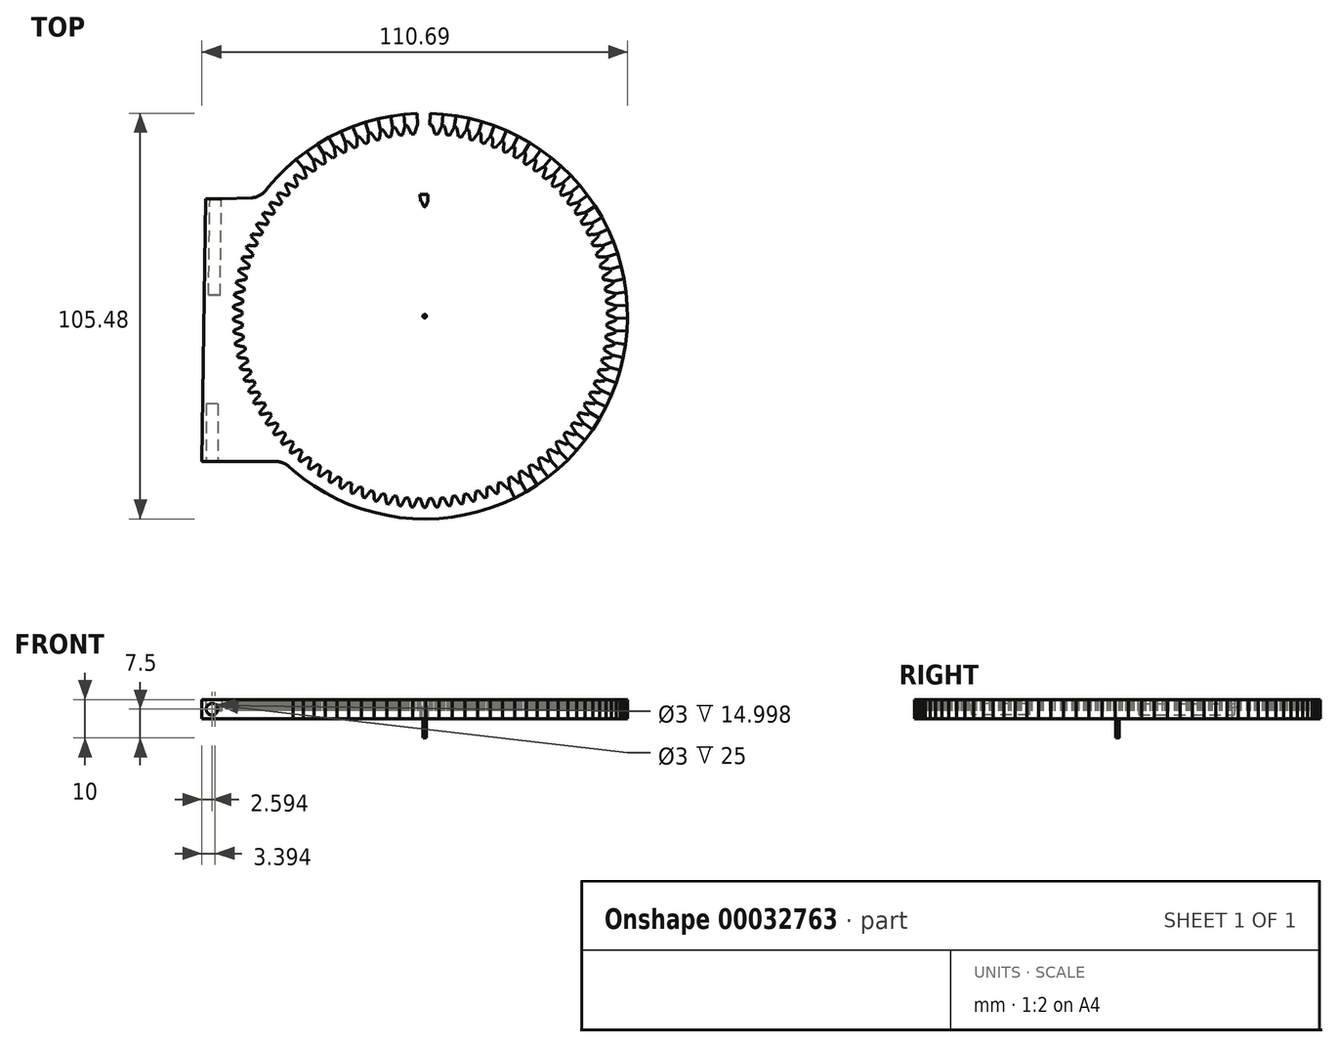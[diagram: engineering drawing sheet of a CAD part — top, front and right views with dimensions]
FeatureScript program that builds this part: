
annotation { "Feature Type Name" : "Feature", "Feature Type Description" : "" }
export const myFeature = defineFeature(function(context is Context, id is Id, definition is map)
    precondition{}
    {
        {
            var Q0;
            Q0=qCreatedBy(makeId("Top.planeOp"),FACE);
            var sketch = newSketch(context, id + "F0", { "sketchPlane" : qUnion([Q0])});
            skCircle(sketch, "E0", {"center": v(0, 0) * mm, "radius": 52.75 * mm});
            skLineSegment(sketch, "E1", {"start": v(1.31, 49.73) * mm, "end": v(1.3, 49.69) * mm});
            skLineSegment(sketch, "E2", {"start": v(1.3, 49.69) * mm, "end": v(1.27, 49.64) * mm});
            skLineSegment(sketch, "E3", {"start": v(1.27, 49.64) * mm, "end": v(1.25, 49.6) * mm});
            skLineSegment(sketch, "E4", {"start": v(1.25, 49.6) * mm, "end": v(1.23, 49.55) * mm});
            skLineSegment(sketch, "E5", {"start": v(1.23, 49.55) * mm, "end": v(1.21, 49.51) * mm});
            skLineSegment(sketch, "E6", {"start": v(1.21, 49.51) * mm, "end": v(1.2, 49.47) * mm});
            skLineSegment(sketch, "E7", {"start": v(1.2, 49.47) * mm, "end": v(1.17, 49.42) * mm});
            skLineSegment(sketch, "E8", {"start": v(1.17, 49.42) * mm, "end": v(1.15, 49.38) * mm});
            skLineSegment(sketch, "E9", {"start": v(1.15, 49.38) * mm, "end": v(1.13, 49.33) * mm});
            skLineSegment(sketch, "E10", {"start": v(1.13, 49.33) * mm, "end": v(1.11, 49.29) * mm});
            skLineSegment(sketch, "E11", {"start": v(1.11, 49.29) * mm, "end": v(1.1, 49.24) * mm});
            skLineSegment(sketch, "E12", {"start": v(1.1, 49.24) * mm, "end": v(1.07, 49.2) * mm});
            skLineSegment(sketch, "E13", {"start": v(1.07, 49.2) * mm, "end": v(1.05, 49.15) * mm});
            skLineSegment(sketch, "E14", {"start": v(1.05, 49.15) * mm, "end": v(1.03, 49.1) * mm});
            skLineSegment(sketch, "E15", {"start": v(1.03, 49.1) * mm, "end": v(1.02, 49.06) * mm});
            skLineSegment(sketch, "E16", {"start": v(1.02, 49.06) * mm, "end": v(1, 49.02) * mm});
            skLineSegment(sketch, "E17", {"start": v(1, 49.02) * mm, "end": v(0.98, 48.98) * mm});
            skLineSegment(sketch, "E18", {"start": v(0.98, 48.98) * mm, "end": v(0.96, 48.93) * mm});
            skLineSegment(sketch, "E19", {"start": v(0.96, 48.93) * mm, "end": v(0.94, 48.89) * mm});
            skLineSegment(sketch, "E20", {"start": v(0.94, 48.89) * mm, "end": v(0.92, 48.84) * mm});
            skLineSegment(sketch, "E21", {"start": v(0.92, 48.84) * mm, "end": v(0.9, 48.8) * mm});
            skLineSegment(sketch, "E22", {"start": v(0.9, 48.8) * mm, "end": v(0.89, 48.75) * mm});
            skLineSegment(sketch, "E23", {"start": v(0.89, 48.75) * mm, "end": v(0.87, 48.7) * mm});
            skLineSegment(sketch, "E24", {"start": v(0.87, 48.7) * mm, "end": v(0.85, 48.66) * mm});
            skLineSegment(sketch, "E25", {"start": v(0.85, 48.66) * mm, "end": v(0.83, 48.62) * mm});
            skLineSegment(sketch, "E26", {"start": v(0.83, 48.62) * mm, "end": v(0.82, 48.57) * mm});
            skLineSegment(sketch, "E27", {"start": v(0.82, 48.57) * mm, "end": v(0.8, 48.53) * mm});
            skLineSegment(sketch, "E28", {"start": v(0.8, 48.53) * mm, "end": v(0.78, 48.48) * mm});
            skLineSegment(sketch, "E29", {"start": v(0.78, 48.48) * mm, "end": v(0.76, 48.44) * mm});
            skLineSegment(sketch, "E30", {"start": v(0.76, 48.44) * mm, "end": v(0.75, 48.4) * mm});
            skLineSegment(sketch, "E31", {"start": v(0.75, 48.4) * mm, "end": v(0.73, 48.35) * mm});
            skLineSegment(sketch, "E32", {"start": v(0.73, 48.35) * mm, "end": v(0.71, 48.3) * mm});
            skLineSegment(sketch, "E33", {"start": v(0.71, 48.3) * mm, "end": v(0.7, 48.26) * mm});
            skLineSegment(sketch, "E34", {"start": v(0.7, 48.26) * mm, "end": v(0.68, 48.22) * mm});
            skLineSegment(sketch, "E35", {"start": v(0.68, 48.22) * mm, "end": v(0.67, 48.17) * mm});
            skLineSegment(sketch, "E36", {"start": v(0.67, 48.17) * mm, "end": v(0.65, 48.13) * mm});
            skLineSegment(sketch, "E37", {"start": v(0.65, 48.13) * mm, "end": v(0.63, 48.08) * mm});
            skLineSegment(sketch, "E38", {"start": v(0.63, 48.08) * mm, "end": v(0.62, 48.04) * mm});
            skLineSegment(sketch, "E39", {"start": v(0.62, 48.04) * mm, "end": v(0.6, 48) * mm});
            skLineSegment(sketch, "E40", {"start": v(0.6, 48) * mm, "end": v(0.58, 47.95) * mm});
            skLineSegment(sketch, "E41", {"start": v(0.58, 47.95) * mm, "end": v(0.57, 47.9) * mm});
            skLineSegment(sketch, "E42", {"start": v(0.57, 47.9) * mm, "end": v(0.55, 47.86) * mm});
            skLineSegment(sketch, "E43", {"start": v(0.55, 47.86) * mm, "end": v(0.53, 47.81) * mm});
            skLineSegment(sketch, "E44", {"start": v(0.53, 47.81) * mm, "end": v(0.52, 47.77) * mm});
            skLineSegment(sketch, "E45", {"start": v(0.52, 47.77) * mm, "end": v(0.5, 47.72) * mm});
            skLineSegment(sketch, "E46", {"start": v(0.5, 47.72) * mm, "end": v(0.49, 47.68) * mm});
            skLineSegment(sketch, "E47", {"start": v(0.49, 47.68) * mm, "end": v(0.47, 47.63) * mm});
            skLineSegment(sketch, "E48", {"start": v(0.47, 47.63) * mm, "end": v(0.45, 47.59) * mm});
            skLineSegment(sketch, "E49", {"start": v(0.45, 47.59) * mm, "end": v(0.44, 47.54) * mm});
            skLineSegment(sketch, "E50", {"start": v(0.44, 47.54) * mm, "end": v(0, 47.5) * mm});
            skLineSegment(sketch, "E51", {"start": v(0, 47.5) * mm, "end": v(-0.44, 47.54) * mm});
            skLineSegment(sketch, "E52", {"start": v(-0.44, 47.54) * mm, "end": v(-0.45, 47.59) * mm});
            skLineSegment(sketch, "E53", {"start": v(-0.45, 47.59) * mm, "end": v(-0.47, 47.63) * mm});
            skLineSegment(sketch, "E54", {"start": v(-0.47, 47.63) * mm, "end": v(-0.49, 47.68) * mm});
            skLineSegment(sketch, "E55", {"start": v(-0.49, 47.68) * mm, "end": v(-0.5, 47.72) * mm});
            skLineSegment(sketch, "E56", {"start": v(-0.5, 47.72) * mm, "end": v(-0.52, 47.77) * mm});
            skLineSegment(sketch, "E57", {"start": v(-0.52, 47.77) * mm, "end": v(-0.53, 47.81) * mm});
            skLineSegment(sketch, "E58", {"start": v(-0.53, 47.81) * mm, "end": v(-0.55, 47.86) * mm});
            skLineSegment(sketch, "E59", {"start": v(-0.55, 47.86) * mm, "end": v(-0.57, 47.9) * mm});
            skLineSegment(sketch, "E60", {"start": v(-0.57, 47.9) * mm, "end": v(-0.58, 47.95) * mm});
            skLineSegment(sketch, "E61", {"start": v(-0.58, 47.95) * mm, "end": v(-0.6, 48) * mm});
            skLineSegment(sketch, "E62", {"start": v(-0.6, 48) * mm, "end": v(-0.62, 48.04) * mm});
            skLineSegment(sketch, "E63", {"start": v(-0.62, 48.04) * mm, "end": v(-0.63, 48.08) * mm});
            skLineSegment(sketch, "E64", {"start": v(-0.63, 48.08) * mm, "end": v(-0.65, 48.13) * mm});
            skLineSegment(sketch, "E65", {"start": v(-0.65, 48.13) * mm, "end": v(-0.67, 48.17) * mm});
            skLineSegment(sketch, "E66", {"start": v(-0.67, 48.17) * mm, "end": v(-0.68, 48.22) * mm});
            skLineSegment(sketch, "E67", {"start": v(-0.68, 48.22) * mm, "end": v(-0.7, 48.26) * mm});
            skLineSegment(sketch, "E68", {"start": v(-0.7, 48.26) * mm, "end": v(-0.71, 48.3) * mm});
            skLineSegment(sketch, "E69", {"start": v(-0.71, 48.3) * mm, "end": v(-0.73, 48.35) * mm});
            skLineSegment(sketch, "E70", {"start": v(-0.73, 48.35) * mm, "end": v(-0.75, 48.4) * mm});
            skLineSegment(sketch, "E71", {"start": v(-0.75, 48.4) * mm, "end": v(-0.76, 48.44) * mm});
            skLineSegment(sketch, "E72", {"start": v(-0.76, 48.44) * mm, "end": v(-0.78, 48.48) * mm});
            skLineSegment(sketch, "E73", {"start": v(-0.78, 48.48) * mm, "end": v(-0.8, 48.53) * mm});
            skLineSegment(sketch, "E74", {"start": v(-0.8, 48.53) * mm, "end": v(-0.82, 48.57) * mm});
            skLineSegment(sketch, "E75", {"start": v(-0.82, 48.57) * mm, "end": v(-0.83, 48.62) * mm});
            skLineSegment(sketch, "E76", {"start": v(-0.83, 48.62) * mm, "end": v(-0.85, 48.66) * mm});
            skLineSegment(sketch, "E77", {"start": v(-0.85, 48.66) * mm, "end": v(-0.87, 48.7) * mm});
            skLineSegment(sketch, "E78", {"start": v(-0.87, 48.7) * mm, "end": v(-0.89, 48.75) * mm});
            skLineSegment(sketch, "E79", {"start": v(-0.89, 48.75) * mm, "end": v(-0.9, 48.8) * mm});
            skLineSegment(sketch, "E80", {"start": v(-0.9, 48.8) * mm, "end": v(-0.92, 48.84) * mm});
            skLineSegment(sketch, "E81", {"start": v(-0.92, 48.84) * mm, "end": v(-0.94, 48.89) * mm});
            skLineSegment(sketch, "E82", {"start": v(-0.94, 48.89) * mm, "end": v(-0.96, 48.93) * mm});
            skLineSegment(sketch, "E83", {"start": v(-0.96, 48.93) * mm, "end": v(-0.98, 48.98) * mm});
            skLineSegment(sketch, "E84", {"start": v(-0.98, 48.98) * mm, "end": v(-1, 49.02) * mm});
            skLineSegment(sketch, "E85", {"start": v(-1, 49.02) * mm, "end": v(-1.02, 49.06) * mm});
            skLineSegment(sketch, "E86", {"start": v(-1.02, 49.06) * mm, "end": v(-1.03, 49.1) * mm});
            skLineSegment(sketch, "E87", {"start": v(-1.03, 49.1) * mm, "end": v(-1.05, 49.15) * mm});
            skLineSegment(sketch, "E88", {"start": v(-1.05, 49.15) * mm, "end": v(-1.07, 49.2) * mm});
            skLineSegment(sketch, "E89", {"start": v(-1.07, 49.2) * mm, "end": v(-1.1, 49.24) * mm});
            skLineSegment(sketch, "E90", {"start": v(-1.1, 49.24) * mm, "end": v(-1.11, 49.29) * mm});
            skLineSegment(sketch, "E91", {"start": v(-1.11, 49.29) * mm, "end": v(-1.13, 49.33) * mm});
            skLineSegment(sketch, "E92", {"start": v(-1.13, 49.33) * mm, "end": v(-1.15, 49.38) * mm});
            skLineSegment(sketch, "E93", {"start": v(-1.15, 49.38) * mm, "end": v(-1.17, 49.42) * mm});
            skLineSegment(sketch, "E94", {"start": v(-1.17, 49.42) * mm, "end": v(-1.2, 49.47) * mm});
            skLineSegment(sketch, "E95", {"start": v(-1.2, 49.47) * mm, "end": v(-1.21, 49.51) * mm});
            skLineSegment(sketch, "E96", {"start": v(-1.21, 49.51) * mm, "end": v(-1.23, 49.55) * mm});
            skLineSegment(sketch, "E97", {"start": v(-1.23, 49.55) * mm, "end": v(-1.25, 49.6) * mm});
            skLineSegment(sketch, "E98", {"start": v(-1.25, 49.6) * mm, "end": v(-1.27, 49.64) * mm});
            skLineSegment(sketch, "E99", {"start": v(-1.27, 49.64) * mm, "end": v(-1.3, 49.69) * mm});
            skLineSegment(sketch, "E100", {"start": v(-1.3, 49.69) * mm, "end": v(-1.31, 49.73) * mm});
            skLineSegment(sketch, "E101", {"start": v(-1.31, 49.73) * mm, "end": v(-1.9, 49.71) * mm});
            skLineSegment(sketch, "E102", {"start": v(0, 0) * mm, "end": v(-2.02, 52.71) * mm});
            skLineSegment(sketch, "E103", {"start": v(0, 0) * mm, "end": v(1.4, 52.73) * mm});
            skLineSegment(sketch, "E104", {"start": v(-2.02, 52.71) * mm, "end": v(1.4, 52.73) * mm});
            skCircle(sketch, "E105", {"center": v(0, 0) * mm, "radius": 0.44 * mm});
            skSolve(sketch);
        }
        {
            var Q0;
            {var subQ3=sQuery(id+"F0.wireOp",EDGE,"E1");Q0=makeQuery(id+"F0.imprint","IMPRINT",FACE,{"disambiguationData":[TD([[makeQuery(id+"F0.imprint","IMPRINT",EDGE,{"derivedFrom":subQ3}),-1.0]])]});}
            var Q1;
            {var subQ1=sQuery(id+"F0.wireOp",EDGE,"E103");var subQ3=sQuery(id+"F0.wireOp",EDGE,"E102");var subQ5=makeQuery(id+"F0.imprint","INTERSECT",VERTEX,{"derivedFrom":[subQ3,subQ1]});Q1=makeQuery(id+"F0.imprint","IMPRINT",FACE,{"disambiguationData":[TD([[makeQuery(id+"F0.imprint","IMPRINT",EDGE,{"disambiguationData":[TD([[subQ5,-1.0]])],"derivedFrom":subQ3}),1.0]])]});}
            var Q2;
            {var subQ0=sQuery(id+"F0.wireOp",EDGE,"E103");var subQ3=sQuery(id+"F0.wireOp",EDGE,"E102");var subQ4=makeQuery(id+"F0.imprint","INTERSECT",VERTEX,{"derivedFrom":[subQ3,subQ0]});Q2=makeQuery(id+"F0.imprint","IMPRINT",FACE,{"disambiguationData":[TD([[makeQuery(id+"F0.imprint","IMPRINT",EDGE,{"disambiguationData":[TD([[subQ4,-1.0]])],"derivedFrom":subQ3}),-1.0]])]});}
            extrude(context, id + "F1", {"entities" : qUnion([Q0, Q1, Q2]), "depth" : 5 * mm});
        }
        {
            var Q0;
            Q0=makeQuery(id+"F1.opExtrude","SWEPT_BODY",BODY,{"disambiguationData":[OSD([sQuery(id+"F0.wireOp",EDGE,"E1"),sQuery(id+"F0.wireOp",EDGE,"E2"),sQuery(id+"F0.wireOp",EDGE,"E3"),sQuery(id+"F0.wireOp",EDGE,"E4"),sQuery(id+"F0.wireOp",EDGE,"E5"),sQuery(id+"F0.wireOp",EDGE,"E6"),sQuery(id+"F0.wireOp",EDGE,"E7"),sQuery(id+"F0.wireOp",EDGE,"E8"),sQuery(id+"F0.wireOp",EDGE,"E9"),sQuery(id+"F0.wireOp",EDGE,"E10"),sQuery(id+"F0.wireOp",EDGE,"E11"),sQuery(id+"F0.wireOp",EDGE,"E12"),sQuery(id+"F0.wireOp",EDGE,"E13"),sQuery(id+"F0.wireOp",EDGE,"E14"),sQuery(id+"F0.wireOp",EDGE,"E15"),sQuery(id+"F0.wireOp",EDGE,"E16"),sQuery(id+"F0.wireOp",EDGE,"E17"),sQuery(id+"F0.wireOp",EDGE,"E18"),sQuery(id+"F0.wireOp",EDGE,"E19"),sQuery(id+"F0.wireOp",EDGE,"E20"),sQuery(id+"F0.wireOp",EDGE,"E21"),sQuery(id+"F0.wireOp",EDGE,"E22"),sQuery(id+"F0.wireOp",EDGE,"E23"),sQuery(id+"F0.wireOp",EDGE,"E24"),sQuery(id+"F0.wireOp",EDGE,"E25"),sQuery(id+"F0.wireOp",EDGE,"E26"),sQuery(id+"F0.wireOp",EDGE,"E27"),sQuery(id+"F0.wireOp",EDGE,"E28"),sQuery(id+"F0.wireOp",EDGE,"E29"),sQuery(id+"F0.wireOp",EDGE,"E30"),sQuery(id+"F0.wireOp",EDGE,"E31"),sQuery(id+"F0.wireOp",EDGE,"E32"),sQuery(id+"F0.wireOp",EDGE,"E33"),sQuery(id+"F0.wireOp",EDGE,"E34"),sQuery(id+"F0.wireOp",EDGE,"E35"),sQuery(id+"F0.wireOp",EDGE,"E36"),sQuery(id+"F0.wireOp",EDGE,"E37"),sQuery(id+"F0.wireOp",EDGE,"E38"),sQuery(id+"F0.wireOp",EDGE,"E39"),sQuery(id+"F0.wireOp",EDGE,"E40"),sQuery(id+"F0.wireOp",EDGE,"E41"),sQuery(id+"F0.wireOp",EDGE,"E42"),sQuery(id+"F0.wireOp",EDGE,"E43"),sQuery(id+"F0.wireOp",EDGE,"E44"),sQuery(id+"F0.wireOp",EDGE,"E45"),sQuery(id+"F0.wireOp",EDGE,"E46"),sQuery(id+"F0.wireOp",EDGE,"E47"),sQuery(id+"F0.wireOp",EDGE,"E48"),sQuery(id+"F0.wireOp",EDGE,"E49"),sQuery(id+"F0.wireOp",EDGE,"E50"),sQuery(id+"F0.wireOp",EDGE,"E51"),sQuery(id+"F0.wireOp",EDGE,"E52"),sQuery(id+"F0.wireOp",EDGE,"E53"),sQuery(id+"F0.wireOp",EDGE,"E54"),sQuery(id+"F0.wireOp",EDGE,"E55"),sQuery(id+"F0.wireOp",EDGE,"E56"),sQuery(id+"F0.wireOp",EDGE,"E57"),sQuery(id+"F0.wireOp",EDGE,"E58"),sQuery(id+"F0.wireOp",EDGE,"E59"),sQuery(id+"F0.wireOp",EDGE,"E60"),sQuery(id+"F0.wireOp",EDGE,"E61"),sQuery(id+"F0.wireOp",EDGE,"E62"),sQuery(id+"F0.wireOp",EDGE,"E63"),sQuery(id+"F0.wireOp",EDGE,"E64"),sQuery(id+"F0.wireOp",EDGE,"E65"),sQuery(id+"F0.wireOp",EDGE,"E66"),sQuery(id+"F0.wireOp",EDGE,"E67"),sQuery(id+"F0.wireOp",EDGE,"E68"),sQuery(id+"F0.wireOp",EDGE,"E69"),sQuery(id+"F0.wireOp",EDGE,"E70"),sQuery(id+"F0.wireOp",EDGE,"E71"),sQuery(id+"F0.wireOp",EDGE,"E72"),sQuery(id+"F0.wireOp",EDGE,"E73"),sQuery(id+"F0.wireOp",EDGE,"E74"),sQuery(id+"F0.wireOp",EDGE,"E75"),sQuery(id+"F0.wireOp",EDGE,"E76"),sQuery(id+"F0.wireOp",EDGE,"E77"),sQuery(id+"F0.wireOp",EDGE,"E78"),sQuery(id+"F0.wireOp",EDGE,"E79"),sQuery(id+"F0.wireOp",EDGE,"E80"),sQuery(id+"F0.wireOp",EDGE,"E81"),sQuery(id+"F0.wireOp",EDGE,"E82"),sQuery(id+"F0.wireOp",EDGE,"E83"),sQuery(id+"F0.wireOp",EDGE,"E84"),sQuery(id+"F0.wireOp",EDGE,"E85"),sQuery(id+"F0.wireOp",EDGE,"E86"),sQuery(id+"F0.wireOp",EDGE,"E87"),sQuery(id+"F0.wireOp",EDGE,"E88"),sQuery(id+"F0.wireOp",EDGE,"E89"),sQuery(id+"F0.wireOp",EDGE,"E90"),sQuery(id+"F0.wireOp",EDGE,"E91"),sQuery(id+"F0.wireOp",EDGE,"E92"),sQuery(id+"F0.wireOp",EDGE,"E93"),sQuery(id+"F0.wireOp",EDGE,"E94"),sQuery(id+"F0.wireOp",EDGE,"E95"),sQuery(id+"F0.wireOp",EDGE,"E96"),sQuery(id+"F0.wireOp",EDGE,"E97"),sQuery(id+"F0.wireOp",EDGE,"E98"),sQuery(id+"F0.wireOp",EDGE,"E99"),sQuery(id+"F0.wireOp",EDGE,"E100"),sQuery(id+"F0.wireOp",EDGE,"E101"),sQuery(id+"F0.wireOp",EDGE,"E102"),sQuery(id+"F0.wireOp",EDGE,"E103"),sQuery(id+"F0.wireOp",EDGE,"E104")])]});
            var Q1;
            Q1=makeQuery(id+"F1.opExtrude","CAP_EDGE",EDGE,{"disambiguationData":[OSD([sQuery(id+"F0.wireOp",EDGE,"E105")])],"isStart":false});
            circularPattern(context, id + "F2", {"entities" : qUnion([Q0]), "axis" : qUnion([Q1]), "angle" : 3.7 * degree, "instanceCount" : round(97)});
        }
        {
            var Q0;
            Q0=makeQuery(id+"F1.opExtrude","SWEPT_BODY",BODY,{"disambiguationData":[OSD([sQuery(id+"F0.wireOp",EDGE,"E105")])]});
            var Q1;
            Q1=makeQuery(id+"F2.opPattern","COPY",BODY,{"derivedFrom":makeQuery(id+"F1.opExtrude","SWEPT_BODY",BODY,{"disambiguationData":[OSD([sQuery(id+"F0.wireOp",EDGE,"E1"),sQuery(id+"F0.wireOp",EDGE,"E2"),sQuery(id+"F0.wireOp",EDGE,"E3"),sQuery(id+"F0.wireOp",EDGE,"E4"),sQuery(id+"F0.wireOp",EDGE,"E5"),sQuery(id+"F0.wireOp",EDGE,"E6"),sQuery(id+"F0.wireOp",EDGE,"E7"),sQuery(id+"F0.wireOp",EDGE,"E8"),sQuery(id+"F0.wireOp",EDGE,"E9"),sQuery(id+"F0.wireOp",EDGE,"E10"),sQuery(id+"F0.wireOp",EDGE,"E11"),sQuery(id+"F0.wireOp",EDGE,"E12"),sQuery(id+"F0.wireOp",EDGE,"E13"),sQuery(id+"F0.wireOp",EDGE,"E14"),sQuery(id+"F0.wireOp",EDGE,"E15"),sQuery(id+"F0.wireOp",EDGE,"E16"),sQuery(id+"F0.wireOp",EDGE,"E17"),sQuery(id+"F0.wireOp",EDGE,"E18"),sQuery(id+"F0.wireOp",EDGE,"E19"),sQuery(id+"F0.wireOp",EDGE,"E20"),sQuery(id+"F0.wireOp",EDGE,"E21"),sQuery(id+"F0.wireOp",EDGE,"E22"),sQuery(id+"F0.wireOp",EDGE,"E23"),sQuery(id+"F0.wireOp",EDGE,"E24"),sQuery(id+"F0.wireOp",EDGE,"E25"),sQuery(id+"F0.wireOp",EDGE,"E26"),sQuery(id+"F0.wireOp",EDGE,"E27"),sQuery(id+"F0.wireOp",EDGE,"E28"),sQuery(id+"F0.wireOp",EDGE,"E29"),sQuery(id+"F0.wireOp",EDGE,"E30"),sQuery(id+"F0.wireOp",EDGE,"E31"),sQuery(id+"F0.wireOp",EDGE,"E32"),sQuery(id+"F0.wireOp",EDGE,"E33"),sQuery(id+"F0.wireOp",EDGE,"E34"),sQuery(id+"F0.wireOp",EDGE,"E35"),sQuery(id+"F0.wireOp",EDGE,"E36"),sQuery(id+"F0.wireOp",EDGE,"E37"),sQuery(id+"F0.wireOp",EDGE,"E38"),sQuery(id+"F0.wireOp",EDGE,"E39"),sQuery(id+"F0.wireOp",EDGE,"E40"),sQuery(id+"F0.wireOp",EDGE,"E41"),sQuery(id+"F0.wireOp",EDGE,"E42"),sQuery(id+"F0.wireOp",EDGE,"E43"),sQuery(id+"F0.wireOp",EDGE,"E44"),sQuery(id+"F0.wireOp",EDGE,"E45"),sQuery(id+"F0.wireOp",EDGE,"E46"),sQuery(id+"F0.wireOp",EDGE,"E47"),sQuery(id+"F0.wireOp",EDGE,"E48"),sQuery(id+"F0.wireOp",EDGE,"E49"),sQuery(id+"F0.wireOp",EDGE,"E50"),sQuery(id+"F0.wireOp",EDGE,"E51"),sQuery(id+"F0.wireOp",EDGE,"E52"),sQuery(id+"F0.wireOp",EDGE,"E53"),sQuery(id+"F0.wireOp",EDGE,"E54"),sQuery(id+"F0.wireOp",EDGE,"E55"),sQuery(id+"F0.wireOp",EDGE,"E56"),sQuery(id+"F0.wireOp",EDGE,"E57"),sQuery(id+"F0.wireOp",EDGE,"E58"),sQuery(id+"F0.wireOp",EDGE,"E59"),sQuery(id+"F0.wireOp",EDGE,"E60"),sQuery(id+"F0.wireOp",EDGE,"E61"),sQuery(id+"F0.wireOp",EDGE,"E62"),sQuery(id+"F0.wireOp",EDGE,"E63"),sQuery(id+"F0.wireOp",EDGE,"E64"),sQuery(id+"F0.wireOp",EDGE,"E65"),sQuery(id+"F0.wireOp",EDGE,"E66"),sQuery(id+"F0.wireOp",EDGE,"E67"),sQuery(id+"F0.wireOp",EDGE,"E68"),sQuery(id+"F0.wireOp",EDGE,"E69"),sQuery(id+"F0.wireOp",EDGE,"E70"),sQuery(id+"F0.wireOp",EDGE,"E71"),sQuery(id+"F0.wireOp",EDGE,"E72"),sQuery(id+"F0.wireOp",EDGE,"E73"),sQuery(id+"F0.wireOp",EDGE,"E74"),sQuery(id+"F0.wireOp",EDGE,"E75"),sQuery(id+"F0.wireOp",EDGE,"E76"),sQuery(id+"F0.wireOp",EDGE,"E77"),sQuery(id+"F0.wireOp",EDGE,"E78"),sQuery(id+"F0.wireOp",EDGE,"E79"),sQuery(id+"F0.wireOp",EDGE,"E80"),sQuery(id+"F0.wireOp",EDGE,"E81"),sQuery(id+"F0.wireOp",EDGE,"E82"),sQuery(id+"F0.wireOp",EDGE,"E83"),sQuery(id+"F0.wireOp",EDGE,"E84"),sQuery(id+"F0.wireOp",EDGE,"E85"),sQuery(id+"F0.wireOp",EDGE,"E86"),sQuery(id+"F0.wireOp",EDGE,"E87"),sQuery(id+"F0.wireOp",EDGE,"E88"),sQuery(id+"F0.wireOp",EDGE,"E89"),sQuery(id+"F0.wireOp",EDGE,"E90"),sQuery(id+"F0.wireOp",EDGE,"E91"),sQuery(id+"F0.wireOp",EDGE,"E92"),sQuery(id+"F0.wireOp",EDGE,"E93"),sQuery(id+"F0.wireOp",EDGE,"E94"),sQuery(id+"F0.wireOp",EDGE,"E95"),sQuery(id+"F0.wireOp",EDGE,"E96"),sQuery(id+"F0.wireOp",EDGE,"E97"),sQuery(id+"F0.wireOp",EDGE,"E98"),sQuery(id+"F0.wireOp",EDGE,"E99"),sQuery(id+"F0.wireOp",EDGE,"E100"),sQuery(id+"F0.wireOp",EDGE,"E101"),sQuery(id+"F0.wireOp",EDGE,"E102"),sQuery(id+"F0.wireOp",EDGE,"E103"),sQuery(id+"F0.wireOp",EDGE,"E104")])]}),"instanceName":"1"});
            var Q2;
            Q2=makeQuery(id+"F2.opPattern","COPY",BODY,{"derivedFrom":makeQuery(id+"F1.opExtrude","SWEPT_BODY",BODY,{"disambiguationData":[OSD([sQuery(id+"F0.wireOp",EDGE,"E1"),sQuery(id+"F0.wireOp",EDGE,"E2"),sQuery(id+"F0.wireOp",EDGE,"E3"),sQuery(id+"F0.wireOp",EDGE,"E4"),sQuery(id+"F0.wireOp",EDGE,"E5"),sQuery(id+"F0.wireOp",EDGE,"E6"),sQuery(id+"F0.wireOp",EDGE,"E7"),sQuery(id+"F0.wireOp",EDGE,"E8"),sQuery(id+"F0.wireOp",EDGE,"E9"),sQuery(id+"F0.wireOp",EDGE,"E10"),sQuery(id+"F0.wireOp",EDGE,"E11"),sQuery(id+"F0.wireOp",EDGE,"E12"),sQuery(id+"F0.wireOp",EDGE,"E13"),sQuery(id+"F0.wireOp",EDGE,"E14"),sQuery(id+"F0.wireOp",EDGE,"E15"),sQuery(id+"F0.wireOp",EDGE,"E16"),sQuery(id+"F0.wireOp",EDGE,"E17"),sQuery(id+"F0.wireOp",EDGE,"E18"),sQuery(id+"F0.wireOp",EDGE,"E19"),sQuery(id+"F0.wireOp",EDGE,"E20"),sQuery(id+"F0.wireOp",EDGE,"E21"),sQuery(id+"F0.wireOp",EDGE,"E22"),sQuery(id+"F0.wireOp",EDGE,"E23"),sQuery(id+"F0.wireOp",EDGE,"E24"),sQuery(id+"F0.wireOp",EDGE,"E25"),sQuery(id+"F0.wireOp",EDGE,"E26"),sQuery(id+"F0.wireOp",EDGE,"E27"),sQuery(id+"F0.wireOp",EDGE,"E28"),sQuery(id+"F0.wireOp",EDGE,"E29"),sQuery(id+"F0.wireOp",EDGE,"E30"),sQuery(id+"F0.wireOp",EDGE,"E31"),sQuery(id+"F0.wireOp",EDGE,"E32"),sQuery(id+"F0.wireOp",EDGE,"E33"),sQuery(id+"F0.wireOp",EDGE,"E34"),sQuery(id+"F0.wireOp",EDGE,"E35"),sQuery(id+"F0.wireOp",EDGE,"E36"),sQuery(id+"F0.wireOp",EDGE,"E37"),sQuery(id+"F0.wireOp",EDGE,"E38"),sQuery(id+"F0.wireOp",EDGE,"E39"),sQuery(id+"F0.wireOp",EDGE,"E40"),sQuery(id+"F0.wireOp",EDGE,"E41"),sQuery(id+"F0.wireOp",EDGE,"E42"),sQuery(id+"F0.wireOp",EDGE,"E43"),sQuery(id+"F0.wireOp",EDGE,"E44"),sQuery(id+"F0.wireOp",EDGE,"E45"),sQuery(id+"F0.wireOp",EDGE,"E46"),sQuery(id+"F0.wireOp",EDGE,"E47"),sQuery(id+"F0.wireOp",EDGE,"E48"),sQuery(id+"F0.wireOp",EDGE,"E49"),sQuery(id+"F0.wireOp",EDGE,"E50"),sQuery(id+"F0.wireOp",EDGE,"E51"),sQuery(id+"F0.wireOp",EDGE,"E52"),sQuery(id+"F0.wireOp",EDGE,"E53"),sQuery(id+"F0.wireOp",EDGE,"E54"),sQuery(id+"F0.wireOp",EDGE,"E55"),sQuery(id+"F0.wireOp",EDGE,"E56"),sQuery(id+"F0.wireOp",EDGE,"E57"),sQuery(id+"F0.wireOp",EDGE,"E58"),sQuery(id+"F0.wireOp",EDGE,"E59"),sQuery(id+"F0.wireOp",EDGE,"E60"),sQuery(id+"F0.wireOp",EDGE,"E61"),sQuery(id+"F0.wireOp",EDGE,"E62"),sQuery(id+"F0.wireOp",EDGE,"E63"),sQuery(id+"F0.wireOp",EDGE,"E64"),sQuery(id+"F0.wireOp",EDGE,"E65"),sQuery(id+"F0.wireOp",EDGE,"E66"),sQuery(id+"F0.wireOp",EDGE,"E67"),sQuery(id+"F0.wireOp",EDGE,"E68"),sQuery(id+"F0.wireOp",EDGE,"E69"),sQuery(id+"F0.wireOp",EDGE,"E70"),sQuery(id+"F0.wireOp",EDGE,"E71"),sQuery(id+"F0.wireOp",EDGE,"E72"),sQuery(id+"F0.wireOp",EDGE,"E73"),sQuery(id+"F0.wireOp",EDGE,"E74"),sQuery(id+"F0.wireOp",EDGE,"E75"),sQuery(id+"F0.wireOp",EDGE,"E76"),sQuery(id+"F0.wireOp",EDGE,"E77"),sQuery(id+"F0.wireOp",EDGE,"E78"),sQuery(id+"F0.wireOp",EDGE,"E79"),sQuery(id+"F0.wireOp",EDGE,"E80"),sQuery(id+"F0.wireOp",EDGE,"E81"),sQuery(id+"F0.wireOp",EDGE,"E82"),sQuery(id+"F0.wireOp",EDGE,"E83"),sQuery(id+"F0.wireOp",EDGE,"E84"),sQuery(id+"F0.wireOp",EDGE,"E85"),sQuery(id+"F0.wireOp",EDGE,"E86"),sQuery(id+"F0.wireOp",EDGE,"E87"),sQuery(id+"F0.wireOp",EDGE,"E88"),sQuery(id+"F0.wireOp",EDGE,"E89"),sQuery(id+"F0.wireOp",EDGE,"E90"),sQuery(id+"F0.wireOp",EDGE,"E91"),sQuery(id+"F0.wireOp",EDGE,"E92"),sQuery(id+"F0.wireOp",EDGE,"E93"),sQuery(id+"F0.wireOp",EDGE,"E94"),sQuery(id+"F0.wireOp",EDGE,"E95"),sQuery(id+"F0.wireOp",EDGE,"E96"),sQuery(id+"F0.wireOp",EDGE,"E97"),sQuery(id+"F0.wireOp",EDGE,"E98"),sQuery(id+"F0.wireOp",EDGE,"E99"),sQuery(id+"F0.wireOp",EDGE,"E100"),sQuery(id+"F0.wireOp",EDGE,"E101"),sQuery(id+"F0.wireOp",EDGE,"E102"),sQuery(id+"F0.wireOp",EDGE,"E103"),sQuery(id+"F0.wireOp",EDGE,"E104")])]}),"instanceName":"11"});
            var Q3;
            Q3=makeQuery(id+"F2.opPattern","COPY",BODY,{"derivedFrom":makeQuery(id+"F1.opExtrude","SWEPT_BODY",BODY,{"disambiguationData":[OSD([sQuery(id+"F0.wireOp",EDGE,"E1"),sQuery(id+"F0.wireOp",EDGE,"E2"),sQuery(id+"F0.wireOp",EDGE,"E3"),sQuery(id+"F0.wireOp",EDGE,"E4"),sQuery(id+"F0.wireOp",EDGE,"E5"),sQuery(id+"F0.wireOp",EDGE,"E6"),sQuery(id+"F0.wireOp",EDGE,"E7"),sQuery(id+"F0.wireOp",EDGE,"E8"),sQuery(id+"F0.wireOp",EDGE,"E9"),sQuery(id+"F0.wireOp",EDGE,"E10"),sQuery(id+"F0.wireOp",EDGE,"E11"),sQuery(id+"F0.wireOp",EDGE,"E12"),sQuery(id+"F0.wireOp",EDGE,"E13"),sQuery(id+"F0.wireOp",EDGE,"E14"),sQuery(id+"F0.wireOp",EDGE,"E15"),sQuery(id+"F0.wireOp",EDGE,"E16"),sQuery(id+"F0.wireOp",EDGE,"E17"),sQuery(id+"F0.wireOp",EDGE,"E18"),sQuery(id+"F0.wireOp",EDGE,"E19"),sQuery(id+"F0.wireOp",EDGE,"E20"),sQuery(id+"F0.wireOp",EDGE,"E21"),sQuery(id+"F0.wireOp",EDGE,"E22"),sQuery(id+"F0.wireOp",EDGE,"E23"),sQuery(id+"F0.wireOp",EDGE,"E24"),sQuery(id+"F0.wireOp",EDGE,"E25"),sQuery(id+"F0.wireOp",EDGE,"E26"),sQuery(id+"F0.wireOp",EDGE,"E27"),sQuery(id+"F0.wireOp",EDGE,"E28"),sQuery(id+"F0.wireOp",EDGE,"E29"),sQuery(id+"F0.wireOp",EDGE,"E30"),sQuery(id+"F0.wireOp",EDGE,"E31"),sQuery(id+"F0.wireOp",EDGE,"E32"),sQuery(id+"F0.wireOp",EDGE,"E33"),sQuery(id+"F0.wireOp",EDGE,"E34"),sQuery(id+"F0.wireOp",EDGE,"E35"),sQuery(id+"F0.wireOp",EDGE,"E36"),sQuery(id+"F0.wireOp",EDGE,"E37"),sQuery(id+"F0.wireOp",EDGE,"E38"),sQuery(id+"F0.wireOp",EDGE,"E39"),sQuery(id+"F0.wireOp",EDGE,"E40"),sQuery(id+"F0.wireOp",EDGE,"E41"),sQuery(id+"F0.wireOp",EDGE,"E42"),sQuery(id+"F0.wireOp",EDGE,"E43"),sQuery(id+"F0.wireOp",EDGE,"E44"),sQuery(id+"F0.wireOp",EDGE,"E45"),sQuery(id+"F0.wireOp",EDGE,"E46"),sQuery(id+"F0.wireOp",EDGE,"E47"),sQuery(id+"F0.wireOp",EDGE,"E48"),sQuery(id+"F0.wireOp",EDGE,"E49"),sQuery(id+"F0.wireOp",EDGE,"E50"),sQuery(id+"F0.wireOp",EDGE,"E51"),sQuery(id+"F0.wireOp",EDGE,"E52"),sQuery(id+"F0.wireOp",EDGE,"E53"),sQuery(id+"F0.wireOp",EDGE,"E54"),sQuery(id+"F0.wireOp",EDGE,"E55"),sQuery(id+"F0.wireOp",EDGE,"E56"),sQuery(id+"F0.wireOp",EDGE,"E57"),sQuery(id+"F0.wireOp",EDGE,"E58"),sQuery(id+"F0.wireOp",EDGE,"E59"),sQuery(id+"F0.wireOp",EDGE,"E60"),sQuery(id+"F0.wireOp",EDGE,"E61"),sQuery(id+"F0.wireOp",EDGE,"E62"),sQuery(id+"F0.wireOp",EDGE,"E63"),sQuery(id+"F0.wireOp",EDGE,"E64"),sQuery(id+"F0.wireOp",EDGE,"E65"),sQuery(id+"F0.wireOp",EDGE,"E66"),sQuery(id+"F0.wireOp",EDGE,"E67"),sQuery(id+"F0.wireOp",EDGE,"E68"),sQuery(id+"F0.wireOp",EDGE,"E69"),sQuery(id+"F0.wireOp",EDGE,"E70"),sQuery(id+"F0.wireOp",EDGE,"E71"),sQuery(id+"F0.wireOp",EDGE,"E72"),sQuery(id+"F0.wireOp",EDGE,"E73"),sQuery(id+"F0.wireOp",EDGE,"E74"),sQuery(id+"F0.wireOp",EDGE,"E75"),sQuery(id+"F0.wireOp",EDGE,"E76"),sQuery(id+"F0.wireOp",EDGE,"E77"),sQuery(id+"F0.wireOp",EDGE,"E78"),sQuery(id+"F0.wireOp",EDGE,"E79"),sQuery(id+"F0.wireOp",EDGE,"E80"),sQuery(id+"F0.wireOp",EDGE,"E81"),sQuery(id+"F0.wireOp",EDGE,"E82"),sQuery(id+"F0.wireOp",EDGE,"E83"),sQuery(id+"F0.wireOp",EDGE,"E84"),sQuery(id+"F0.wireOp",EDGE,"E85"),sQuery(id+"F0.wireOp",EDGE,"E86"),sQuery(id+"F0.wireOp",EDGE,"E87"),sQuery(id+"F0.wireOp",EDGE,"E88"),sQuery(id+"F0.wireOp",EDGE,"E89"),sQuery(id+"F0.wireOp",EDGE,"E90"),sQuery(id+"F0.wireOp",EDGE,"E91"),sQuery(id+"F0.wireOp",EDGE,"E92"),sQuery(id+"F0.wireOp",EDGE,"E93"),sQuery(id+"F0.wireOp",EDGE,"E94"),sQuery(id+"F0.wireOp",EDGE,"E95"),sQuery(id+"F0.wireOp",EDGE,"E96"),sQuery(id+"F0.wireOp",EDGE,"E97"),sQuery(id+"F0.wireOp",EDGE,"E98"),sQuery(id+"F0.wireOp",EDGE,"E99"),sQuery(id+"F0.wireOp",EDGE,"E100"),sQuery(id+"F0.wireOp",EDGE,"E101"),sQuery(id+"F0.wireOp",EDGE,"E102"),sQuery(id+"F0.wireOp",EDGE,"E103"),sQuery(id+"F0.wireOp",EDGE,"E104")])]}),"instanceName":"12"});
            var Q4;
            Q4=makeQuery(id+"F2.opPattern","COPY",BODY,{"derivedFrom":makeQuery(id+"F1.opExtrude","SWEPT_BODY",BODY,{"disambiguationData":[OSD([sQuery(id+"F0.wireOp",EDGE,"E1"),sQuery(id+"F0.wireOp",EDGE,"E2"),sQuery(id+"F0.wireOp",EDGE,"E3"),sQuery(id+"F0.wireOp",EDGE,"E4"),sQuery(id+"F0.wireOp",EDGE,"E5"),sQuery(id+"F0.wireOp",EDGE,"E6"),sQuery(id+"F0.wireOp",EDGE,"E7"),sQuery(id+"F0.wireOp",EDGE,"E8"),sQuery(id+"F0.wireOp",EDGE,"E9"),sQuery(id+"F0.wireOp",EDGE,"E10"),sQuery(id+"F0.wireOp",EDGE,"E11"),sQuery(id+"F0.wireOp",EDGE,"E12"),sQuery(id+"F0.wireOp",EDGE,"E13"),sQuery(id+"F0.wireOp",EDGE,"E14"),sQuery(id+"F0.wireOp",EDGE,"E15"),sQuery(id+"F0.wireOp",EDGE,"E16"),sQuery(id+"F0.wireOp",EDGE,"E17"),sQuery(id+"F0.wireOp",EDGE,"E18"),sQuery(id+"F0.wireOp",EDGE,"E19"),sQuery(id+"F0.wireOp",EDGE,"E20"),sQuery(id+"F0.wireOp",EDGE,"E21"),sQuery(id+"F0.wireOp",EDGE,"E22"),sQuery(id+"F0.wireOp",EDGE,"E23"),sQuery(id+"F0.wireOp",EDGE,"E24"),sQuery(id+"F0.wireOp",EDGE,"E25"),sQuery(id+"F0.wireOp",EDGE,"E26"),sQuery(id+"F0.wireOp",EDGE,"E27"),sQuery(id+"F0.wireOp",EDGE,"E28"),sQuery(id+"F0.wireOp",EDGE,"E29"),sQuery(id+"F0.wireOp",EDGE,"E30"),sQuery(id+"F0.wireOp",EDGE,"E31"),sQuery(id+"F0.wireOp",EDGE,"E32"),sQuery(id+"F0.wireOp",EDGE,"E33"),sQuery(id+"F0.wireOp",EDGE,"E34"),sQuery(id+"F0.wireOp",EDGE,"E35"),sQuery(id+"F0.wireOp",EDGE,"E36"),sQuery(id+"F0.wireOp",EDGE,"E37"),sQuery(id+"F0.wireOp",EDGE,"E38"),sQuery(id+"F0.wireOp",EDGE,"E39"),sQuery(id+"F0.wireOp",EDGE,"E40"),sQuery(id+"F0.wireOp",EDGE,"E41"),sQuery(id+"F0.wireOp",EDGE,"E42"),sQuery(id+"F0.wireOp",EDGE,"E43"),sQuery(id+"F0.wireOp",EDGE,"E44"),sQuery(id+"F0.wireOp",EDGE,"E45"),sQuery(id+"F0.wireOp",EDGE,"E46"),sQuery(id+"F0.wireOp",EDGE,"E47"),sQuery(id+"F0.wireOp",EDGE,"E48"),sQuery(id+"F0.wireOp",EDGE,"E49"),sQuery(id+"F0.wireOp",EDGE,"E50"),sQuery(id+"F0.wireOp",EDGE,"E51"),sQuery(id+"F0.wireOp",EDGE,"E52"),sQuery(id+"F0.wireOp",EDGE,"E53"),sQuery(id+"F0.wireOp",EDGE,"E54"),sQuery(id+"F0.wireOp",EDGE,"E55"),sQuery(id+"F0.wireOp",EDGE,"E56"),sQuery(id+"F0.wireOp",EDGE,"E57"),sQuery(id+"F0.wireOp",EDGE,"E58"),sQuery(id+"F0.wireOp",EDGE,"E59"),sQuery(id+"F0.wireOp",EDGE,"E60"),sQuery(id+"F0.wireOp",EDGE,"E61"),sQuery(id+"F0.wireOp",EDGE,"E62"),sQuery(id+"F0.wireOp",EDGE,"E63"),sQuery(id+"F0.wireOp",EDGE,"E64"),sQuery(id+"F0.wireOp",EDGE,"E65"),sQuery(id+"F0.wireOp",EDGE,"E66"),sQuery(id+"F0.wireOp",EDGE,"E67"),sQuery(id+"F0.wireOp",EDGE,"E68"),sQuery(id+"F0.wireOp",EDGE,"E69"),sQuery(id+"F0.wireOp",EDGE,"E70"),sQuery(id+"F0.wireOp",EDGE,"E71"),sQuery(id+"F0.wireOp",EDGE,"E72"),sQuery(id+"F0.wireOp",EDGE,"E73"),sQuery(id+"F0.wireOp",EDGE,"E74"),sQuery(id+"F0.wireOp",EDGE,"E75"),sQuery(id+"F0.wireOp",EDGE,"E76"),sQuery(id+"F0.wireOp",EDGE,"E77"),sQuery(id+"F0.wireOp",EDGE,"E78"),sQuery(id+"F0.wireOp",EDGE,"E79"),sQuery(id+"F0.wireOp",EDGE,"E80"),sQuery(id+"F0.wireOp",EDGE,"E81"),sQuery(id+"F0.wireOp",EDGE,"E82"),sQuery(id+"F0.wireOp",EDGE,"E83"),sQuery(id+"F0.wireOp",EDGE,"E84"),sQuery(id+"F0.wireOp",EDGE,"E85"),sQuery(id+"F0.wireOp",EDGE,"E86"),sQuery(id+"F0.wireOp",EDGE,"E87"),sQuery(id+"F0.wireOp",EDGE,"E88"),sQuery(id+"F0.wireOp",EDGE,"E89"),sQuery(id+"F0.wireOp",EDGE,"E90"),sQuery(id+"F0.wireOp",EDGE,"E91"),sQuery(id+"F0.wireOp",EDGE,"E92"),sQuery(id+"F0.wireOp",EDGE,"E93"),sQuery(id+"F0.wireOp",EDGE,"E94"),sQuery(id+"F0.wireOp",EDGE,"E95"),sQuery(id+"F0.wireOp",EDGE,"E96"),sQuery(id+"F0.wireOp",EDGE,"E97"),sQuery(id+"F0.wireOp",EDGE,"E98"),sQuery(id+"F0.wireOp",EDGE,"E99"),sQuery(id+"F0.wireOp",EDGE,"E100"),sQuery(id+"F0.wireOp",EDGE,"E101"),sQuery(id+"F0.wireOp",EDGE,"E102"),sQuery(id+"F0.wireOp",EDGE,"E103"),sQuery(id+"F0.wireOp",EDGE,"E104")])]}),"instanceName":"13"});
            var Q5;
            Q5=makeQuery(id+"F2.opPattern","COPY",BODY,{"derivedFrom":makeQuery(id+"F1.opExtrude","SWEPT_BODY",BODY,{"disambiguationData":[OSD([sQuery(id+"F0.wireOp",EDGE,"E1"),sQuery(id+"F0.wireOp",EDGE,"E2"),sQuery(id+"F0.wireOp",EDGE,"E3"),sQuery(id+"F0.wireOp",EDGE,"E4"),sQuery(id+"F0.wireOp",EDGE,"E5"),sQuery(id+"F0.wireOp",EDGE,"E6"),sQuery(id+"F0.wireOp",EDGE,"E7"),sQuery(id+"F0.wireOp",EDGE,"E8"),sQuery(id+"F0.wireOp",EDGE,"E9"),sQuery(id+"F0.wireOp",EDGE,"E10"),sQuery(id+"F0.wireOp",EDGE,"E11"),sQuery(id+"F0.wireOp",EDGE,"E12"),sQuery(id+"F0.wireOp",EDGE,"E13"),sQuery(id+"F0.wireOp",EDGE,"E14"),sQuery(id+"F0.wireOp",EDGE,"E15"),sQuery(id+"F0.wireOp",EDGE,"E16"),sQuery(id+"F0.wireOp",EDGE,"E17"),sQuery(id+"F0.wireOp",EDGE,"E18"),sQuery(id+"F0.wireOp",EDGE,"E19"),sQuery(id+"F0.wireOp",EDGE,"E20"),sQuery(id+"F0.wireOp",EDGE,"E21"),sQuery(id+"F0.wireOp",EDGE,"E22"),sQuery(id+"F0.wireOp",EDGE,"E23"),sQuery(id+"F0.wireOp",EDGE,"E24"),sQuery(id+"F0.wireOp",EDGE,"E25"),sQuery(id+"F0.wireOp",EDGE,"E26"),sQuery(id+"F0.wireOp",EDGE,"E27"),sQuery(id+"F0.wireOp",EDGE,"E28"),sQuery(id+"F0.wireOp",EDGE,"E29"),sQuery(id+"F0.wireOp",EDGE,"E30"),sQuery(id+"F0.wireOp",EDGE,"E31"),sQuery(id+"F0.wireOp",EDGE,"E32"),sQuery(id+"F0.wireOp",EDGE,"E33"),sQuery(id+"F0.wireOp",EDGE,"E34"),sQuery(id+"F0.wireOp",EDGE,"E35"),sQuery(id+"F0.wireOp",EDGE,"E36"),sQuery(id+"F0.wireOp",EDGE,"E37"),sQuery(id+"F0.wireOp",EDGE,"E38"),sQuery(id+"F0.wireOp",EDGE,"E39"),sQuery(id+"F0.wireOp",EDGE,"E40"),sQuery(id+"F0.wireOp",EDGE,"E41"),sQuery(id+"F0.wireOp",EDGE,"E42"),sQuery(id+"F0.wireOp",EDGE,"E43"),sQuery(id+"F0.wireOp",EDGE,"E44"),sQuery(id+"F0.wireOp",EDGE,"E45"),sQuery(id+"F0.wireOp",EDGE,"E46"),sQuery(id+"F0.wireOp",EDGE,"E47"),sQuery(id+"F0.wireOp",EDGE,"E48"),sQuery(id+"F0.wireOp",EDGE,"E49"),sQuery(id+"F0.wireOp",EDGE,"E50"),sQuery(id+"F0.wireOp",EDGE,"E51"),sQuery(id+"F0.wireOp",EDGE,"E52"),sQuery(id+"F0.wireOp",EDGE,"E53"),sQuery(id+"F0.wireOp",EDGE,"E54"),sQuery(id+"F0.wireOp",EDGE,"E55"),sQuery(id+"F0.wireOp",EDGE,"E56"),sQuery(id+"F0.wireOp",EDGE,"E57"),sQuery(id+"F0.wireOp",EDGE,"E58"),sQuery(id+"F0.wireOp",EDGE,"E59"),sQuery(id+"F0.wireOp",EDGE,"E60"),sQuery(id+"F0.wireOp",EDGE,"E61"),sQuery(id+"F0.wireOp",EDGE,"E62"),sQuery(id+"F0.wireOp",EDGE,"E63"),sQuery(id+"F0.wireOp",EDGE,"E64"),sQuery(id+"F0.wireOp",EDGE,"E65"),sQuery(id+"F0.wireOp",EDGE,"E66"),sQuery(id+"F0.wireOp",EDGE,"E67"),sQuery(id+"F0.wireOp",EDGE,"E68"),sQuery(id+"F0.wireOp",EDGE,"E69"),sQuery(id+"F0.wireOp",EDGE,"E70"),sQuery(id+"F0.wireOp",EDGE,"E71"),sQuery(id+"F0.wireOp",EDGE,"E72"),sQuery(id+"F0.wireOp",EDGE,"E73"),sQuery(id+"F0.wireOp",EDGE,"E74"),sQuery(id+"F0.wireOp",EDGE,"E75"),sQuery(id+"F0.wireOp",EDGE,"E76"),sQuery(id+"F0.wireOp",EDGE,"E77"),sQuery(id+"F0.wireOp",EDGE,"E78"),sQuery(id+"F0.wireOp",EDGE,"E79"),sQuery(id+"F0.wireOp",EDGE,"E80"),sQuery(id+"F0.wireOp",EDGE,"E81"),sQuery(id+"F0.wireOp",EDGE,"E82"),sQuery(id+"F0.wireOp",EDGE,"E83"),sQuery(id+"F0.wireOp",EDGE,"E84"),sQuery(id+"F0.wireOp",EDGE,"E85"),sQuery(id+"F0.wireOp",EDGE,"E86"),sQuery(id+"F0.wireOp",EDGE,"E87"),sQuery(id+"F0.wireOp",EDGE,"E88"),sQuery(id+"F0.wireOp",EDGE,"E89"),sQuery(id+"F0.wireOp",EDGE,"E90"),sQuery(id+"F0.wireOp",EDGE,"E91"),sQuery(id+"F0.wireOp",EDGE,"E92"),sQuery(id+"F0.wireOp",EDGE,"E93"),sQuery(id+"F0.wireOp",EDGE,"E94"),sQuery(id+"F0.wireOp",EDGE,"E95"),sQuery(id+"F0.wireOp",EDGE,"E96"),sQuery(id+"F0.wireOp",EDGE,"E97"),sQuery(id+"F0.wireOp",EDGE,"E98"),sQuery(id+"F0.wireOp",EDGE,"E99"),sQuery(id+"F0.wireOp",EDGE,"E100"),sQuery(id+"F0.wireOp",EDGE,"E101"),sQuery(id+"F0.wireOp",EDGE,"E102"),sQuery(id+"F0.wireOp",EDGE,"E103"),sQuery(id+"F0.wireOp",EDGE,"E104")])]}),"instanceName":"14"});
            var Q6;
            Q6=makeQuery(id+"F2.opPattern","COPY",BODY,{"derivedFrom":makeQuery(id+"F1.opExtrude","SWEPT_BODY",BODY,{"disambiguationData":[OSD([sQuery(id+"F0.wireOp",EDGE,"E1"),sQuery(id+"F0.wireOp",EDGE,"E2"),sQuery(id+"F0.wireOp",EDGE,"E3"),sQuery(id+"F0.wireOp",EDGE,"E4"),sQuery(id+"F0.wireOp",EDGE,"E5"),sQuery(id+"F0.wireOp",EDGE,"E6"),sQuery(id+"F0.wireOp",EDGE,"E7"),sQuery(id+"F0.wireOp",EDGE,"E8"),sQuery(id+"F0.wireOp",EDGE,"E9"),sQuery(id+"F0.wireOp",EDGE,"E10"),sQuery(id+"F0.wireOp",EDGE,"E11"),sQuery(id+"F0.wireOp",EDGE,"E12"),sQuery(id+"F0.wireOp",EDGE,"E13"),sQuery(id+"F0.wireOp",EDGE,"E14"),sQuery(id+"F0.wireOp",EDGE,"E15"),sQuery(id+"F0.wireOp",EDGE,"E16"),sQuery(id+"F0.wireOp",EDGE,"E17"),sQuery(id+"F0.wireOp",EDGE,"E18"),sQuery(id+"F0.wireOp",EDGE,"E19"),sQuery(id+"F0.wireOp",EDGE,"E20"),sQuery(id+"F0.wireOp",EDGE,"E21"),sQuery(id+"F0.wireOp",EDGE,"E22"),sQuery(id+"F0.wireOp",EDGE,"E23"),sQuery(id+"F0.wireOp",EDGE,"E24"),sQuery(id+"F0.wireOp",EDGE,"E25"),sQuery(id+"F0.wireOp",EDGE,"E26"),sQuery(id+"F0.wireOp",EDGE,"E27"),sQuery(id+"F0.wireOp",EDGE,"E28"),sQuery(id+"F0.wireOp",EDGE,"E29"),sQuery(id+"F0.wireOp",EDGE,"E30"),sQuery(id+"F0.wireOp",EDGE,"E31"),sQuery(id+"F0.wireOp",EDGE,"E32"),sQuery(id+"F0.wireOp",EDGE,"E33"),sQuery(id+"F0.wireOp",EDGE,"E34"),sQuery(id+"F0.wireOp",EDGE,"E35"),sQuery(id+"F0.wireOp",EDGE,"E36"),sQuery(id+"F0.wireOp",EDGE,"E37"),sQuery(id+"F0.wireOp",EDGE,"E38"),sQuery(id+"F0.wireOp",EDGE,"E39"),sQuery(id+"F0.wireOp",EDGE,"E40"),sQuery(id+"F0.wireOp",EDGE,"E41"),sQuery(id+"F0.wireOp",EDGE,"E42"),sQuery(id+"F0.wireOp",EDGE,"E43"),sQuery(id+"F0.wireOp",EDGE,"E44"),sQuery(id+"F0.wireOp",EDGE,"E45"),sQuery(id+"F0.wireOp",EDGE,"E46"),sQuery(id+"F0.wireOp",EDGE,"E47"),sQuery(id+"F0.wireOp",EDGE,"E48"),sQuery(id+"F0.wireOp",EDGE,"E49"),sQuery(id+"F0.wireOp",EDGE,"E50"),sQuery(id+"F0.wireOp",EDGE,"E51"),sQuery(id+"F0.wireOp",EDGE,"E52"),sQuery(id+"F0.wireOp",EDGE,"E53"),sQuery(id+"F0.wireOp",EDGE,"E54"),sQuery(id+"F0.wireOp",EDGE,"E55"),sQuery(id+"F0.wireOp",EDGE,"E56"),sQuery(id+"F0.wireOp",EDGE,"E57"),sQuery(id+"F0.wireOp",EDGE,"E58"),sQuery(id+"F0.wireOp",EDGE,"E59"),sQuery(id+"F0.wireOp",EDGE,"E60"),sQuery(id+"F0.wireOp",EDGE,"E61"),sQuery(id+"F0.wireOp",EDGE,"E62"),sQuery(id+"F0.wireOp",EDGE,"E63"),sQuery(id+"F0.wireOp",EDGE,"E64"),sQuery(id+"F0.wireOp",EDGE,"E65"),sQuery(id+"F0.wireOp",EDGE,"E66"),sQuery(id+"F0.wireOp",EDGE,"E67"),sQuery(id+"F0.wireOp",EDGE,"E68"),sQuery(id+"F0.wireOp",EDGE,"E69"),sQuery(id+"F0.wireOp",EDGE,"E70"),sQuery(id+"F0.wireOp",EDGE,"E71"),sQuery(id+"F0.wireOp",EDGE,"E72"),sQuery(id+"F0.wireOp",EDGE,"E73"),sQuery(id+"F0.wireOp",EDGE,"E74"),sQuery(id+"F0.wireOp",EDGE,"E75"),sQuery(id+"F0.wireOp",EDGE,"E76"),sQuery(id+"F0.wireOp",EDGE,"E77"),sQuery(id+"F0.wireOp",EDGE,"E78"),sQuery(id+"F0.wireOp",EDGE,"E79"),sQuery(id+"F0.wireOp",EDGE,"E80"),sQuery(id+"F0.wireOp",EDGE,"E81"),sQuery(id+"F0.wireOp",EDGE,"E82"),sQuery(id+"F0.wireOp",EDGE,"E83"),sQuery(id+"F0.wireOp",EDGE,"E84"),sQuery(id+"F0.wireOp",EDGE,"E85"),sQuery(id+"F0.wireOp",EDGE,"E86"),sQuery(id+"F0.wireOp",EDGE,"E87"),sQuery(id+"F0.wireOp",EDGE,"E88"),sQuery(id+"F0.wireOp",EDGE,"E89"),sQuery(id+"F0.wireOp",EDGE,"E90"),sQuery(id+"F0.wireOp",EDGE,"E91"),sQuery(id+"F0.wireOp",EDGE,"E92"),sQuery(id+"F0.wireOp",EDGE,"E93"),sQuery(id+"F0.wireOp",EDGE,"E94"),sQuery(id+"F0.wireOp",EDGE,"E95"),sQuery(id+"F0.wireOp",EDGE,"E96"),sQuery(id+"F0.wireOp",EDGE,"E97"),sQuery(id+"F0.wireOp",EDGE,"E98"),sQuery(id+"F0.wireOp",EDGE,"E99"),sQuery(id+"F0.wireOp",EDGE,"E100"),sQuery(id+"F0.wireOp",EDGE,"E101"),sQuery(id+"F0.wireOp",EDGE,"E102"),sQuery(id+"F0.wireOp",EDGE,"E103"),sQuery(id+"F0.wireOp",EDGE,"E104")])]}),"instanceName":"15"});
            var Q7;
            Q7=makeQuery(id+"F2.opPattern","COPY",BODY,{"derivedFrom":makeQuery(id+"F1.opExtrude","SWEPT_BODY",BODY,{"disambiguationData":[OSD([sQuery(id+"F0.wireOp",EDGE,"E1"),sQuery(id+"F0.wireOp",EDGE,"E2"),sQuery(id+"F0.wireOp",EDGE,"E3"),sQuery(id+"F0.wireOp",EDGE,"E4"),sQuery(id+"F0.wireOp",EDGE,"E5"),sQuery(id+"F0.wireOp",EDGE,"E6"),sQuery(id+"F0.wireOp",EDGE,"E7"),sQuery(id+"F0.wireOp",EDGE,"E8"),sQuery(id+"F0.wireOp",EDGE,"E9"),sQuery(id+"F0.wireOp",EDGE,"E10"),sQuery(id+"F0.wireOp",EDGE,"E11"),sQuery(id+"F0.wireOp",EDGE,"E12"),sQuery(id+"F0.wireOp",EDGE,"E13"),sQuery(id+"F0.wireOp",EDGE,"E14"),sQuery(id+"F0.wireOp",EDGE,"E15"),sQuery(id+"F0.wireOp",EDGE,"E16"),sQuery(id+"F0.wireOp",EDGE,"E17"),sQuery(id+"F0.wireOp",EDGE,"E18"),sQuery(id+"F0.wireOp",EDGE,"E19"),sQuery(id+"F0.wireOp",EDGE,"E20"),sQuery(id+"F0.wireOp",EDGE,"E21"),sQuery(id+"F0.wireOp",EDGE,"E22"),sQuery(id+"F0.wireOp",EDGE,"E23"),sQuery(id+"F0.wireOp",EDGE,"E24"),sQuery(id+"F0.wireOp",EDGE,"E25"),sQuery(id+"F0.wireOp",EDGE,"E26"),sQuery(id+"F0.wireOp",EDGE,"E27"),sQuery(id+"F0.wireOp",EDGE,"E28"),sQuery(id+"F0.wireOp",EDGE,"E29"),sQuery(id+"F0.wireOp",EDGE,"E30"),sQuery(id+"F0.wireOp",EDGE,"E31"),sQuery(id+"F0.wireOp",EDGE,"E32"),sQuery(id+"F0.wireOp",EDGE,"E33"),sQuery(id+"F0.wireOp",EDGE,"E34"),sQuery(id+"F0.wireOp",EDGE,"E35"),sQuery(id+"F0.wireOp",EDGE,"E36"),sQuery(id+"F0.wireOp",EDGE,"E37"),sQuery(id+"F0.wireOp",EDGE,"E38"),sQuery(id+"F0.wireOp",EDGE,"E39"),sQuery(id+"F0.wireOp",EDGE,"E40"),sQuery(id+"F0.wireOp",EDGE,"E41"),sQuery(id+"F0.wireOp",EDGE,"E42"),sQuery(id+"F0.wireOp",EDGE,"E43"),sQuery(id+"F0.wireOp",EDGE,"E44"),sQuery(id+"F0.wireOp",EDGE,"E45"),sQuery(id+"F0.wireOp",EDGE,"E46"),sQuery(id+"F0.wireOp",EDGE,"E47"),sQuery(id+"F0.wireOp",EDGE,"E48"),sQuery(id+"F0.wireOp",EDGE,"E49"),sQuery(id+"F0.wireOp",EDGE,"E50"),sQuery(id+"F0.wireOp",EDGE,"E51"),sQuery(id+"F0.wireOp",EDGE,"E52"),sQuery(id+"F0.wireOp",EDGE,"E53"),sQuery(id+"F0.wireOp",EDGE,"E54"),sQuery(id+"F0.wireOp",EDGE,"E55"),sQuery(id+"F0.wireOp",EDGE,"E56"),sQuery(id+"F0.wireOp",EDGE,"E57"),sQuery(id+"F0.wireOp",EDGE,"E58"),sQuery(id+"F0.wireOp",EDGE,"E59"),sQuery(id+"F0.wireOp",EDGE,"E60"),sQuery(id+"F0.wireOp",EDGE,"E61"),sQuery(id+"F0.wireOp",EDGE,"E62"),sQuery(id+"F0.wireOp",EDGE,"E63"),sQuery(id+"F0.wireOp",EDGE,"E64"),sQuery(id+"F0.wireOp",EDGE,"E65"),sQuery(id+"F0.wireOp",EDGE,"E66"),sQuery(id+"F0.wireOp",EDGE,"E67"),sQuery(id+"F0.wireOp",EDGE,"E68"),sQuery(id+"F0.wireOp",EDGE,"E69"),sQuery(id+"F0.wireOp",EDGE,"E70"),sQuery(id+"F0.wireOp",EDGE,"E71"),sQuery(id+"F0.wireOp",EDGE,"E72"),sQuery(id+"F0.wireOp",EDGE,"E73"),sQuery(id+"F0.wireOp",EDGE,"E74"),sQuery(id+"F0.wireOp",EDGE,"E75"),sQuery(id+"F0.wireOp",EDGE,"E76"),sQuery(id+"F0.wireOp",EDGE,"E77"),sQuery(id+"F0.wireOp",EDGE,"E78"),sQuery(id+"F0.wireOp",EDGE,"E79"),sQuery(id+"F0.wireOp",EDGE,"E80"),sQuery(id+"F0.wireOp",EDGE,"E81"),sQuery(id+"F0.wireOp",EDGE,"E82"),sQuery(id+"F0.wireOp",EDGE,"E83"),sQuery(id+"F0.wireOp",EDGE,"E84"),sQuery(id+"F0.wireOp",EDGE,"E85"),sQuery(id+"F0.wireOp",EDGE,"E86"),sQuery(id+"F0.wireOp",EDGE,"E87"),sQuery(id+"F0.wireOp",EDGE,"E88"),sQuery(id+"F0.wireOp",EDGE,"E89"),sQuery(id+"F0.wireOp",EDGE,"E90"),sQuery(id+"F0.wireOp",EDGE,"E91"),sQuery(id+"F0.wireOp",EDGE,"E92"),sQuery(id+"F0.wireOp",EDGE,"E93"),sQuery(id+"F0.wireOp",EDGE,"E94"),sQuery(id+"F0.wireOp",EDGE,"E95"),sQuery(id+"F0.wireOp",EDGE,"E96"),sQuery(id+"F0.wireOp",EDGE,"E97"),sQuery(id+"F0.wireOp",EDGE,"E98"),sQuery(id+"F0.wireOp",EDGE,"E99"),sQuery(id+"F0.wireOp",EDGE,"E100"),sQuery(id+"F0.wireOp",EDGE,"E101"),sQuery(id+"F0.wireOp",EDGE,"E102"),sQuery(id+"F0.wireOp",EDGE,"E103"),sQuery(id+"F0.wireOp",EDGE,"E104")])]}),"instanceName":"16"});
            var Q8;
            Q8=makeQuery(id+"F2.opPattern","COPY",BODY,{"derivedFrom":makeQuery(id+"F1.opExtrude","SWEPT_BODY",BODY,{"disambiguationData":[OSD([sQuery(id+"F0.wireOp",EDGE,"E1"),sQuery(id+"F0.wireOp",EDGE,"E2"),sQuery(id+"F0.wireOp",EDGE,"E3"),sQuery(id+"F0.wireOp",EDGE,"E4"),sQuery(id+"F0.wireOp",EDGE,"E5"),sQuery(id+"F0.wireOp",EDGE,"E6"),sQuery(id+"F0.wireOp",EDGE,"E7"),sQuery(id+"F0.wireOp",EDGE,"E8"),sQuery(id+"F0.wireOp",EDGE,"E9"),sQuery(id+"F0.wireOp",EDGE,"E10"),sQuery(id+"F0.wireOp",EDGE,"E11"),sQuery(id+"F0.wireOp",EDGE,"E12"),sQuery(id+"F0.wireOp",EDGE,"E13"),sQuery(id+"F0.wireOp",EDGE,"E14"),sQuery(id+"F0.wireOp",EDGE,"E15"),sQuery(id+"F0.wireOp",EDGE,"E16"),sQuery(id+"F0.wireOp",EDGE,"E17"),sQuery(id+"F0.wireOp",EDGE,"E18"),sQuery(id+"F0.wireOp",EDGE,"E19"),sQuery(id+"F0.wireOp",EDGE,"E20"),sQuery(id+"F0.wireOp",EDGE,"E21"),sQuery(id+"F0.wireOp",EDGE,"E22"),sQuery(id+"F0.wireOp",EDGE,"E23"),sQuery(id+"F0.wireOp",EDGE,"E24"),sQuery(id+"F0.wireOp",EDGE,"E25"),sQuery(id+"F0.wireOp",EDGE,"E26"),sQuery(id+"F0.wireOp",EDGE,"E27"),sQuery(id+"F0.wireOp",EDGE,"E28"),sQuery(id+"F0.wireOp",EDGE,"E29"),sQuery(id+"F0.wireOp",EDGE,"E30"),sQuery(id+"F0.wireOp",EDGE,"E31"),sQuery(id+"F0.wireOp",EDGE,"E32"),sQuery(id+"F0.wireOp",EDGE,"E33"),sQuery(id+"F0.wireOp",EDGE,"E34"),sQuery(id+"F0.wireOp",EDGE,"E35"),sQuery(id+"F0.wireOp",EDGE,"E36"),sQuery(id+"F0.wireOp",EDGE,"E37"),sQuery(id+"F0.wireOp",EDGE,"E38"),sQuery(id+"F0.wireOp",EDGE,"E39"),sQuery(id+"F0.wireOp",EDGE,"E40"),sQuery(id+"F0.wireOp",EDGE,"E41"),sQuery(id+"F0.wireOp",EDGE,"E42"),sQuery(id+"F0.wireOp",EDGE,"E43"),sQuery(id+"F0.wireOp",EDGE,"E44"),sQuery(id+"F0.wireOp",EDGE,"E45"),sQuery(id+"F0.wireOp",EDGE,"E46"),sQuery(id+"F0.wireOp",EDGE,"E47"),sQuery(id+"F0.wireOp",EDGE,"E48"),sQuery(id+"F0.wireOp",EDGE,"E49"),sQuery(id+"F0.wireOp",EDGE,"E50"),sQuery(id+"F0.wireOp",EDGE,"E51"),sQuery(id+"F0.wireOp",EDGE,"E52"),sQuery(id+"F0.wireOp",EDGE,"E53"),sQuery(id+"F0.wireOp",EDGE,"E54"),sQuery(id+"F0.wireOp",EDGE,"E55"),sQuery(id+"F0.wireOp",EDGE,"E56"),sQuery(id+"F0.wireOp",EDGE,"E57"),sQuery(id+"F0.wireOp",EDGE,"E58"),sQuery(id+"F0.wireOp",EDGE,"E59"),sQuery(id+"F0.wireOp",EDGE,"E60"),sQuery(id+"F0.wireOp",EDGE,"E61"),sQuery(id+"F0.wireOp",EDGE,"E62"),sQuery(id+"F0.wireOp",EDGE,"E63"),sQuery(id+"F0.wireOp",EDGE,"E64"),sQuery(id+"F0.wireOp",EDGE,"E65"),sQuery(id+"F0.wireOp",EDGE,"E66"),sQuery(id+"F0.wireOp",EDGE,"E67"),sQuery(id+"F0.wireOp",EDGE,"E68"),sQuery(id+"F0.wireOp",EDGE,"E69"),sQuery(id+"F0.wireOp",EDGE,"E70"),sQuery(id+"F0.wireOp",EDGE,"E71"),sQuery(id+"F0.wireOp",EDGE,"E72"),sQuery(id+"F0.wireOp",EDGE,"E73"),sQuery(id+"F0.wireOp",EDGE,"E74"),sQuery(id+"F0.wireOp",EDGE,"E75"),sQuery(id+"F0.wireOp",EDGE,"E76"),sQuery(id+"F0.wireOp",EDGE,"E77"),sQuery(id+"F0.wireOp",EDGE,"E78"),sQuery(id+"F0.wireOp",EDGE,"E79"),sQuery(id+"F0.wireOp",EDGE,"E80"),sQuery(id+"F0.wireOp",EDGE,"E81"),sQuery(id+"F0.wireOp",EDGE,"E82"),sQuery(id+"F0.wireOp",EDGE,"E83"),sQuery(id+"F0.wireOp",EDGE,"E84"),sQuery(id+"F0.wireOp",EDGE,"E85"),sQuery(id+"F0.wireOp",EDGE,"E86"),sQuery(id+"F0.wireOp",EDGE,"E87"),sQuery(id+"F0.wireOp",EDGE,"E88"),sQuery(id+"F0.wireOp",EDGE,"E89"),sQuery(id+"F0.wireOp",EDGE,"E90"),sQuery(id+"F0.wireOp",EDGE,"E91"),sQuery(id+"F0.wireOp",EDGE,"E92"),sQuery(id+"F0.wireOp",EDGE,"E93"),sQuery(id+"F0.wireOp",EDGE,"E94"),sQuery(id+"F0.wireOp",EDGE,"E95"),sQuery(id+"F0.wireOp",EDGE,"E96"),sQuery(id+"F0.wireOp",EDGE,"E97"),sQuery(id+"F0.wireOp",EDGE,"E98"),sQuery(id+"F0.wireOp",EDGE,"E99"),sQuery(id+"F0.wireOp",EDGE,"E100"),sQuery(id+"F0.wireOp",EDGE,"E101"),sQuery(id+"F0.wireOp",EDGE,"E102"),sQuery(id+"F0.wireOp",EDGE,"E103"),sQuery(id+"F0.wireOp",EDGE,"E104")])]}),"instanceName":"17"});
            var Q9;
            Q9=makeQuery(id+"F2.opPattern","COPY",BODY,{"derivedFrom":makeQuery(id+"F1.opExtrude","SWEPT_BODY",BODY,{"disambiguationData":[OSD([sQuery(id+"F0.wireOp",EDGE,"E1"),sQuery(id+"F0.wireOp",EDGE,"E2"),sQuery(id+"F0.wireOp",EDGE,"E3"),sQuery(id+"F0.wireOp",EDGE,"E4"),sQuery(id+"F0.wireOp",EDGE,"E5"),sQuery(id+"F0.wireOp",EDGE,"E6"),sQuery(id+"F0.wireOp",EDGE,"E7"),sQuery(id+"F0.wireOp",EDGE,"E8"),sQuery(id+"F0.wireOp",EDGE,"E9"),sQuery(id+"F0.wireOp",EDGE,"E10"),sQuery(id+"F0.wireOp",EDGE,"E11"),sQuery(id+"F0.wireOp",EDGE,"E12"),sQuery(id+"F0.wireOp",EDGE,"E13"),sQuery(id+"F0.wireOp",EDGE,"E14"),sQuery(id+"F0.wireOp",EDGE,"E15"),sQuery(id+"F0.wireOp",EDGE,"E16"),sQuery(id+"F0.wireOp",EDGE,"E17"),sQuery(id+"F0.wireOp",EDGE,"E18"),sQuery(id+"F0.wireOp",EDGE,"E19"),sQuery(id+"F0.wireOp",EDGE,"E20"),sQuery(id+"F0.wireOp",EDGE,"E21"),sQuery(id+"F0.wireOp",EDGE,"E22"),sQuery(id+"F0.wireOp",EDGE,"E23"),sQuery(id+"F0.wireOp",EDGE,"E24"),sQuery(id+"F0.wireOp",EDGE,"E25"),sQuery(id+"F0.wireOp",EDGE,"E26"),sQuery(id+"F0.wireOp",EDGE,"E27"),sQuery(id+"F0.wireOp",EDGE,"E28"),sQuery(id+"F0.wireOp",EDGE,"E29"),sQuery(id+"F0.wireOp",EDGE,"E30"),sQuery(id+"F0.wireOp",EDGE,"E31"),sQuery(id+"F0.wireOp",EDGE,"E32"),sQuery(id+"F0.wireOp",EDGE,"E33"),sQuery(id+"F0.wireOp",EDGE,"E34"),sQuery(id+"F0.wireOp",EDGE,"E35"),sQuery(id+"F0.wireOp",EDGE,"E36"),sQuery(id+"F0.wireOp",EDGE,"E37"),sQuery(id+"F0.wireOp",EDGE,"E38"),sQuery(id+"F0.wireOp",EDGE,"E39"),sQuery(id+"F0.wireOp",EDGE,"E40"),sQuery(id+"F0.wireOp",EDGE,"E41"),sQuery(id+"F0.wireOp",EDGE,"E42"),sQuery(id+"F0.wireOp",EDGE,"E43"),sQuery(id+"F0.wireOp",EDGE,"E44"),sQuery(id+"F0.wireOp",EDGE,"E45"),sQuery(id+"F0.wireOp",EDGE,"E46"),sQuery(id+"F0.wireOp",EDGE,"E47"),sQuery(id+"F0.wireOp",EDGE,"E48"),sQuery(id+"F0.wireOp",EDGE,"E49"),sQuery(id+"F0.wireOp",EDGE,"E50"),sQuery(id+"F0.wireOp",EDGE,"E51"),sQuery(id+"F0.wireOp",EDGE,"E52"),sQuery(id+"F0.wireOp",EDGE,"E53"),sQuery(id+"F0.wireOp",EDGE,"E54"),sQuery(id+"F0.wireOp",EDGE,"E55"),sQuery(id+"F0.wireOp",EDGE,"E56"),sQuery(id+"F0.wireOp",EDGE,"E57"),sQuery(id+"F0.wireOp",EDGE,"E58"),sQuery(id+"F0.wireOp",EDGE,"E59"),sQuery(id+"F0.wireOp",EDGE,"E60"),sQuery(id+"F0.wireOp",EDGE,"E61"),sQuery(id+"F0.wireOp",EDGE,"E62"),sQuery(id+"F0.wireOp",EDGE,"E63"),sQuery(id+"F0.wireOp",EDGE,"E64"),sQuery(id+"F0.wireOp",EDGE,"E65"),sQuery(id+"F0.wireOp",EDGE,"E66"),sQuery(id+"F0.wireOp",EDGE,"E67"),sQuery(id+"F0.wireOp",EDGE,"E68"),sQuery(id+"F0.wireOp",EDGE,"E69"),sQuery(id+"F0.wireOp",EDGE,"E70"),sQuery(id+"F0.wireOp",EDGE,"E71"),sQuery(id+"F0.wireOp",EDGE,"E72"),sQuery(id+"F0.wireOp",EDGE,"E73"),sQuery(id+"F0.wireOp",EDGE,"E74"),sQuery(id+"F0.wireOp",EDGE,"E75"),sQuery(id+"F0.wireOp",EDGE,"E76"),sQuery(id+"F0.wireOp",EDGE,"E77"),sQuery(id+"F0.wireOp",EDGE,"E78"),sQuery(id+"F0.wireOp",EDGE,"E79"),sQuery(id+"F0.wireOp",EDGE,"E80"),sQuery(id+"F0.wireOp",EDGE,"E81"),sQuery(id+"F0.wireOp",EDGE,"E82"),sQuery(id+"F0.wireOp",EDGE,"E83"),sQuery(id+"F0.wireOp",EDGE,"E84"),sQuery(id+"F0.wireOp",EDGE,"E85"),sQuery(id+"F0.wireOp",EDGE,"E86"),sQuery(id+"F0.wireOp",EDGE,"E87"),sQuery(id+"F0.wireOp",EDGE,"E88"),sQuery(id+"F0.wireOp",EDGE,"E89"),sQuery(id+"F0.wireOp",EDGE,"E90"),sQuery(id+"F0.wireOp",EDGE,"E91"),sQuery(id+"F0.wireOp",EDGE,"E92"),sQuery(id+"F0.wireOp",EDGE,"E93"),sQuery(id+"F0.wireOp",EDGE,"E94"),sQuery(id+"F0.wireOp",EDGE,"E95"),sQuery(id+"F0.wireOp",EDGE,"E96"),sQuery(id+"F0.wireOp",EDGE,"E97"),sQuery(id+"F0.wireOp",EDGE,"E98"),sQuery(id+"F0.wireOp",EDGE,"E99"),sQuery(id+"F0.wireOp",EDGE,"E100"),sQuery(id+"F0.wireOp",EDGE,"E101"),sQuery(id+"F0.wireOp",EDGE,"E102"),sQuery(id+"F0.wireOp",EDGE,"E103"),sQuery(id+"F0.wireOp",EDGE,"E104")])]}),"instanceName":"18"});
            var Q10;
            Q10=makeQuery(id+"F2.opPattern","COPY",BODY,{"derivedFrom":makeQuery(id+"F1.opExtrude","SWEPT_BODY",BODY,{"disambiguationData":[OSD([sQuery(id+"F0.wireOp",EDGE,"E1"),sQuery(id+"F0.wireOp",EDGE,"E2"),sQuery(id+"F0.wireOp",EDGE,"E3"),sQuery(id+"F0.wireOp",EDGE,"E4"),sQuery(id+"F0.wireOp",EDGE,"E5"),sQuery(id+"F0.wireOp",EDGE,"E6"),sQuery(id+"F0.wireOp",EDGE,"E7"),sQuery(id+"F0.wireOp",EDGE,"E8"),sQuery(id+"F0.wireOp",EDGE,"E9"),sQuery(id+"F0.wireOp",EDGE,"E10"),sQuery(id+"F0.wireOp",EDGE,"E11"),sQuery(id+"F0.wireOp",EDGE,"E12"),sQuery(id+"F0.wireOp",EDGE,"E13"),sQuery(id+"F0.wireOp",EDGE,"E14"),sQuery(id+"F0.wireOp",EDGE,"E15"),sQuery(id+"F0.wireOp",EDGE,"E16"),sQuery(id+"F0.wireOp",EDGE,"E17"),sQuery(id+"F0.wireOp",EDGE,"E18"),sQuery(id+"F0.wireOp",EDGE,"E19"),sQuery(id+"F0.wireOp",EDGE,"E20"),sQuery(id+"F0.wireOp",EDGE,"E21"),sQuery(id+"F0.wireOp",EDGE,"E22"),sQuery(id+"F0.wireOp",EDGE,"E23"),sQuery(id+"F0.wireOp",EDGE,"E24"),sQuery(id+"F0.wireOp",EDGE,"E25"),sQuery(id+"F0.wireOp",EDGE,"E26"),sQuery(id+"F0.wireOp",EDGE,"E27"),sQuery(id+"F0.wireOp",EDGE,"E28"),sQuery(id+"F0.wireOp",EDGE,"E29"),sQuery(id+"F0.wireOp",EDGE,"E30"),sQuery(id+"F0.wireOp",EDGE,"E31"),sQuery(id+"F0.wireOp",EDGE,"E32"),sQuery(id+"F0.wireOp",EDGE,"E33"),sQuery(id+"F0.wireOp",EDGE,"E34"),sQuery(id+"F0.wireOp",EDGE,"E35"),sQuery(id+"F0.wireOp",EDGE,"E36"),sQuery(id+"F0.wireOp",EDGE,"E37"),sQuery(id+"F0.wireOp",EDGE,"E38"),sQuery(id+"F0.wireOp",EDGE,"E39"),sQuery(id+"F0.wireOp",EDGE,"E40"),sQuery(id+"F0.wireOp",EDGE,"E41"),sQuery(id+"F0.wireOp",EDGE,"E42"),sQuery(id+"F0.wireOp",EDGE,"E43"),sQuery(id+"F0.wireOp",EDGE,"E44"),sQuery(id+"F0.wireOp",EDGE,"E45"),sQuery(id+"F0.wireOp",EDGE,"E46"),sQuery(id+"F0.wireOp",EDGE,"E47"),sQuery(id+"F0.wireOp",EDGE,"E48"),sQuery(id+"F0.wireOp",EDGE,"E49"),sQuery(id+"F0.wireOp",EDGE,"E50"),sQuery(id+"F0.wireOp",EDGE,"E51"),sQuery(id+"F0.wireOp",EDGE,"E52"),sQuery(id+"F0.wireOp",EDGE,"E53"),sQuery(id+"F0.wireOp",EDGE,"E54"),sQuery(id+"F0.wireOp",EDGE,"E55"),sQuery(id+"F0.wireOp",EDGE,"E56"),sQuery(id+"F0.wireOp",EDGE,"E57"),sQuery(id+"F0.wireOp",EDGE,"E58"),sQuery(id+"F0.wireOp",EDGE,"E59"),sQuery(id+"F0.wireOp",EDGE,"E60"),sQuery(id+"F0.wireOp",EDGE,"E61"),sQuery(id+"F0.wireOp",EDGE,"E62"),sQuery(id+"F0.wireOp",EDGE,"E63"),sQuery(id+"F0.wireOp",EDGE,"E64"),sQuery(id+"F0.wireOp",EDGE,"E65"),sQuery(id+"F0.wireOp",EDGE,"E66"),sQuery(id+"F0.wireOp",EDGE,"E67"),sQuery(id+"F0.wireOp",EDGE,"E68"),sQuery(id+"F0.wireOp",EDGE,"E69"),sQuery(id+"F0.wireOp",EDGE,"E70"),sQuery(id+"F0.wireOp",EDGE,"E71"),sQuery(id+"F0.wireOp",EDGE,"E72"),sQuery(id+"F0.wireOp",EDGE,"E73"),sQuery(id+"F0.wireOp",EDGE,"E74"),sQuery(id+"F0.wireOp",EDGE,"E75"),sQuery(id+"F0.wireOp",EDGE,"E76"),sQuery(id+"F0.wireOp",EDGE,"E77"),sQuery(id+"F0.wireOp",EDGE,"E78"),sQuery(id+"F0.wireOp",EDGE,"E79"),sQuery(id+"F0.wireOp",EDGE,"E80"),sQuery(id+"F0.wireOp",EDGE,"E81"),sQuery(id+"F0.wireOp",EDGE,"E82"),sQuery(id+"F0.wireOp",EDGE,"E83"),sQuery(id+"F0.wireOp",EDGE,"E84"),sQuery(id+"F0.wireOp",EDGE,"E85"),sQuery(id+"F0.wireOp",EDGE,"E86"),sQuery(id+"F0.wireOp",EDGE,"E87"),sQuery(id+"F0.wireOp",EDGE,"E88"),sQuery(id+"F0.wireOp",EDGE,"E89"),sQuery(id+"F0.wireOp",EDGE,"E90"),sQuery(id+"F0.wireOp",EDGE,"E91"),sQuery(id+"F0.wireOp",EDGE,"E92"),sQuery(id+"F0.wireOp",EDGE,"E93"),sQuery(id+"F0.wireOp",EDGE,"E94"),sQuery(id+"F0.wireOp",EDGE,"E95"),sQuery(id+"F0.wireOp",EDGE,"E96"),sQuery(id+"F0.wireOp",EDGE,"E97"),sQuery(id+"F0.wireOp",EDGE,"E98"),sQuery(id+"F0.wireOp",EDGE,"E99"),sQuery(id+"F0.wireOp",EDGE,"E100"),sQuery(id+"F0.wireOp",EDGE,"E101"),sQuery(id+"F0.wireOp",EDGE,"E102"),sQuery(id+"F0.wireOp",EDGE,"E103"),sQuery(id+"F0.wireOp",EDGE,"E104")])]}),"instanceName":"19"});
            var Q11;
            Q11=makeQuery(id+"F2.opPattern","COPY",BODY,{"derivedFrom":makeQuery(id+"F1.opExtrude","SWEPT_BODY",BODY,{"disambiguationData":[OSD([sQuery(id+"F0.wireOp",EDGE,"E1"),sQuery(id+"F0.wireOp",EDGE,"E2"),sQuery(id+"F0.wireOp",EDGE,"E3"),sQuery(id+"F0.wireOp",EDGE,"E4"),sQuery(id+"F0.wireOp",EDGE,"E5"),sQuery(id+"F0.wireOp",EDGE,"E6"),sQuery(id+"F0.wireOp",EDGE,"E7"),sQuery(id+"F0.wireOp",EDGE,"E8"),sQuery(id+"F0.wireOp",EDGE,"E9"),sQuery(id+"F0.wireOp",EDGE,"E10"),sQuery(id+"F0.wireOp",EDGE,"E11"),sQuery(id+"F0.wireOp",EDGE,"E12"),sQuery(id+"F0.wireOp",EDGE,"E13"),sQuery(id+"F0.wireOp",EDGE,"E14"),sQuery(id+"F0.wireOp",EDGE,"E15"),sQuery(id+"F0.wireOp",EDGE,"E16"),sQuery(id+"F0.wireOp",EDGE,"E17"),sQuery(id+"F0.wireOp",EDGE,"E18"),sQuery(id+"F0.wireOp",EDGE,"E19"),sQuery(id+"F0.wireOp",EDGE,"E20"),sQuery(id+"F0.wireOp",EDGE,"E21"),sQuery(id+"F0.wireOp",EDGE,"E22"),sQuery(id+"F0.wireOp",EDGE,"E23"),sQuery(id+"F0.wireOp",EDGE,"E24"),sQuery(id+"F0.wireOp",EDGE,"E25"),sQuery(id+"F0.wireOp",EDGE,"E26"),sQuery(id+"F0.wireOp",EDGE,"E27"),sQuery(id+"F0.wireOp",EDGE,"E28"),sQuery(id+"F0.wireOp",EDGE,"E29"),sQuery(id+"F0.wireOp",EDGE,"E30"),sQuery(id+"F0.wireOp",EDGE,"E31"),sQuery(id+"F0.wireOp",EDGE,"E32"),sQuery(id+"F0.wireOp",EDGE,"E33"),sQuery(id+"F0.wireOp",EDGE,"E34"),sQuery(id+"F0.wireOp",EDGE,"E35"),sQuery(id+"F0.wireOp",EDGE,"E36"),sQuery(id+"F0.wireOp",EDGE,"E37"),sQuery(id+"F0.wireOp",EDGE,"E38"),sQuery(id+"F0.wireOp",EDGE,"E39"),sQuery(id+"F0.wireOp",EDGE,"E40"),sQuery(id+"F0.wireOp",EDGE,"E41"),sQuery(id+"F0.wireOp",EDGE,"E42"),sQuery(id+"F0.wireOp",EDGE,"E43"),sQuery(id+"F0.wireOp",EDGE,"E44"),sQuery(id+"F0.wireOp",EDGE,"E45"),sQuery(id+"F0.wireOp",EDGE,"E46"),sQuery(id+"F0.wireOp",EDGE,"E47"),sQuery(id+"F0.wireOp",EDGE,"E48"),sQuery(id+"F0.wireOp",EDGE,"E49"),sQuery(id+"F0.wireOp",EDGE,"E50"),sQuery(id+"F0.wireOp",EDGE,"E51"),sQuery(id+"F0.wireOp",EDGE,"E52"),sQuery(id+"F0.wireOp",EDGE,"E53"),sQuery(id+"F0.wireOp",EDGE,"E54"),sQuery(id+"F0.wireOp",EDGE,"E55"),sQuery(id+"F0.wireOp",EDGE,"E56"),sQuery(id+"F0.wireOp",EDGE,"E57"),sQuery(id+"F0.wireOp",EDGE,"E58"),sQuery(id+"F0.wireOp",EDGE,"E59"),sQuery(id+"F0.wireOp",EDGE,"E60"),sQuery(id+"F0.wireOp",EDGE,"E61"),sQuery(id+"F0.wireOp",EDGE,"E62"),sQuery(id+"F0.wireOp",EDGE,"E63"),sQuery(id+"F0.wireOp",EDGE,"E64"),sQuery(id+"F0.wireOp",EDGE,"E65"),sQuery(id+"F0.wireOp",EDGE,"E66"),sQuery(id+"F0.wireOp",EDGE,"E67"),sQuery(id+"F0.wireOp",EDGE,"E68"),sQuery(id+"F0.wireOp",EDGE,"E69"),sQuery(id+"F0.wireOp",EDGE,"E70"),sQuery(id+"F0.wireOp",EDGE,"E71"),sQuery(id+"F0.wireOp",EDGE,"E72"),sQuery(id+"F0.wireOp",EDGE,"E73"),sQuery(id+"F0.wireOp",EDGE,"E74"),sQuery(id+"F0.wireOp",EDGE,"E75"),sQuery(id+"F0.wireOp",EDGE,"E76"),sQuery(id+"F0.wireOp",EDGE,"E77"),sQuery(id+"F0.wireOp",EDGE,"E78"),sQuery(id+"F0.wireOp",EDGE,"E79"),sQuery(id+"F0.wireOp",EDGE,"E80"),sQuery(id+"F0.wireOp",EDGE,"E81"),sQuery(id+"F0.wireOp",EDGE,"E82"),sQuery(id+"F0.wireOp",EDGE,"E83"),sQuery(id+"F0.wireOp",EDGE,"E84"),sQuery(id+"F0.wireOp",EDGE,"E85"),sQuery(id+"F0.wireOp",EDGE,"E86"),sQuery(id+"F0.wireOp",EDGE,"E87"),sQuery(id+"F0.wireOp",EDGE,"E88"),sQuery(id+"F0.wireOp",EDGE,"E89"),sQuery(id+"F0.wireOp",EDGE,"E90"),sQuery(id+"F0.wireOp",EDGE,"E91"),sQuery(id+"F0.wireOp",EDGE,"E92"),sQuery(id+"F0.wireOp",EDGE,"E93"),sQuery(id+"F0.wireOp",EDGE,"E94"),sQuery(id+"F0.wireOp",EDGE,"E95"),sQuery(id+"F0.wireOp",EDGE,"E96"),sQuery(id+"F0.wireOp",EDGE,"E97"),sQuery(id+"F0.wireOp",EDGE,"E98"),sQuery(id+"F0.wireOp",EDGE,"E99"),sQuery(id+"F0.wireOp",EDGE,"E100"),sQuery(id+"F0.wireOp",EDGE,"E101"),sQuery(id+"F0.wireOp",EDGE,"E102"),sQuery(id+"F0.wireOp",EDGE,"E103"),sQuery(id+"F0.wireOp",EDGE,"E104")])]}),"instanceName":"20"});
            var Q12;
            Q12=makeQuery(id+"F2.opPattern","COPY",BODY,{"derivedFrom":makeQuery(id+"F1.opExtrude","SWEPT_BODY",BODY,{"disambiguationData":[OSD([sQuery(id+"F0.wireOp",EDGE,"E1"),sQuery(id+"F0.wireOp",EDGE,"E2"),sQuery(id+"F0.wireOp",EDGE,"E3"),sQuery(id+"F0.wireOp",EDGE,"E4"),sQuery(id+"F0.wireOp",EDGE,"E5"),sQuery(id+"F0.wireOp",EDGE,"E6"),sQuery(id+"F0.wireOp",EDGE,"E7"),sQuery(id+"F0.wireOp",EDGE,"E8"),sQuery(id+"F0.wireOp",EDGE,"E9"),sQuery(id+"F0.wireOp",EDGE,"E10"),sQuery(id+"F0.wireOp",EDGE,"E11"),sQuery(id+"F0.wireOp",EDGE,"E12"),sQuery(id+"F0.wireOp",EDGE,"E13"),sQuery(id+"F0.wireOp",EDGE,"E14"),sQuery(id+"F0.wireOp",EDGE,"E15"),sQuery(id+"F0.wireOp",EDGE,"E16"),sQuery(id+"F0.wireOp",EDGE,"E17"),sQuery(id+"F0.wireOp",EDGE,"E18"),sQuery(id+"F0.wireOp",EDGE,"E19"),sQuery(id+"F0.wireOp",EDGE,"E20"),sQuery(id+"F0.wireOp",EDGE,"E21"),sQuery(id+"F0.wireOp",EDGE,"E22"),sQuery(id+"F0.wireOp",EDGE,"E23"),sQuery(id+"F0.wireOp",EDGE,"E24"),sQuery(id+"F0.wireOp",EDGE,"E25"),sQuery(id+"F0.wireOp",EDGE,"E26"),sQuery(id+"F0.wireOp",EDGE,"E27"),sQuery(id+"F0.wireOp",EDGE,"E28"),sQuery(id+"F0.wireOp",EDGE,"E29"),sQuery(id+"F0.wireOp",EDGE,"E30"),sQuery(id+"F0.wireOp",EDGE,"E31"),sQuery(id+"F0.wireOp",EDGE,"E32"),sQuery(id+"F0.wireOp",EDGE,"E33"),sQuery(id+"F0.wireOp",EDGE,"E34"),sQuery(id+"F0.wireOp",EDGE,"E35"),sQuery(id+"F0.wireOp",EDGE,"E36"),sQuery(id+"F0.wireOp",EDGE,"E37"),sQuery(id+"F0.wireOp",EDGE,"E38"),sQuery(id+"F0.wireOp",EDGE,"E39"),sQuery(id+"F0.wireOp",EDGE,"E40"),sQuery(id+"F0.wireOp",EDGE,"E41"),sQuery(id+"F0.wireOp",EDGE,"E42"),sQuery(id+"F0.wireOp",EDGE,"E43"),sQuery(id+"F0.wireOp",EDGE,"E44"),sQuery(id+"F0.wireOp",EDGE,"E45"),sQuery(id+"F0.wireOp",EDGE,"E46"),sQuery(id+"F0.wireOp",EDGE,"E47"),sQuery(id+"F0.wireOp",EDGE,"E48"),sQuery(id+"F0.wireOp",EDGE,"E49"),sQuery(id+"F0.wireOp",EDGE,"E50"),sQuery(id+"F0.wireOp",EDGE,"E51"),sQuery(id+"F0.wireOp",EDGE,"E52"),sQuery(id+"F0.wireOp",EDGE,"E53"),sQuery(id+"F0.wireOp",EDGE,"E54"),sQuery(id+"F0.wireOp",EDGE,"E55"),sQuery(id+"F0.wireOp",EDGE,"E56"),sQuery(id+"F0.wireOp",EDGE,"E57"),sQuery(id+"F0.wireOp",EDGE,"E58"),sQuery(id+"F0.wireOp",EDGE,"E59"),sQuery(id+"F0.wireOp",EDGE,"E60"),sQuery(id+"F0.wireOp",EDGE,"E61"),sQuery(id+"F0.wireOp",EDGE,"E62"),sQuery(id+"F0.wireOp",EDGE,"E63"),sQuery(id+"F0.wireOp",EDGE,"E64"),sQuery(id+"F0.wireOp",EDGE,"E65"),sQuery(id+"F0.wireOp",EDGE,"E66"),sQuery(id+"F0.wireOp",EDGE,"E67"),sQuery(id+"F0.wireOp",EDGE,"E68"),sQuery(id+"F0.wireOp",EDGE,"E69"),sQuery(id+"F0.wireOp",EDGE,"E70"),sQuery(id+"F0.wireOp",EDGE,"E71"),sQuery(id+"F0.wireOp",EDGE,"E72"),sQuery(id+"F0.wireOp",EDGE,"E73"),sQuery(id+"F0.wireOp",EDGE,"E74"),sQuery(id+"F0.wireOp",EDGE,"E75"),sQuery(id+"F0.wireOp",EDGE,"E76"),sQuery(id+"F0.wireOp",EDGE,"E77"),sQuery(id+"F0.wireOp",EDGE,"E78"),sQuery(id+"F0.wireOp",EDGE,"E79"),sQuery(id+"F0.wireOp",EDGE,"E80"),sQuery(id+"F0.wireOp",EDGE,"E81"),sQuery(id+"F0.wireOp",EDGE,"E82"),sQuery(id+"F0.wireOp",EDGE,"E83"),sQuery(id+"F0.wireOp",EDGE,"E84"),sQuery(id+"F0.wireOp",EDGE,"E85"),sQuery(id+"F0.wireOp",EDGE,"E86"),sQuery(id+"F0.wireOp",EDGE,"E87"),sQuery(id+"F0.wireOp",EDGE,"E88"),sQuery(id+"F0.wireOp",EDGE,"E89"),sQuery(id+"F0.wireOp",EDGE,"E90"),sQuery(id+"F0.wireOp",EDGE,"E91"),sQuery(id+"F0.wireOp",EDGE,"E92"),sQuery(id+"F0.wireOp",EDGE,"E93"),sQuery(id+"F0.wireOp",EDGE,"E94"),sQuery(id+"F0.wireOp",EDGE,"E95"),sQuery(id+"F0.wireOp",EDGE,"E96"),sQuery(id+"F0.wireOp",EDGE,"E97"),sQuery(id+"F0.wireOp",EDGE,"E98"),sQuery(id+"F0.wireOp",EDGE,"E99"),sQuery(id+"F0.wireOp",EDGE,"E100"),sQuery(id+"F0.wireOp",EDGE,"E101"),sQuery(id+"F0.wireOp",EDGE,"E102"),sQuery(id+"F0.wireOp",EDGE,"E103"),sQuery(id+"F0.wireOp",EDGE,"E104")])]}),"instanceName":"21"});
            var Q13;
            Q13=makeQuery(id+"F2.opPattern","COPY",BODY,{"derivedFrom":makeQuery(id+"F1.opExtrude","SWEPT_BODY",BODY,{"disambiguationData":[OSD([sQuery(id+"F0.wireOp",EDGE,"E1"),sQuery(id+"F0.wireOp",EDGE,"E2"),sQuery(id+"F0.wireOp",EDGE,"E3"),sQuery(id+"F0.wireOp",EDGE,"E4"),sQuery(id+"F0.wireOp",EDGE,"E5"),sQuery(id+"F0.wireOp",EDGE,"E6"),sQuery(id+"F0.wireOp",EDGE,"E7"),sQuery(id+"F0.wireOp",EDGE,"E8"),sQuery(id+"F0.wireOp",EDGE,"E9"),sQuery(id+"F0.wireOp",EDGE,"E10"),sQuery(id+"F0.wireOp",EDGE,"E11"),sQuery(id+"F0.wireOp",EDGE,"E12"),sQuery(id+"F0.wireOp",EDGE,"E13"),sQuery(id+"F0.wireOp",EDGE,"E14"),sQuery(id+"F0.wireOp",EDGE,"E15"),sQuery(id+"F0.wireOp",EDGE,"E16"),sQuery(id+"F0.wireOp",EDGE,"E17"),sQuery(id+"F0.wireOp",EDGE,"E18"),sQuery(id+"F0.wireOp",EDGE,"E19"),sQuery(id+"F0.wireOp",EDGE,"E20"),sQuery(id+"F0.wireOp",EDGE,"E21"),sQuery(id+"F0.wireOp",EDGE,"E22"),sQuery(id+"F0.wireOp",EDGE,"E23"),sQuery(id+"F0.wireOp",EDGE,"E24"),sQuery(id+"F0.wireOp",EDGE,"E25"),sQuery(id+"F0.wireOp",EDGE,"E26"),sQuery(id+"F0.wireOp",EDGE,"E27"),sQuery(id+"F0.wireOp",EDGE,"E28"),sQuery(id+"F0.wireOp",EDGE,"E29"),sQuery(id+"F0.wireOp",EDGE,"E30"),sQuery(id+"F0.wireOp",EDGE,"E31"),sQuery(id+"F0.wireOp",EDGE,"E32"),sQuery(id+"F0.wireOp",EDGE,"E33"),sQuery(id+"F0.wireOp",EDGE,"E34"),sQuery(id+"F0.wireOp",EDGE,"E35"),sQuery(id+"F0.wireOp",EDGE,"E36"),sQuery(id+"F0.wireOp",EDGE,"E37"),sQuery(id+"F0.wireOp",EDGE,"E38"),sQuery(id+"F0.wireOp",EDGE,"E39"),sQuery(id+"F0.wireOp",EDGE,"E40"),sQuery(id+"F0.wireOp",EDGE,"E41"),sQuery(id+"F0.wireOp",EDGE,"E42"),sQuery(id+"F0.wireOp",EDGE,"E43"),sQuery(id+"F0.wireOp",EDGE,"E44"),sQuery(id+"F0.wireOp",EDGE,"E45"),sQuery(id+"F0.wireOp",EDGE,"E46"),sQuery(id+"F0.wireOp",EDGE,"E47"),sQuery(id+"F0.wireOp",EDGE,"E48"),sQuery(id+"F0.wireOp",EDGE,"E49"),sQuery(id+"F0.wireOp",EDGE,"E50"),sQuery(id+"F0.wireOp",EDGE,"E51"),sQuery(id+"F0.wireOp",EDGE,"E52"),sQuery(id+"F0.wireOp",EDGE,"E53"),sQuery(id+"F0.wireOp",EDGE,"E54"),sQuery(id+"F0.wireOp",EDGE,"E55"),sQuery(id+"F0.wireOp",EDGE,"E56"),sQuery(id+"F0.wireOp",EDGE,"E57"),sQuery(id+"F0.wireOp",EDGE,"E58"),sQuery(id+"F0.wireOp",EDGE,"E59"),sQuery(id+"F0.wireOp",EDGE,"E60"),sQuery(id+"F0.wireOp",EDGE,"E61"),sQuery(id+"F0.wireOp",EDGE,"E62"),sQuery(id+"F0.wireOp",EDGE,"E63"),sQuery(id+"F0.wireOp",EDGE,"E64"),sQuery(id+"F0.wireOp",EDGE,"E65"),sQuery(id+"F0.wireOp",EDGE,"E66"),sQuery(id+"F0.wireOp",EDGE,"E67"),sQuery(id+"F0.wireOp",EDGE,"E68"),sQuery(id+"F0.wireOp",EDGE,"E69"),sQuery(id+"F0.wireOp",EDGE,"E70"),sQuery(id+"F0.wireOp",EDGE,"E71"),sQuery(id+"F0.wireOp",EDGE,"E72"),sQuery(id+"F0.wireOp",EDGE,"E73"),sQuery(id+"F0.wireOp",EDGE,"E74"),sQuery(id+"F0.wireOp",EDGE,"E75"),sQuery(id+"F0.wireOp",EDGE,"E76"),sQuery(id+"F0.wireOp",EDGE,"E77"),sQuery(id+"F0.wireOp",EDGE,"E78"),sQuery(id+"F0.wireOp",EDGE,"E79"),sQuery(id+"F0.wireOp",EDGE,"E80"),sQuery(id+"F0.wireOp",EDGE,"E81"),sQuery(id+"F0.wireOp",EDGE,"E82"),sQuery(id+"F0.wireOp",EDGE,"E83"),sQuery(id+"F0.wireOp",EDGE,"E84"),sQuery(id+"F0.wireOp",EDGE,"E85"),sQuery(id+"F0.wireOp",EDGE,"E86"),sQuery(id+"F0.wireOp",EDGE,"E87"),sQuery(id+"F0.wireOp",EDGE,"E88"),sQuery(id+"F0.wireOp",EDGE,"E89"),sQuery(id+"F0.wireOp",EDGE,"E90"),sQuery(id+"F0.wireOp",EDGE,"E91"),sQuery(id+"F0.wireOp",EDGE,"E92"),sQuery(id+"F0.wireOp",EDGE,"E93"),sQuery(id+"F0.wireOp",EDGE,"E94"),sQuery(id+"F0.wireOp",EDGE,"E95"),sQuery(id+"F0.wireOp",EDGE,"E96"),sQuery(id+"F0.wireOp",EDGE,"E97"),sQuery(id+"F0.wireOp",EDGE,"E98"),sQuery(id+"F0.wireOp",EDGE,"E99"),sQuery(id+"F0.wireOp",EDGE,"E100"),sQuery(id+"F0.wireOp",EDGE,"E101"),sQuery(id+"F0.wireOp",EDGE,"E102"),sQuery(id+"F0.wireOp",EDGE,"E103"),sQuery(id+"F0.wireOp",EDGE,"E104")])]}),"instanceName":"22"});
            booleanBodies(context, id + "F3", {"operationType" : BooleanOperationType.UNION, "tools" : qUnion([Q0, Q1, Q2, Q3, Q4, Q5, Q6, Q7, Q8, Q9, Q10, Q11, Q12, Q13])});
        }
        {
            var Q0;
            Q0=makeQuery(id+"F1.opExtrude","SWEPT_BODY",BODY,{"disambiguationData":[OSD([sQuery(id+"F0.wireOp",EDGE,"E105")])]});
            var Q1;
            Q1=makeQuery(id+"F2.opPattern","COPY",BODY,{"derivedFrom":makeQuery(id+"F1.opExtrude","SWEPT_BODY",BODY,{"disambiguationData":[OSD([sQuery(id+"F0.wireOp",EDGE,"E1"),sQuery(id+"F0.wireOp",EDGE,"E2"),sQuery(id+"F0.wireOp",EDGE,"E3"),sQuery(id+"F0.wireOp",EDGE,"E4"),sQuery(id+"F0.wireOp",EDGE,"E5"),sQuery(id+"F0.wireOp",EDGE,"E6"),sQuery(id+"F0.wireOp",EDGE,"E7"),sQuery(id+"F0.wireOp",EDGE,"E8"),sQuery(id+"F0.wireOp",EDGE,"E9"),sQuery(id+"F0.wireOp",EDGE,"E10"),sQuery(id+"F0.wireOp",EDGE,"E11"),sQuery(id+"F0.wireOp",EDGE,"E12"),sQuery(id+"F0.wireOp",EDGE,"E13"),sQuery(id+"F0.wireOp",EDGE,"E14"),sQuery(id+"F0.wireOp",EDGE,"E15"),sQuery(id+"F0.wireOp",EDGE,"E16"),sQuery(id+"F0.wireOp",EDGE,"E17"),sQuery(id+"F0.wireOp",EDGE,"E18"),sQuery(id+"F0.wireOp",EDGE,"E19"),sQuery(id+"F0.wireOp",EDGE,"E20"),sQuery(id+"F0.wireOp",EDGE,"E21"),sQuery(id+"F0.wireOp",EDGE,"E22"),sQuery(id+"F0.wireOp",EDGE,"E23"),sQuery(id+"F0.wireOp",EDGE,"E24"),sQuery(id+"F0.wireOp",EDGE,"E25"),sQuery(id+"F0.wireOp",EDGE,"E26"),sQuery(id+"F0.wireOp",EDGE,"E27"),sQuery(id+"F0.wireOp",EDGE,"E28"),sQuery(id+"F0.wireOp",EDGE,"E29"),sQuery(id+"F0.wireOp",EDGE,"E30"),sQuery(id+"F0.wireOp",EDGE,"E31"),sQuery(id+"F0.wireOp",EDGE,"E32"),sQuery(id+"F0.wireOp",EDGE,"E33"),sQuery(id+"F0.wireOp",EDGE,"E34"),sQuery(id+"F0.wireOp",EDGE,"E35"),sQuery(id+"F0.wireOp",EDGE,"E36"),sQuery(id+"F0.wireOp",EDGE,"E37"),sQuery(id+"F0.wireOp",EDGE,"E38"),sQuery(id+"F0.wireOp",EDGE,"E39"),sQuery(id+"F0.wireOp",EDGE,"E40"),sQuery(id+"F0.wireOp",EDGE,"E41"),sQuery(id+"F0.wireOp",EDGE,"E42"),sQuery(id+"F0.wireOp",EDGE,"E43"),sQuery(id+"F0.wireOp",EDGE,"E44"),sQuery(id+"F0.wireOp",EDGE,"E45"),sQuery(id+"F0.wireOp",EDGE,"E46"),sQuery(id+"F0.wireOp",EDGE,"E47"),sQuery(id+"F0.wireOp",EDGE,"E48"),sQuery(id+"F0.wireOp",EDGE,"E49"),sQuery(id+"F0.wireOp",EDGE,"E50"),sQuery(id+"F0.wireOp",EDGE,"E51"),sQuery(id+"F0.wireOp",EDGE,"E52"),sQuery(id+"F0.wireOp",EDGE,"E53"),sQuery(id+"F0.wireOp",EDGE,"E54"),sQuery(id+"F0.wireOp",EDGE,"E55"),sQuery(id+"F0.wireOp",EDGE,"E56"),sQuery(id+"F0.wireOp",EDGE,"E57"),sQuery(id+"F0.wireOp",EDGE,"E58"),sQuery(id+"F0.wireOp",EDGE,"E59"),sQuery(id+"F0.wireOp",EDGE,"E60"),sQuery(id+"F0.wireOp",EDGE,"E61"),sQuery(id+"F0.wireOp",EDGE,"E62"),sQuery(id+"F0.wireOp",EDGE,"E63"),sQuery(id+"F0.wireOp",EDGE,"E64"),sQuery(id+"F0.wireOp",EDGE,"E65"),sQuery(id+"F0.wireOp",EDGE,"E66"),sQuery(id+"F0.wireOp",EDGE,"E67"),sQuery(id+"F0.wireOp",EDGE,"E68"),sQuery(id+"F0.wireOp",EDGE,"E69"),sQuery(id+"F0.wireOp",EDGE,"E70"),sQuery(id+"F0.wireOp",EDGE,"E71"),sQuery(id+"F0.wireOp",EDGE,"E72"),sQuery(id+"F0.wireOp",EDGE,"E73"),sQuery(id+"F0.wireOp",EDGE,"E74"),sQuery(id+"F0.wireOp",EDGE,"E75"),sQuery(id+"F0.wireOp",EDGE,"E76"),sQuery(id+"F0.wireOp",EDGE,"E77"),sQuery(id+"F0.wireOp",EDGE,"E78"),sQuery(id+"F0.wireOp",EDGE,"E79"),sQuery(id+"F0.wireOp",EDGE,"E80"),sQuery(id+"F0.wireOp",EDGE,"E81"),sQuery(id+"F0.wireOp",EDGE,"E82"),sQuery(id+"F0.wireOp",EDGE,"E83"),sQuery(id+"F0.wireOp",EDGE,"E84"),sQuery(id+"F0.wireOp",EDGE,"E85"),sQuery(id+"F0.wireOp",EDGE,"E86"),sQuery(id+"F0.wireOp",EDGE,"E87"),sQuery(id+"F0.wireOp",EDGE,"E88"),sQuery(id+"F0.wireOp",EDGE,"E89"),sQuery(id+"F0.wireOp",EDGE,"E90"),sQuery(id+"F0.wireOp",EDGE,"E91"),sQuery(id+"F0.wireOp",EDGE,"E92"),sQuery(id+"F0.wireOp",EDGE,"E93"),sQuery(id+"F0.wireOp",EDGE,"E94"),sQuery(id+"F0.wireOp",EDGE,"E95"),sQuery(id+"F0.wireOp",EDGE,"E96"),sQuery(id+"F0.wireOp",EDGE,"E97"),sQuery(id+"F0.wireOp",EDGE,"E98"),sQuery(id+"F0.wireOp",EDGE,"E99"),sQuery(id+"F0.wireOp",EDGE,"E100"),sQuery(id+"F0.wireOp",EDGE,"E101"),sQuery(id+"F0.wireOp",EDGE,"E102"),sQuery(id+"F0.wireOp",EDGE,"E103"),sQuery(id+"F0.wireOp",EDGE,"E104")])]}),"instanceName":"1"});
            var Q2;
            Q2=makeQuery(id+"F2.opPattern","COPY",BODY,{"derivedFrom":makeQuery(id+"F1.opExtrude","SWEPT_BODY",BODY,{"disambiguationData":[OSD([sQuery(id+"F0.wireOp",EDGE,"E1"),sQuery(id+"F0.wireOp",EDGE,"E2"),sQuery(id+"F0.wireOp",EDGE,"E3"),sQuery(id+"F0.wireOp",EDGE,"E4"),sQuery(id+"F0.wireOp",EDGE,"E5"),sQuery(id+"F0.wireOp",EDGE,"E6"),sQuery(id+"F0.wireOp",EDGE,"E7"),sQuery(id+"F0.wireOp",EDGE,"E8"),sQuery(id+"F0.wireOp",EDGE,"E9"),sQuery(id+"F0.wireOp",EDGE,"E10"),sQuery(id+"F0.wireOp",EDGE,"E11"),sQuery(id+"F0.wireOp",EDGE,"E12"),sQuery(id+"F0.wireOp",EDGE,"E13"),sQuery(id+"F0.wireOp",EDGE,"E14"),sQuery(id+"F0.wireOp",EDGE,"E15"),sQuery(id+"F0.wireOp",EDGE,"E16"),sQuery(id+"F0.wireOp",EDGE,"E17"),sQuery(id+"F0.wireOp",EDGE,"E18"),sQuery(id+"F0.wireOp",EDGE,"E19"),sQuery(id+"F0.wireOp",EDGE,"E20"),sQuery(id+"F0.wireOp",EDGE,"E21"),sQuery(id+"F0.wireOp",EDGE,"E22"),sQuery(id+"F0.wireOp",EDGE,"E23"),sQuery(id+"F0.wireOp",EDGE,"E24"),sQuery(id+"F0.wireOp",EDGE,"E25"),sQuery(id+"F0.wireOp",EDGE,"E26"),sQuery(id+"F0.wireOp",EDGE,"E27"),sQuery(id+"F0.wireOp",EDGE,"E28"),sQuery(id+"F0.wireOp",EDGE,"E29"),sQuery(id+"F0.wireOp",EDGE,"E30"),sQuery(id+"F0.wireOp",EDGE,"E31"),sQuery(id+"F0.wireOp",EDGE,"E32"),sQuery(id+"F0.wireOp",EDGE,"E33"),sQuery(id+"F0.wireOp",EDGE,"E34"),sQuery(id+"F0.wireOp",EDGE,"E35"),sQuery(id+"F0.wireOp",EDGE,"E36"),sQuery(id+"F0.wireOp",EDGE,"E37"),sQuery(id+"F0.wireOp",EDGE,"E38"),sQuery(id+"F0.wireOp",EDGE,"E39"),sQuery(id+"F0.wireOp",EDGE,"E40"),sQuery(id+"F0.wireOp",EDGE,"E41"),sQuery(id+"F0.wireOp",EDGE,"E42"),sQuery(id+"F0.wireOp",EDGE,"E43"),sQuery(id+"F0.wireOp",EDGE,"E44"),sQuery(id+"F0.wireOp",EDGE,"E45"),sQuery(id+"F0.wireOp",EDGE,"E46"),sQuery(id+"F0.wireOp",EDGE,"E47"),sQuery(id+"F0.wireOp",EDGE,"E48"),sQuery(id+"F0.wireOp",EDGE,"E49"),sQuery(id+"F0.wireOp",EDGE,"E50"),sQuery(id+"F0.wireOp",EDGE,"E51"),sQuery(id+"F0.wireOp",EDGE,"E52"),sQuery(id+"F0.wireOp",EDGE,"E53"),sQuery(id+"F0.wireOp",EDGE,"E54"),sQuery(id+"F0.wireOp",EDGE,"E55"),sQuery(id+"F0.wireOp",EDGE,"E56"),sQuery(id+"F0.wireOp",EDGE,"E57"),sQuery(id+"F0.wireOp",EDGE,"E58"),sQuery(id+"F0.wireOp",EDGE,"E59"),sQuery(id+"F0.wireOp",EDGE,"E60"),sQuery(id+"F0.wireOp",EDGE,"E61"),sQuery(id+"F0.wireOp",EDGE,"E62"),sQuery(id+"F0.wireOp",EDGE,"E63"),sQuery(id+"F0.wireOp",EDGE,"E64"),sQuery(id+"F0.wireOp",EDGE,"E65"),sQuery(id+"F0.wireOp",EDGE,"E66"),sQuery(id+"F0.wireOp",EDGE,"E67"),sQuery(id+"F0.wireOp",EDGE,"E68"),sQuery(id+"F0.wireOp",EDGE,"E69"),sQuery(id+"F0.wireOp",EDGE,"E70"),sQuery(id+"F0.wireOp",EDGE,"E71"),sQuery(id+"F0.wireOp",EDGE,"E72"),sQuery(id+"F0.wireOp",EDGE,"E73"),sQuery(id+"F0.wireOp",EDGE,"E74"),sQuery(id+"F0.wireOp",EDGE,"E75"),sQuery(id+"F0.wireOp",EDGE,"E76"),sQuery(id+"F0.wireOp",EDGE,"E77"),sQuery(id+"F0.wireOp",EDGE,"E78"),sQuery(id+"F0.wireOp",EDGE,"E79"),sQuery(id+"F0.wireOp",EDGE,"E80"),sQuery(id+"F0.wireOp",EDGE,"E81"),sQuery(id+"F0.wireOp",EDGE,"E82"),sQuery(id+"F0.wireOp",EDGE,"E83"),sQuery(id+"F0.wireOp",EDGE,"E84"),sQuery(id+"F0.wireOp",EDGE,"E85"),sQuery(id+"F0.wireOp",EDGE,"E86"),sQuery(id+"F0.wireOp",EDGE,"E87"),sQuery(id+"F0.wireOp",EDGE,"E88"),sQuery(id+"F0.wireOp",EDGE,"E89"),sQuery(id+"F0.wireOp",EDGE,"E90"),sQuery(id+"F0.wireOp",EDGE,"E91"),sQuery(id+"F0.wireOp",EDGE,"E92"),sQuery(id+"F0.wireOp",EDGE,"E93"),sQuery(id+"F0.wireOp",EDGE,"E94"),sQuery(id+"F0.wireOp",EDGE,"E95"),sQuery(id+"F0.wireOp",EDGE,"E96"),sQuery(id+"F0.wireOp",EDGE,"E97"),sQuery(id+"F0.wireOp",EDGE,"E98"),sQuery(id+"F0.wireOp",EDGE,"E99"),sQuery(id+"F0.wireOp",EDGE,"E100"),sQuery(id+"F0.wireOp",EDGE,"E101"),sQuery(id+"F0.wireOp",EDGE,"E102"),sQuery(id+"F0.wireOp",EDGE,"E103"),sQuery(id+"F0.wireOp",EDGE,"E104")])]}),"instanceName":"23"});
            var Q3;
            Q3=makeQuery(id+"F2.opPattern","COPY",BODY,{"derivedFrom":makeQuery(id+"F1.opExtrude","SWEPT_BODY",BODY,{"disambiguationData":[OSD([sQuery(id+"F0.wireOp",EDGE,"E1"),sQuery(id+"F0.wireOp",EDGE,"E2"),sQuery(id+"F0.wireOp",EDGE,"E3"),sQuery(id+"F0.wireOp",EDGE,"E4"),sQuery(id+"F0.wireOp",EDGE,"E5"),sQuery(id+"F0.wireOp",EDGE,"E6"),sQuery(id+"F0.wireOp",EDGE,"E7"),sQuery(id+"F0.wireOp",EDGE,"E8"),sQuery(id+"F0.wireOp",EDGE,"E9"),sQuery(id+"F0.wireOp",EDGE,"E10"),sQuery(id+"F0.wireOp",EDGE,"E11"),sQuery(id+"F0.wireOp",EDGE,"E12"),sQuery(id+"F0.wireOp",EDGE,"E13"),sQuery(id+"F0.wireOp",EDGE,"E14"),sQuery(id+"F0.wireOp",EDGE,"E15"),sQuery(id+"F0.wireOp",EDGE,"E16"),sQuery(id+"F0.wireOp",EDGE,"E17"),sQuery(id+"F0.wireOp",EDGE,"E18"),sQuery(id+"F0.wireOp",EDGE,"E19"),sQuery(id+"F0.wireOp",EDGE,"E20"),sQuery(id+"F0.wireOp",EDGE,"E21"),sQuery(id+"F0.wireOp",EDGE,"E22"),sQuery(id+"F0.wireOp",EDGE,"E23"),sQuery(id+"F0.wireOp",EDGE,"E24"),sQuery(id+"F0.wireOp",EDGE,"E25"),sQuery(id+"F0.wireOp",EDGE,"E26"),sQuery(id+"F0.wireOp",EDGE,"E27"),sQuery(id+"F0.wireOp",EDGE,"E28"),sQuery(id+"F0.wireOp",EDGE,"E29"),sQuery(id+"F0.wireOp",EDGE,"E30"),sQuery(id+"F0.wireOp",EDGE,"E31"),sQuery(id+"F0.wireOp",EDGE,"E32"),sQuery(id+"F0.wireOp",EDGE,"E33"),sQuery(id+"F0.wireOp",EDGE,"E34"),sQuery(id+"F0.wireOp",EDGE,"E35"),sQuery(id+"F0.wireOp",EDGE,"E36"),sQuery(id+"F0.wireOp",EDGE,"E37"),sQuery(id+"F0.wireOp",EDGE,"E38"),sQuery(id+"F0.wireOp",EDGE,"E39"),sQuery(id+"F0.wireOp",EDGE,"E40"),sQuery(id+"F0.wireOp",EDGE,"E41"),sQuery(id+"F0.wireOp",EDGE,"E42"),sQuery(id+"F0.wireOp",EDGE,"E43"),sQuery(id+"F0.wireOp",EDGE,"E44"),sQuery(id+"F0.wireOp",EDGE,"E45"),sQuery(id+"F0.wireOp",EDGE,"E46"),sQuery(id+"F0.wireOp",EDGE,"E47"),sQuery(id+"F0.wireOp",EDGE,"E48"),sQuery(id+"F0.wireOp",EDGE,"E49"),sQuery(id+"F0.wireOp",EDGE,"E50"),sQuery(id+"F0.wireOp",EDGE,"E51"),sQuery(id+"F0.wireOp",EDGE,"E52"),sQuery(id+"F0.wireOp",EDGE,"E53"),sQuery(id+"F0.wireOp",EDGE,"E54"),sQuery(id+"F0.wireOp",EDGE,"E55"),sQuery(id+"F0.wireOp",EDGE,"E56"),sQuery(id+"F0.wireOp",EDGE,"E57"),sQuery(id+"F0.wireOp",EDGE,"E58"),sQuery(id+"F0.wireOp",EDGE,"E59"),sQuery(id+"F0.wireOp",EDGE,"E60"),sQuery(id+"F0.wireOp",EDGE,"E61"),sQuery(id+"F0.wireOp",EDGE,"E62"),sQuery(id+"F0.wireOp",EDGE,"E63"),sQuery(id+"F0.wireOp",EDGE,"E64"),sQuery(id+"F0.wireOp",EDGE,"E65"),sQuery(id+"F0.wireOp",EDGE,"E66"),sQuery(id+"F0.wireOp",EDGE,"E67"),sQuery(id+"F0.wireOp",EDGE,"E68"),sQuery(id+"F0.wireOp",EDGE,"E69"),sQuery(id+"F0.wireOp",EDGE,"E70"),sQuery(id+"F0.wireOp",EDGE,"E71"),sQuery(id+"F0.wireOp",EDGE,"E72"),sQuery(id+"F0.wireOp",EDGE,"E73"),sQuery(id+"F0.wireOp",EDGE,"E74"),sQuery(id+"F0.wireOp",EDGE,"E75"),sQuery(id+"F0.wireOp",EDGE,"E76"),sQuery(id+"F0.wireOp",EDGE,"E77"),sQuery(id+"F0.wireOp",EDGE,"E78"),sQuery(id+"F0.wireOp",EDGE,"E79"),sQuery(id+"F0.wireOp",EDGE,"E80"),sQuery(id+"F0.wireOp",EDGE,"E81"),sQuery(id+"F0.wireOp",EDGE,"E82"),sQuery(id+"F0.wireOp",EDGE,"E83"),sQuery(id+"F0.wireOp",EDGE,"E84"),sQuery(id+"F0.wireOp",EDGE,"E85"),sQuery(id+"F0.wireOp",EDGE,"E86"),sQuery(id+"F0.wireOp",EDGE,"E87"),sQuery(id+"F0.wireOp",EDGE,"E88"),sQuery(id+"F0.wireOp",EDGE,"E89"),sQuery(id+"F0.wireOp",EDGE,"E90"),sQuery(id+"F0.wireOp",EDGE,"E91"),sQuery(id+"F0.wireOp",EDGE,"E92"),sQuery(id+"F0.wireOp",EDGE,"E93"),sQuery(id+"F0.wireOp",EDGE,"E94"),sQuery(id+"F0.wireOp",EDGE,"E95"),sQuery(id+"F0.wireOp",EDGE,"E96"),sQuery(id+"F0.wireOp",EDGE,"E97"),sQuery(id+"F0.wireOp",EDGE,"E98"),sQuery(id+"F0.wireOp",EDGE,"E99"),sQuery(id+"F0.wireOp",EDGE,"E100"),sQuery(id+"F0.wireOp",EDGE,"E101"),sQuery(id+"F0.wireOp",EDGE,"E102"),sQuery(id+"F0.wireOp",EDGE,"E103"),sQuery(id+"F0.wireOp",EDGE,"E104")])]}),"instanceName":"24"});
            var Q4;
            Q4=makeQuery(id+"F2.opPattern","COPY",BODY,{"derivedFrom":makeQuery(id+"F1.opExtrude","SWEPT_BODY",BODY,{"disambiguationData":[OSD([sQuery(id+"F0.wireOp",EDGE,"E1"),sQuery(id+"F0.wireOp",EDGE,"E2"),sQuery(id+"F0.wireOp",EDGE,"E3"),sQuery(id+"F0.wireOp",EDGE,"E4"),sQuery(id+"F0.wireOp",EDGE,"E5"),sQuery(id+"F0.wireOp",EDGE,"E6"),sQuery(id+"F0.wireOp",EDGE,"E7"),sQuery(id+"F0.wireOp",EDGE,"E8"),sQuery(id+"F0.wireOp",EDGE,"E9"),sQuery(id+"F0.wireOp",EDGE,"E10"),sQuery(id+"F0.wireOp",EDGE,"E11"),sQuery(id+"F0.wireOp",EDGE,"E12"),sQuery(id+"F0.wireOp",EDGE,"E13"),sQuery(id+"F0.wireOp",EDGE,"E14"),sQuery(id+"F0.wireOp",EDGE,"E15"),sQuery(id+"F0.wireOp",EDGE,"E16"),sQuery(id+"F0.wireOp",EDGE,"E17"),sQuery(id+"F0.wireOp",EDGE,"E18"),sQuery(id+"F0.wireOp",EDGE,"E19"),sQuery(id+"F0.wireOp",EDGE,"E20"),sQuery(id+"F0.wireOp",EDGE,"E21"),sQuery(id+"F0.wireOp",EDGE,"E22"),sQuery(id+"F0.wireOp",EDGE,"E23"),sQuery(id+"F0.wireOp",EDGE,"E24"),sQuery(id+"F0.wireOp",EDGE,"E25"),sQuery(id+"F0.wireOp",EDGE,"E26"),sQuery(id+"F0.wireOp",EDGE,"E27"),sQuery(id+"F0.wireOp",EDGE,"E28"),sQuery(id+"F0.wireOp",EDGE,"E29"),sQuery(id+"F0.wireOp",EDGE,"E30"),sQuery(id+"F0.wireOp",EDGE,"E31"),sQuery(id+"F0.wireOp",EDGE,"E32"),sQuery(id+"F0.wireOp",EDGE,"E33"),sQuery(id+"F0.wireOp",EDGE,"E34"),sQuery(id+"F0.wireOp",EDGE,"E35"),sQuery(id+"F0.wireOp",EDGE,"E36"),sQuery(id+"F0.wireOp",EDGE,"E37"),sQuery(id+"F0.wireOp",EDGE,"E38"),sQuery(id+"F0.wireOp",EDGE,"E39"),sQuery(id+"F0.wireOp",EDGE,"E40"),sQuery(id+"F0.wireOp",EDGE,"E41"),sQuery(id+"F0.wireOp",EDGE,"E42"),sQuery(id+"F0.wireOp",EDGE,"E43"),sQuery(id+"F0.wireOp",EDGE,"E44"),sQuery(id+"F0.wireOp",EDGE,"E45"),sQuery(id+"F0.wireOp",EDGE,"E46"),sQuery(id+"F0.wireOp",EDGE,"E47"),sQuery(id+"F0.wireOp",EDGE,"E48"),sQuery(id+"F0.wireOp",EDGE,"E49"),sQuery(id+"F0.wireOp",EDGE,"E50"),sQuery(id+"F0.wireOp",EDGE,"E51"),sQuery(id+"F0.wireOp",EDGE,"E52"),sQuery(id+"F0.wireOp",EDGE,"E53"),sQuery(id+"F0.wireOp",EDGE,"E54"),sQuery(id+"F0.wireOp",EDGE,"E55"),sQuery(id+"F0.wireOp",EDGE,"E56"),sQuery(id+"F0.wireOp",EDGE,"E57"),sQuery(id+"F0.wireOp",EDGE,"E58"),sQuery(id+"F0.wireOp",EDGE,"E59"),sQuery(id+"F0.wireOp",EDGE,"E60"),sQuery(id+"F0.wireOp",EDGE,"E61"),sQuery(id+"F0.wireOp",EDGE,"E62"),sQuery(id+"F0.wireOp",EDGE,"E63"),sQuery(id+"F0.wireOp",EDGE,"E64"),sQuery(id+"F0.wireOp",EDGE,"E65"),sQuery(id+"F0.wireOp",EDGE,"E66"),sQuery(id+"F0.wireOp",EDGE,"E67"),sQuery(id+"F0.wireOp",EDGE,"E68"),sQuery(id+"F0.wireOp",EDGE,"E69"),sQuery(id+"F0.wireOp",EDGE,"E70"),sQuery(id+"F0.wireOp",EDGE,"E71"),sQuery(id+"F0.wireOp",EDGE,"E72"),sQuery(id+"F0.wireOp",EDGE,"E73"),sQuery(id+"F0.wireOp",EDGE,"E74"),sQuery(id+"F0.wireOp",EDGE,"E75"),sQuery(id+"F0.wireOp",EDGE,"E76"),sQuery(id+"F0.wireOp",EDGE,"E77"),sQuery(id+"F0.wireOp",EDGE,"E78"),sQuery(id+"F0.wireOp",EDGE,"E79"),sQuery(id+"F0.wireOp",EDGE,"E80"),sQuery(id+"F0.wireOp",EDGE,"E81"),sQuery(id+"F0.wireOp",EDGE,"E82"),sQuery(id+"F0.wireOp",EDGE,"E83"),sQuery(id+"F0.wireOp",EDGE,"E84"),sQuery(id+"F0.wireOp",EDGE,"E85"),sQuery(id+"F0.wireOp",EDGE,"E86"),sQuery(id+"F0.wireOp",EDGE,"E87"),sQuery(id+"F0.wireOp",EDGE,"E88"),sQuery(id+"F0.wireOp",EDGE,"E89"),sQuery(id+"F0.wireOp",EDGE,"E90"),sQuery(id+"F0.wireOp",EDGE,"E91"),sQuery(id+"F0.wireOp",EDGE,"E92"),sQuery(id+"F0.wireOp",EDGE,"E93"),sQuery(id+"F0.wireOp",EDGE,"E94"),sQuery(id+"F0.wireOp",EDGE,"E95"),sQuery(id+"F0.wireOp",EDGE,"E96"),sQuery(id+"F0.wireOp",EDGE,"E97"),sQuery(id+"F0.wireOp",EDGE,"E98"),sQuery(id+"F0.wireOp",EDGE,"E99"),sQuery(id+"F0.wireOp",EDGE,"E100"),sQuery(id+"F0.wireOp",EDGE,"E101"),sQuery(id+"F0.wireOp",EDGE,"E102"),sQuery(id+"F0.wireOp",EDGE,"E103"),sQuery(id+"F0.wireOp",EDGE,"E104")])]}),"instanceName":"25"});
            var Q5;
            Q5=makeQuery(id+"F2.opPattern","COPY",BODY,{"derivedFrom":makeQuery(id+"F1.opExtrude","SWEPT_BODY",BODY,{"disambiguationData":[OSD([sQuery(id+"F0.wireOp",EDGE,"E1"),sQuery(id+"F0.wireOp",EDGE,"E2"),sQuery(id+"F0.wireOp",EDGE,"E3"),sQuery(id+"F0.wireOp",EDGE,"E4"),sQuery(id+"F0.wireOp",EDGE,"E5"),sQuery(id+"F0.wireOp",EDGE,"E6"),sQuery(id+"F0.wireOp",EDGE,"E7"),sQuery(id+"F0.wireOp",EDGE,"E8"),sQuery(id+"F0.wireOp",EDGE,"E9"),sQuery(id+"F0.wireOp",EDGE,"E10"),sQuery(id+"F0.wireOp",EDGE,"E11"),sQuery(id+"F0.wireOp",EDGE,"E12"),sQuery(id+"F0.wireOp",EDGE,"E13"),sQuery(id+"F0.wireOp",EDGE,"E14"),sQuery(id+"F0.wireOp",EDGE,"E15"),sQuery(id+"F0.wireOp",EDGE,"E16"),sQuery(id+"F0.wireOp",EDGE,"E17"),sQuery(id+"F0.wireOp",EDGE,"E18"),sQuery(id+"F0.wireOp",EDGE,"E19"),sQuery(id+"F0.wireOp",EDGE,"E20"),sQuery(id+"F0.wireOp",EDGE,"E21"),sQuery(id+"F0.wireOp",EDGE,"E22"),sQuery(id+"F0.wireOp",EDGE,"E23"),sQuery(id+"F0.wireOp",EDGE,"E24"),sQuery(id+"F0.wireOp",EDGE,"E25"),sQuery(id+"F0.wireOp",EDGE,"E26"),sQuery(id+"F0.wireOp",EDGE,"E27"),sQuery(id+"F0.wireOp",EDGE,"E28"),sQuery(id+"F0.wireOp",EDGE,"E29"),sQuery(id+"F0.wireOp",EDGE,"E30"),sQuery(id+"F0.wireOp",EDGE,"E31"),sQuery(id+"F0.wireOp",EDGE,"E32"),sQuery(id+"F0.wireOp",EDGE,"E33"),sQuery(id+"F0.wireOp",EDGE,"E34"),sQuery(id+"F0.wireOp",EDGE,"E35"),sQuery(id+"F0.wireOp",EDGE,"E36"),sQuery(id+"F0.wireOp",EDGE,"E37"),sQuery(id+"F0.wireOp",EDGE,"E38"),sQuery(id+"F0.wireOp",EDGE,"E39"),sQuery(id+"F0.wireOp",EDGE,"E40"),sQuery(id+"F0.wireOp",EDGE,"E41"),sQuery(id+"F0.wireOp",EDGE,"E42"),sQuery(id+"F0.wireOp",EDGE,"E43"),sQuery(id+"F0.wireOp",EDGE,"E44"),sQuery(id+"F0.wireOp",EDGE,"E45"),sQuery(id+"F0.wireOp",EDGE,"E46"),sQuery(id+"F0.wireOp",EDGE,"E47"),sQuery(id+"F0.wireOp",EDGE,"E48"),sQuery(id+"F0.wireOp",EDGE,"E49"),sQuery(id+"F0.wireOp",EDGE,"E50"),sQuery(id+"F0.wireOp",EDGE,"E51"),sQuery(id+"F0.wireOp",EDGE,"E52"),sQuery(id+"F0.wireOp",EDGE,"E53"),sQuery(id+"F0.wireOp",EDGE,"E54"),sQuery(id+"F0.wireOp",EDGE,"E55"),sQuery(id+"F0.wireOp",EDGE,"E56"),sQuery(id+"F0.wireOp",EDGE,"E57"),sQuery(id+"F0.wireOp",EDGE,"E58"),sQuery(id+"F0.wireOp",EDGE,"E59"),sQuery(id+"F0.wireOp",EDGE,"E60"),sQuery(id+"F0.wireOp",EDGE,"E61"),sQuery(id+"F0.wireOp",EDGE,"E62"),sQuery(id+"F0.wireOp",EDGE,"E63"),sQuery(id+"F0.wireOp",EDGE,"E64"),sQuery(id+"F0.wireOp",EDGE,"E65"),sQuery(id+"F0.wireOp",EDGE,"E66"),sQuery(id+"F0.wireOp",EDGE,"E67"),sQuery(id+"F0.wireOp",EDGE,"E68"),sQuery(id+"F0.wireOp",EDGE,"E69"),sQuery(id+"F0.wireOp",EDGE,"E70"),sQuery(id+"F0.wireOp",EDGE,"E71"),sQuery(id+"F0.wireOp",EDGE,"E72"),sQuery(id+"F0.wireOp",EDGE,"E73"),sQuery(id+"F0.wireOp",EDGE,"E74"),sQuery(id+"F0.wireOp",EDGE,"E75"),sQuery(id+"F0.wireOp",EDGE,"E76"),sQuery(id+"F0.wireOp",EDGE,"E77"),sQuery(id+"F0.wireOp",EDGE,"E78"),sQuery(id+"F0.wireOp",EDGE,"E79"),sQuery(id+"F0.wireOp",EDGE,"E80"),sQuery(id+"F0.wireOp",EDGE,"E81"),sQuery(id+"F0.wireOp",EDGE,"E82"),sQuery(id+"F0.wireOp",EDGE,"E83"),sQuery(id+"F0.wireOp",EDGE,"E84"),sQuery(id+"F0.wireOp",EDGE,"E85"),sQuery(id+"F0.wireOp",EDGE,"E86"),sQuery(id+"F0.wireOp",EDGE,"E87"),sQuery(id+"F0.wireOp",EDGE,"E88"),sQuery(id+"F0.wireOp",EDGE,"E89"),sQuery(id+"F0.wireOp",EDGE,"E90"),sQuery(id+"F0.wireOp",EDGE,"E91"),sQuery(id+"F0.wireOp",EDGE,"E92"),sQuery(id+"F0.wireOp",EDGE,"E93"),sQuery(id+"F0.wireOp",EDGE,"E94"),sQuery(id+"F0.wireOp",EDGE,"E95"),sQuery(id+"F0.wireOp",EDGE,"E96"),sQuery(id+"F0.wireOp",EDGE,"E97"),sQuery(id+"F0.wireOp",EDGE,"E98"),sQuery(id+"F0.wireOp",EDGE,"E99"),sQuery(id+"F0.wireOp",EDGE,"E100"),sQuery(id+"F0.wireOp",EDGE,"E101"),sQuery(id+"F0.wireOp",EDGE,"E102"),sQuery(id+"F0.wireOp",EDGE,"E103"),sQuery(id+"F0.wireOp",EDGE,"E104")])]}),"instanceName":"26"});
            var Q6;
            Q6=makeQuery(id+"F2.opPattern","COPY",BODY,{"derivedFrom":makeQuery(id+"F1.opExtrude","SWEPT_BODY",BODY,{"disambiguationData":[OSD([sQuery(id+"F0.wireOp",EDGE,"E1"),sQuery(id+"F0.wireOp",EDGE,"E2"),sQuery(id+"F0.wireOp",EDGE,"E3"),sQuery(id+"F0.wireOp",EDGE,"E4"),sQuery(id+"F0.wireOp",EDGE,"E5"),sQuery(id+"F0.wireOp",EDGE,"E6"),sQuery(id+"F0.wireOp",EDGE,"E7"),sQuery(id+"F0.wireOp",EDGE,"E8"),sQuery(id+"F0.wireOp",EDGE,"E9"),sQuery(id+"F0.wireOp",EDGE,"E10"),sQuery(id+"F0.wireOp",EDGE,"E11"),sQuery(id+"F0.wireOp",EDGE,"E12"),sQuery(id+"F0.wireOp",EDGE,"E13"),sQuery(id+"F0.wireOp",EDGE,"E14"),sQuery(id+"F0.wireOp",EDGE,"E15"),sQuery(id+"F0.wireOp",EDGE,"E16"),sQuery(id+"F0.wireOp",EDGE,"E17"),sQuery(id+"F0.wireOp",EDGE,"E18"),sQuery(id+"F0.wireOp",EDGE,"E19"),sQuery(id+"F0.wireOp",EDGE,"E20"),sQuery(id+"F0.wireOp",EDGE,"E21"),sQuery(id+"F0.wireOp",EDGE,"E22"),sQuery(id+"F0.wireOp",EDGE,"E23"),sQuery(id+"F0.wireOp",EDGE,"E24"),sQuery(id+"F0.wireOp",EDGE,"E25"),sQuery(id+"F0.wireOp",EDGE,"E26"),sQuery(id+"F0.wireOp",EDGE,"E27"),sQuery(id+"F0.wireOp",EDGE,"E28"),sQuery(id+"F0.wireOp",EDGE,"E29"),sQuery(id+"F0.wireOp",EDGE,"E30"),sQuery(id+"F0.wireOp",EDGE,"E31"),sQuery(id+"F0.wireOp",EDGE,"E32"),sQuery(id+"F0.wireOp",EDGE,"E33"),sQuery(id+"F0.wireOp",EDGE,"E34"),sQuery(id+"F0.wireOp",EDGE,"E35"),sQuery(id+"F0.wireOp",EDGE,"E36"),sQuery(id+"F0.wireOp",EDGE,"E37"),sQuery(id+"F0.wireOp",EDGE,"E38"),sQuery(id+"F0.wireOp",EDGE,"E39"),sQuery(id+"F0.wireOp",EDGE,"E40"),sQuery(id+"F0.wireOp",EDGE,"E41"),sQuery(id+"F0.wireOp",EDGE,"E42"),sQuery(id+"F0.wireOp",EDGE,"E43"),sQuery(id+"F0.wireOp",EDGE,"E44"),sQuery(id+"F0.wireOp",EDGE,"E45"),sQuery(id+"F0.wireOp",EDGE,"E46"),sQuery(id+"F0.wireOp",EDGE,"E47"),sQuery(id+"F0.wireOp",EDGE,"E48"),sQuery(id+"F0.wireOp",EDGE,"E49"),sQuery(id+"F0.wireOp",EDGE,"E50"),sQuery(id+"F0.wireOp",EDGE,"E51"),sQuery(id+"F0.wireOp",EDGE,"E52"),sQuery(id+"F0.wireOp",EDGE,"E53"),sQuery(id+"F0.wireOp",EDGE,"E54"),sQuery(id+"F0.wireOp",EDGE,"E55"),sQuery(id+"F0.wireOp",EDGE,"E56"),sQuery(id+"F0.wireOp",EDGE,"E57"),sQuery(id+"F0.wireOp",EDGE,"E58"),sQuery(id+"F0.wireOp",EDGE,"E59"),sQuery(id+"F0.wireOp",EDGE,"E60"),sQuery(id+"F0.wireOp",EDGE,"E61"),sQuery(id+"F0.wireOp",EDGE,"E62"),sQuery(id+"F0.wireOp",EDGE,"E63"),sQuery(id+"F0.wireOp",EDGE,"E64"),sQuery(id+"F0.wireOp",EDGE,"E65"),sQuery(id+"F0.wireOp",EDGE,"E66"),sQuery(id+"F0.wireOp",EDGE,"E67"),sQuery(id+"F0.wireOp",EDGE,"E68"),sQuery(id+"F0.wireOp",EDGE,"E69"),sQuery(id+"F0.wireOp",EDGE,"E70"),sQuery(id+"F0.wireOp",EDGE,"E71"),sQuery(id+"F0.wireOp",EDGE,"E72"),sQuery(id+"F0.wireOp",EDGE,"E73"),sQuery(id+"F0.wireOp",EDGE,"E74"),sQuery(id+"F0.wireOp",EDGE,"E75"),sQuery(id+"F0.wireOp",EDGE,"E76"),sQuery(id+"F0.wireOp",EDGE,"E77"),sQuery(id+"F0.wireOp",EDGE,"E78"),sQuery(id+"F0.wireOp",EDGE,"E79"),sQuery(id+"F0.wireOp",EDGE,"E80"),sQuery(id+"F0.wireOp",EDGE,"E81"),sQuery(id+"F0.wireOp",EDGE,"E82"),sQuery(id+"F0.wireOp",EDGE,"E83"),sQuery(id+"F0.wireOp",EDGE,"E84"),sQuery(id+"F0.wireOp",EDGE,"E85"),sQuery(id+"F0.wireOp",EDGE,"E86"),sQuery(id+"F0.wireOp",EDGE,"E87"),sQuery(id+"F0.wireOp",EDGE,"E88"),sQuery(id+"F0.wireOp",EDGE,"E89"),sQuery(id+"F0.wireOp",EDGE,"E90"),sQuery(id+"F0.wireOp",EDGE,"E91"),sQuery(id+"F0.wireOp",EDGE,"E92"),sQuery(id+"F0.wireOp",EDGE,"E93"),sQuery(id+"F0.wireOp",EDGE,"E94"),sQuery(id+"F0.wireOp",EDGE,"E95"),sQuery(id+"F0.wireOp",EDGE,"E96"),sQuery(id+"F0.wireOp",EDGE,"E97"),sQuery(id+"F0.wireOp",EDGE,"E98"),sQuery(id+"F0.wireOp",EDGE,"E99"),sQuery(id+"F0.wireOp",EDGE,"E100"),sQuery(id+"F0.wireOp",EDGE,"E101"),sQuery(id+"F0.wireOp",EDGE,"E102"),sQuery(id+"F0.wireOp",EDGE,"E103"),sQuery(id+"F0.wireOp",EDGE,"E104")])]}),"instanceName":"27"});
            var Q7;
            Q7=makeQuery(id+"F2.opPattern","COPY",BODY,{"derivedFrom":makeQuery(id+"F1.opExtrude","SWEPT_BODY",BODY,{"disambiguationData":[OSD([sQuery(id+"F0.wireOp",EDGE,"E1"),sQuery(id+"F0.wireOp",EDGE,"E2"),sQuery(id+"F0.wireOp",EDGE,"E3"),sQuery(id+"F0.wireOp",EDGE,"E4"),sQuery(id+"F0.wireOp",EDGE,"E5"),sQuery(id+"F0.wireOp",EDGE,"E6"),sQuery(id+"F0.wireOp",EDGE,"E7"),sQuery(id+"F0.wireOp",EDGE,"E8"),sQuery(id+"F0.wireOp",EDGE,"E9"),sQuery(id+"F0.wireOp",EDGE,"E10"),sQuery(id+"F0.wireOp",EDGE,"E11"),sQuery(id+"F0.wireOp",EDGE,"E12"),sQuery(id+"F0.wireOp",EDGE,"E13"),sQuery(id+"F0.wireOp",EDGE,"E14"),sQuery(id+"F0.wireOp",EDGE,"E15"),sQuery(id+"F0.wireOp",EDGE,"E16"),sQuery(id+"F0.wireOp",EDGE,"E17"),sQuery(id+"F0.wireOp",EDGE,"E18"),sQuery(id+"F0.wireOp",EDGE,"E19"),sQuery(id+"F0.wireOp",EDGE,"E20"),sQuery(id+"F0.wireOp",EDGE,"E21"),sQuery(id+"F0.wireOp",EDGE,"E22"),sQuery(id+"F0.wireOp",EDGE,"E23"),sQuery(id+"F0.wireOp",EDGE,"E24"),sQuery(id+"F0.wireOp",EDGE,"E25"),sQuery(id+"F0.wireOp",EDGE,"E26"),sQuery(id+"F0.wireOp",EDGE,"E27"),sQuery(id+"F0.wireOp",EDGE,"E28"),sQuery(id+"F0.wireOp",EDGE,"E29"),sQuery(id+"F0.wireOp",EDGE,"E30"),sQuery(id+"F0.wireOp",EDGE,"E31"),sQuery(id+"F0.wireOp",EDGE,"E32"),sQuery(id+"F0.wireOp",EDGE,"E33"),sQuery(id+"F0.wireOp",EDGE,"E34"),sQuery(id+"F0.wireOp",EDGE,"E35"),sQuery(id+"F0.wireOp",EDGE,"E36"),sQuery(id+"F0.wireOp",EDGE,"E37"),sQuery(id+"F0.wireOp",EDGE,"E38"),sQuery(id+"F0.wireOp",EDGE,"E39"),sQuery(id+"F0.wireOp",EDGE,"E40"),sQuery(id+"F0.wireOp",EDGE,"E41"),sQuery(id+"F0.wireOp",EDGE,"E42"),sQuery(id+"F0.wireOp",EDGE,"E43"),sQuery(id+"F0.wireOp",EDGE,"E44"),sQuery(id+"F0.wireOp",EDGE,"E45"),sQuery(id+"F0.wireOp",EDGE,"E46"),sQuery(id+"F0.wireOp",EDGE,"E47"),sQuery(id+"F0.wireOp",EDGE,"E48"),sQuery(id+"F0.wireOp",EDGE,"E49"),sQuery(id+"F0.wireOp",EDGE,"E50"),sQuery(id+"F0.wireOp",EDGE,"E51"),sQuery(id+"F0.wireOp",EDGE,"E52"),sQuery(id+"F0.wireOp",EDGE,"E53"),sQuery(id+"F0.wireOp",EDGE,"E54"),sQuery(id+"F0.wireOp",EDGE,"E55"),sQuery(id+"F0.wireOp",EDGE,"E56"),sQuery(id+"F0.wireOp",EDGE,"E57"),sQuery(id+"F0.wireOp",EDGE,"E58"),sQuery(id+"F0.wireOp",EDGE,"E59"),sQuery(id+"F0.wireOp",EDGE,"E60"),sQuery(id+"F0.wireOp",EDGE,"E61"),sQuery(id+"F0.wireOp",EDGE,"E62"),sQuery(id+"F0.wireOp",EDGE,"E63"),sQuery(id+"F0.wireOp",EDGE,"E64"),sQuery(id+"F0.wireOp",EDGE,"E65"),sQuery(id+"F0.wireOp",EDGE,"E66"),sQuery(id+"F0.wireOp",EDGE,"E67"),sQuery(id+"F0.wireOp",EDGE,"E68"),sQuery(id+"F0.wireOp",EDGE,"E69"),sQuery(id+"F0.wireOp",EDGE,"E70"),sQuery(id+"F0.wireOp",EDGE,"E71"),sQuery(id+"F0.wireOp",EDGE,"E72"),sQuery(id+"F0.wireOp",EDGE,"E73"),sQuery(id+"F0.wireOp",EDGE,"E74"),sQuery(id+"F0.wireOp",EDGE,"E75"),sQuery(id+"F0.wireOp",EDGE,"E76"),sQuery(id+"F0.wireOp",EDGE,"E77"),sQuery(id+"F0.wireOp",EDGE,"E78"),sQuery(id+"F0.wireOp",EDGE,"E79"),sQuery(id+"F0.wireOp",EDGE,"E80"),sQuery(id+"F0.wireOp",EDGE,"E81"),sQuery(id+"F0.wireOp",EDGE,"E82"),sQuery(id+"F0.wireOp",EDGE,"E83"),sQuery(id+"F0.wireOp",EDGE,"E84"),sQuery(id+"F0.wireOp",EDGE,"E85"),sQuery(id+"F0.wireOp",EDGE,"E86"),sQuery(id+"F0.wireOp",EDGE,"E87"),sQuery(id+"F0.wireOp",EDGE,"E88"),sQuery(id+"F0.wireOp",EDGE,"E89"),sQuery(id+"F0.wireOp",EDGE,"E90"),sQuery(id+"F0.wireOp",EDGE,"E91"),sQuery(id+"F0.wireOp",EDGE,"E92"),sQuery(id+"F0.wireOp",EDGE,"E93"),sQuery(id+"F0.wireOp",EDGE,"E94"),sQuery(id+"F0.wireOp",EDGE,"E95"),sQuery(id+"F0.wireOp",EDGE,"E96"),sQuery(id+"F0.wireOp",EDGE,"E97"),sQuery(id+"F0.wireOp",EDGE,"E98"),sQuery(id+"F0.wireOp",EDGE,"E99"),sQuery(id+"F0.wireOp",EDGE,"E100"),sQuery(id+"F0.wireOp",EDGE,"E101"),sQuery(id+"F0.wireOp",EDGE,"E102"),sQuery(id+"F0.wireOp",EDGE,"E103"),sQuery(id+"F0.wireOp",EDGE,"E104")])]}),"instanceName":"28"});
            var Q8;
            Q8=makeQuery(id+"F2.opPattern","COPY",BODY,{"derivedFrom":makeQuery(id+"F1.opExtrude","SWEPT_BODY",BODY,{"disambiguationData":[OSD([sQuery(id+"F0.wireOp",EDGE,"E1"),sQuery(id+"F0.wireOp",EDGE,"E2"),sQuery(id+"F0.wireOp",EDGE,"E3"),sQuery(id+"F0.wireOp",EDGE,"E4"),sQuery(id+"F0.wireOp",EDGE,"E5"),sQuery(id+"F0.wireOp",EDGE,"E6"),sQuery(id+"F0.wireOp",EDGE,"E7"),sQuery(id+"F0.wireOp",EDGE,"E8"),sQuery(id+"F0.wireOp",EDGE,"E9"),sQuery(id+"F0.wireOp",EDGE,"E10"),sQuery(id+"F0.wireOp",EDGE,"E11"),sQuery(id+"F0.wireOp",EDGE,"E12"),sQuery(id+"F0.wireOp",EDGE,"E13"),sQuery(id+"F0.wireOp",EDGE,"E14"),sQuery(id+"F0.wireOp",EDGE,"E15"),sQuery(id+"F0.wireOp",EDGE,"E16"),sQuery(id+"F0.wireOp",EDGE,"E17"),sQuery(id+"F0.wireOp",EDGE,"E18"),sQuery(id+"F0.wireOp",EDGE,"E19"),sQuery(id+"F0.wireOp",EDGE,"E20"),sQuery(id+"F0.wireOp",EDGE,"E21"),sQuery(id+"F0.wireOp",EDGE,"E22"),sQuery(id+"F0.wireOp",EDGE,"E23"),sQuery(id+"F0.wireOp",EDGE,"E24"),sQuery(id+"F0.wireOp",EDGE,"E25"),sQuery(id+"F0.wireOp",EDGE,"E26"),sQuery(id+"F0.wireOp",EDGE,"E27"),sQuery(id+"F0.wireOp",EDGE,"E28"),sQuery(id+"F0.wireOp",EDGE,"E29"),sQuery(id+"F0.wireOp",EDGE,"E30"),sQuery(id+"F0.wireOp",EDGE,"E31"),sQuery(id+"F0.wireOp",EDGE,"E32"),sQuery(id+"F0.wireOp",EDGE,"E33"),sQuery(id+"F0.wireOp",EDGE,"E34"),sQuery(id+"F0.wireOp",EDGE,"E35"),sQuery(id+"F0.wireOp",EDGE,"E36"),sQuery(id+"F0.wireOp",EDGE,"E37"),sQuery(id+"F0.wireOp",EDGE,"E38"),sQuery(id+"F0.wireOp",EDGE,"E39"),sQuery(id+"F0.wireOp",EDGE,"E40"),sQuery(id+"F0.wireOp",EDGE,"E41"),sQuery(id+"F0.wireOp",EDGE,"E42"),sQuery(id+"F0.wireOp",EDGE,"E43"),sQuery(id+"F0.wireOp",EDGE,"E44"),sQuery(id+"F0.wireOp",EDGE,"E45"),sQuery(id+"F0.wireOp",EDGE,"E46"),sQuery(id+"F0.wireOp",EDGE,"E47"),sQuery(id+"F0.wireOp",EDGE,"E48"),sQuery(id+"F0.wireOp",EDGE,"E49"),sQuery(id+"F0.wireOp",EDGE,"E50"),sQuery(id+"F0.wireOp",EDGE,"E51"),sQuery(id+"F0.wireOp",EDGE,"E52"),sQuery(id+"F0.wireOp",EDGE,"E53"),sQuery(id+"F0.wireOp",EDGE,"E54"),sQuery(id+"F0.wireOp",EDGE,"E55"),sQuery(id+"F0.wireOp",EDGE,"E56"),sQuery(id+"F0.wireOp",EDGE,"E57"),sQuery(id+"F0.wireOp",EDGE,"E58"),sQuery(id+"F0.wireOp",EDGE,"E59"),sQuery(id+"F0.wireOp",EDGE,"E60"),sQuery(id+"F0.wireOp",EDGE,"E61"),sQuery(id+"F0.wireOp",EDGE,"E62"),sQuery(id+"F0.wireOp",EDGE,"E63"),sQuery(id+"F0.wireOp",EDGE,"E64"),sQuery(id+"F0.wireOp",EDGE,"E65"),sQuery(id+"F0.wireOp",EDGE,"E66"),sQuery(id+"F0.wireOp",EDGE,"E67"),sQuery(id+"F0.wireOp",EDGE,"E68"),sQuery(id+"F0.wireOp",EDGE,"E69"),sQuery(id+"F0.wireOp",EDGE,"E70"),sQuery(id+"F0.wireOp",EDGE,"E71"),sQuery(id+"F0.wireOp",EDGE,"E72"),sQuery(id+"F0.wireOp",EDGE,"E73"),sQuery(id+"F0.wireOp",EDGE,"E74"),sQuery(id+"F0.wireOp",EDGE,"E75"),sQuery(id+"F0.wireOp",EDGE,"E76"),sQuery(id+"F0.wireOp",EDGE,"E77"),sQuery(id+"F0.wireOp",EDGE,"E78"),sQuery(id+"F0.wireOp",EDGE,"E79"),sQuery(id+"F0.wireOp",EDGE,"E80"),sQuery(id+"F0.wireOp",EDGE,"E81"),sQuery(id+"F0.wireOp",EDGE,"E82"),sQuery(id+"F0.wireOp",EDGE,"E83"),sQuery(id+"F0.wireOp",EDGE,"E84"),sQuery(id+"F0.wireOp",EDGE,"E85"),sQuery(id+"F0.wireOp",EDGE,"E86"),sQuery(id+"F0.wireOp",EDGE,"E87"),sQuery(id+"F0.wireOp",EDGE,"E88"),sQuery(id+"F0.wireOp",EDGE,"E89"),sQuery(id+"F0.wireOp",EDGE,"E90"),sQuery(id+"F0.wireOp",EDGE,"E91"),sQuery(id+"F0.wireOp",EDGE,"E92"),sQuery(id+"F0.wireOp",EDGE,"E93"),sQuery(id+"F0.wireOp",EDGE,"E94"),sQuery(id+"F0.wireOp",EDGE,"E95"),sQuery(id+"F0.wireOp",EDGE,"E96"),sQuery(id+"F0.wireOp",EDGE,"E97"),sQuery(id+"F0.wireOp",EDGE,"E98"),sQuery(id+"F0.wireOp",EDGE,"E99"),sQuery(id+"F0.wireOp",EDGE,"E100"),sQuery(id+"F0.wireOp",EDGE,"E101"),sQuery(id+"F0.wireOp",EDGE,"E102"),sQuery(id+"F0.wireOp",EDGE,"E103"),sQuery(id+"F0.wireOp",EDGE,"E104")])]}),"instanceName":"29"});
            var Q9;
            Q9=makeQuery(id+"F2.opPattern","COPY",BODY,{"derivedFrom":makeQuery(id+"F1.opExtrude","SWEPT_BODY",BODY,{"disambiguationData":[OSD([sQuery(id+"F0.wireOp",EDGE,"E1"),sQuery(id+"F0.wireOp",EDGE,"E2"),sQuery(id+"F0.wireOp",EDGE,"E3"),sQuery(id+"F0.wireOp",EDGE,"E4"),sQuery(id+"F0.wireOp",EDGE,"E5"),sQuery(id+"F0.wireOp",EDGE,"E6"),sQuery(id+"F0.wireOp",EDGE,"E7"),sQuery(id+"F0.wireOp",EDGE,"E8"),sQuery(id+"F0.wireOp",EDGE,"E9"),sQuery(id+"F0.wireOp",EDGE,"E10"),sQuery(id+"F0.wireOp",EDGE,"E11"),sQuery(id+"F0.wireOp",EDGE,"E12"),sQuery(id+"F0.wireOp",EDGE,"E13"),sQuery(id+"F0.wireOp",EDGE,"E14"),sQuery(id+"F0.wireOp",EDGE,"E15"),sQuery(id+"F0.wireOp",EDGE,"E16"),sQuery(id+"F0.wireOp",EDGE,"E17"),sQuery(id+"F0.wireOp",EDGE,"E18"),sQuery(id+"F0.wireOp",EDGE,"E19"),sQuery(id+"F0.wireOp",EDGE,"E20"),sQuery(id+"F0.wireOp",EDGE,"E21"),sQuery(id+"F0.wireOp",EDGE,"E22"),sQuery(id+"F0.wireOp",EDGE,"E23"),sQuery(id+"F0.wireOp",EDGE,"E24"),sQuery(id+"F0.wireOp",EDGE,"E25"),sQuery(id+"F0.wireOp",EDGE,"E26"),sQuery(id+"F0.wireOp",EDGE,"E27"),sQuery(id+"F0.wireOp",EDGE,"E28"),sQuery(id+"F0.wireOp",EDGE,"E29"),sQuery(id+"F0.wireOp",EDGE,"E30"),sQuery(id+"F0.wireOp",EDGE,"E31"),sQuery(id+"F0.wireOp",EDGE,"E32"),sQuery(id+"F0.wireOp",EDGE,"E33"),sQuery(id+"F0.wireOp",EDGE,"E34"),sQuery(id+"F0.wireOp",EDGE,"E35"),sQuery(id+"F0.wireOp",EDGE,"E36"),sQuery(id+"F0.wireOp",EDGE,"E37"),sQuery(id+"F0.wireOp",EDGE,"E38"),sQuery(id+"F0.wireOp",EDGE,"E39"),sQuery(id+"F0.wireOp",EDGE,"E40"),sQuery(id+"F0.wireOp",EDGE,"E41"),sQuery(id+"F0.wireOp",EDGE,"E42"),sQuery(id+"F0.wireOp",EDGE,"E43"),sQuery(id+"F0.wireOp",EDGE,"E44"),sQuery(id+"F0.wireOp",EDGE,"E45"),sQuery(id+"F0.wireOp",EDGE,"E46"),sQuery(id+"F0.wireOp",EDGE,"E47"),sQuery(id+"F0.wireOp",EDGE,"E48"),sQuery(id+"F0.wireOp",EDGE,"E49"),sQuery(id+"F0.wireOp",EDGE,"E50"),sQuery(id+"F0.wireOp",EDGE,"E51"),sQuery(id+"F0.wireOp",EDGE,"E52"),sQuery(id+"F0.wireOp",EDGE,"E53"),sQuery(id+"F0.wireOp",EDGE,"E54"),sQuery(id+"F0.wireOp",EDGE,"E55"),sQuery(id+"F0.wireOp",EDGE,"E56"),sQuery(id+"F0.wireOp",EDGE,"E57"),sQuery(id+"F0.wireOp",EDGE,"E58"),sQuery(id+"F0.wireOp",EDGE,"E59"),sQuery(id+"F0.wireOp",EDGE,"E60"),sQuery(id+"F0.wireOp",EDGE,"E61"),sQuery(id+"F0.wireOp",EDGE,"E62"),sQuery(id+"F0.wireOp",EDGE,"E63"),sQuery(id+"F0.wireOp",EDGE,"E64"),sQuery(id+"F0.wireOp",EDGE,"E65"),sQuery(id+"F0.wireOp",EDGE,"E66"),sQuery(id+"F0.wireOp",EDGE,"E67"),sQuery(id+"F0.wireOp",EDGE,"E68"),sQuery(id+"F0.wireOp",EDGE,"E69"),sQuery(id+"F0.wireOp",EDGE,"E70"),sQuery(id+"F0.wireOp",EDGE,"E71"),sQuery(id+"F0.wireOp",EDGE,"E72"),sQuery(id+"F0.wireOp",EDGE,"E73"),sQuery(id+"F0.wireOp",EDGE,"E74"),sQuery(id+"F0.wireOp",EDGE,"E75"),sQuery(id+"F0.wireOp",EDGE,"E76"),sQuery(id+"F0.wireOp",EDGE,"E77"),sQuery(id+"F0.wireOp",EDGE,"E78"),sQuery(id+"F0.wireOp",EDGE,"E79"),sQuery(id+"F0.wireOp",EDGE,"E80"),sQuery(id+"F0.wireOp",EDGE,"E81"),sQuery(id+"F0.wireOp",EDGE,"E82"),sQuery(id+"F0.wireOp",EDGE,"E83"),sQuery(id+"F0.wireOp",EDGE,"E84"),sQuery(id+"F0.wireOp",EDGE,"E85"),sQuery(id+"F0.wireOp",EDGE,"E86"),sQuery(id+"F0.wireOp",EDGE,"E87"),sQuery(id+"F0.wireOp",EDGE,"E88"),sQuery(id+"F0.wireOp",EDGE,"E89"),sQuery(id+"F0.wireOp",EDGE,"E90"),sQuery(id+"F0.wireOp",EDGE,"E91"),sQuery(id+"F0.wireOp",EDGE,"E92"),sQuery(id+"F0.wireOp",EDGE,"E93"),sQuery(id+"F0.wireOp",EDGE,"E94"),sQuery(id+"F0.wireOp",EDGE,"E95"),sQuery(id+"F0.wireOp",EDGE,"E96"),sQuery(id+"F0.wireOp",EDGE,"E97"),sQuery(id+"F0.wireOp",EDGE,"E98"),sQuery(id+"F0.wireOp",EDGE,"E99"),sQuery(id+"F0.wireOp",EDGE,"E100"),sQuery(id+"F0.wireOp",EDGE,"E101"),sQuery(id+"F0.wireOp",EDGE,"E102"),sQuery(id+"F0.wireOp",EDGE,"E103"),sQuery(id+"F0.wireOp",EDGE,"E104")])]}),"instanceName":"30"});
            var Q10;
            Q10=makeQuery(id+"F2.opPattern","COPY",BODY,{"derivedFrom":makeQuery(id+"F1.opExtrude","SWEPT_BODY",BODY,{"disambiguationData":[OSD([sQuery(id+"F0.wireOp",EDGE,"E1"),sQuery(id+"F0.wireOp",EDGE,"E2"),sQuery(id+"F0.wireOp",EDGE,"E3"),sQuery(id+"F0.wireOp",EDGE,"E4"),sQuery(id+"F0.wireOp",EDGE,"E5"),sQuery(id+"F0.wireOp",EDGE,"E6"),sQuery(id+"F0.wireOp",EDGE,"E7"),sQuery(id+"F0.wireOp",EDGE,"E8"),sQuery(id+"F0.wireOp",EDGE,"E9"),sQuery(id+"F0.wireOp",EDGE,"E10"),sQuery(id+"F0.wireOp",EDGE,"E11"),sQuery(id+"F0.wireOp",EDGE,"E12"),sQuery(id+"F0.wireOp",EDGE,"E13"),sQuery(id+"F0.wireOp",EDGE,"E14"),sQuery(id+"F0.wireOp",EDGE,"E15"),sQuery(id+"F0.wireOp",EDGE,"E16"),sQuery(id+"F0.wireOp",EDGE,"E17"),sQuery(id+"F0.wireOp",EDGE,"E18"),sQuery(id+"F0.wireOp",EDGE,"E19"),sQuery(id+"F0.wireOp",EDGE,"E20"),sQuery(id+"F0.wireOp",EDGE,"E21"),sQuery(id+"F0.wireOp",EDGE,"E22"),sQuery(id+"F0.wireOp",EDGE,"E23"),sQuery(id+"F0.wireOp",EDGE,"E24"),sQuery(id+"F0.wireOp",EDGE,"E25"),sQuery(id+"F0.wireOp",EDGE,"E26"),sQuery(id+"F0.wireOp",EDGE,"E27"),sQuery(id+"F0.wireOp",EDGE,"E28"),sQuery(id+"F0.wireOp",EDGE,"E29"),sQuery(id+"F0.wireOp",EDGE,"E30"),sQuery(id+"F0.wireOp",EDGE,"E31"),sQuery(id+"F0.wireOp",EDGE,"E32"),sQuery(id+"F0.wireOp",EDGE,"E33"),sQuery(id+"F0.wireOp",EDGE,"E34"),sQuery(id+"F0.wireOp",EDGE,"E35"),sQuery(id+"F0.wireOp",EDGE,"E36"),sQuery(id+"F0.wireOp",EDGE,"E37"),sQuery(id+"F0.wireOp",EDGE,"E38"),sQuery(id+"F0.wireOp",EDGE,"E39"),sQuery(id+"F0.wireOp",EDGE,"E40"),sQuery(id+"F0.wireOp",EDGE,"E41"),sQuery(id+"F0.wireOp",EDGE,"E42"),sQuery(id+"F0.wireOp",EDGE,"E43"),sQuery(id+"F0.wireOp",EDGE,"E44"),sQuery(id+"F0.wireOp",EDGE,"E45"),sQuery(id+"F0.wireOp",EDGE,"E46"),sQuery(id+"F0.wireOp",EDGE,"E47"),sQuery(id+"F0.wireOp",EDGE,"E48"),sQuery(id+"F0.wireOp",EDGE,"E49"),sQuery(id+"F0.wireOp",EDGE,"E50"),sQuery(id+"F0.wireOp",EDGE,"E51"),sQuery(id+"F0.wireOp",EDGE,"E52"),sQuery(id+"F0.wireOp",EDGE,"E53"),sQuery(id+"F0.wireOp",EDGE,"E54"),sQuery(id+"F0.wireOp",EDGE,"E55"),sQuery(id+"F0.wireOp",EDGE,"E56"),sQuery(id+"F0.wireOp",EDGE,"E57"),sQuery(id+"F0.wireOp",EDGE,"E58"),sQuery(id+"F0.wireOp",EDGE,"E59"),sQuery(id+"F0.wireOp",EDGE,"E60"),sQuery(id+"F0.wireOp",EDGE,"E61"),sQuery(id+"F0.wireOp",EDGE,"E62"),sQuery(id+"F0.wireOp",EDGE,"E63"),sQuery(id+"F0.wireOp",EDGE,"E64"),sQuery(id+"F0.wireOp",EDGE,"E65"),sQuery(id+"F0.wireOp",EDGE,"E66"),sQuery(id+"F0.wireOp",EDGE,"E67"),sQuery(id+"F0.wireOp",EDGE,"E68"),sQuery(id+"F0.wireOp",EDGE,"E69"),sQuery(id+"F0.wireOp",EDGE,"E70"),sQuery(id+"F0.wireOp",EDGE,"E71"),sQuery(id+"F0.wireOp",EDGE,"E72"),sQuery(id+"F0.wireOp",EDGE,"E73"),sQuery(id+"F0.wireOp",EDGE,"E74"),sQuery(id+"F0.wireOp",EDGE,"E75"),sQuery(id+"F0.wireOp",EDGE,"E76"),sQuery(id+"F0.wireOp",EDGE,"E77"),sQuery(id+"F0.wireOp",EDGE,"E78"),sQuery(id+"F0.wireOp",EDGE,"E79"),sQuery(id+"F0.wireOp",EDGE,"E80"),sQuery(id+"F0.wireOp",EDGE,"E81"),sQuery(id+"F0.wireOp",EDGE,"E82"),sQuery(id+"F0.wireOp",EDGE,"E83"),sQuery(id+"F0.wireOp",EDGE,"E84"),sQuery(id+"F0.wireOp",EDGE,"E85"),sQuery(id+"F0.wireOp",EDGE,"E86"),sQuery(id+"F0.wireOp",EDGE,"E87"),sQuery(id+"F0.wireOp",EDGE,"E88"),sQuery(id+"F0.wireOp",EDGE,"E89"),sQuery(id+"F0.wireOp",EDGE,"E90"),sQuery(id+"F0.wireOp",EDGE,"E91"),sQuery(id+"F0.wireOp",EDGE,"E92"),sQuery(id+"F0.wireOp",EDGE,"E93"),sQuery(id+"F0.wireOp",EDGE,"E94"),sQuery(id+"F0.wireOp",EDGE,"E95"),sQuery(id+"F0.wireOp",EDGE,"E96"),sQuery(id+"F0.wireOp",EDGE,"E97"),sQuery(id+"F0.wireOp",EDGE,"E98"),sQuery(id+"F0.wireOp",EDGE,"E99"),sQuery(id+"F0.wireOp",EDGE,"E100"),sQuery(id+"F0.wireOp",EDGE,"E101"),sQuery(id+"F0.wireOp",EDGE,"E102"),sQuery(id+"F0.wireOp",EDGE,"E103"),sQuery(id+"F0.wireOp",EDGE,"E104")])]}),"instanceName":"31"});
            var Q11;
            Q11=makeQuery(id+"F2.opPattern","COPY",BODY,{"derivedFrom":makeQuery(id+"F1.opExtrude","SWEPT_BODY",BODY,{"disambiguationData":[OSD([sQuery(id+"F0.wireOp",EDGE,"E1"),sQuery(id+"F0.wireOp",EDGE,"E2"),sQuery(id+"F0.wireOp",EDGE,"E3"),sQuery(id+"F0.wireOp",EDGE,"E4"),sQuery(id+"F0.wireOp",EDGE,"E5"),sQuery(id+"F0.wireOp",EDGE,"E6"),sQuery(id+"F0.wireOp",EDGE,"E7"),sQuery(id+"F0.wireOp",EDGE,"E8"),sQuery(id+"F0.wireOp",EDGE,"E9"),sQuery(id+"F0.wireOp",EDGE,"E10"),sQuery(id+"F0.wireOp",EDGE,"E11"),sQuery(id+"F0.wireOp",EDGE,"E12"),sQuery(id+"F0.wireOp",EDGE,"E13"),sQuery(id+"F0.wireOp",EDGE,"E14"),sQuery(id+"F0.wireOp",EDGE,"E15"),sQuery(id+"F0.wireOp",EDGE,"E16"),sQuery(id+"F0.wireOp",EDGE,"E17"),sQuery(id+"F0.wireOp",EDGE,"E18"),sQuery(id+"F0.wireOp",EDGE,"E19"),sQuery(id+"F0.wireOp",EDGE,"E20"),sQuery(id+"F0.wireOp",EDGE,"E21"),sQuery(id+"F0.wireOp",EDGE,"E22"),sQuery(id+"F0.wireOp",EDGE,"E23"),sQuery(id+"F0.wireOp",EDGE,"E24"),sQuery(id+"F0.wireOp",EDGE,"E25"),sQuery(id+"F0.wireOp",EDGE,"E26"),sQuery(id+"F0.wireOp",EDGE,"E27"),sQuery(id+"F0.wireOp",EDGE,"E28"),sQuery(id+"F0.wireOp",EDGE,"E29"),sQuery(id+"F0.wireOp",EDGE,"E30"),sQuery(id+"F0.wireOp",EDGE,"E31"),sQuery(id+"F0.wireOp",EDGE,"E32"),sQuery(id+"F0.wireOp",EDGE,"E33"),sQuery(id+"F0.wireOp",EDGE,"E34"),sQuery(id+"F0.wireOp",EDGE,"E35"),sQuery(id+"F0.wireOp",EDGE,"E36"),sQuery(id+"F0.wireOp",EDGE,"E37"),sQuery(id+"F0.wireOp",EDGE,"E38"),sQuery(id+"F0.wireOp",EDGE,"E39"),sQuery(id+"F0.wireOp",EDGE,"E40"),sQuery(id+"F0.wireOp",EDGE,"E41"),sQuery(id+"F0.wireOp",EDGE,"E42"),sQuery(id+"F0.wireOp",EDGE,"E43"),sQuery(id+"F0.wireOp",EDGE,"E44"),sQuery(id+"F0.wireOp",EDGE,"E45"),sQuery(id+"F0.wireOp",EDGE,"E46"),sQuery(id+"F0.wireOp",EDGE,"E47"),sQuery(id+"F0.wireOp",EDGE,"E48"),sQuery(id+"F0.wireOp",EDGE,"E49"),sQuery(id+"F0.wireOp",EDGE,"E50"),sQuery(id+"F0.wireOp",EDGE,"E51"),sQuery(id+"F0.wireOp",EDGE,"E52"),sQuery(id+"F0.wireOp",EDGE,"E53"),sQuery(id+"F0.wireOp",EDGE,"E54"),sQuery(id+"F0.wireOp",EDGE,"E55"),sQuery(id+"F0.wireOp",EDGE,"E56"),sQuery(id+"F0.wireOp",EDGE,"E57"),sQuery(id+"F0.wireOp",EDGE,"E58"),sQuery(id+"F0.wireOp",EDGE,"E59"),sQuery(id+"F0.wireOp",EDGE,"E60"),sQuery(id+"F0.wireOp",EDGE,"E61"),sQuery(id+"F0.wireOp",EDGE,"E62"),sQuery(id+"F0.wireOp",EDGE,"E63"),sQuery(id+"F0.wireOp",EDGE,"E64"),sQuery(id+"F0.wireOp",EDGE,"E65"),sQuery(id+"F0.wireOp",EDGE,"E66"),sQuery(id+"F0.wireOp",EDGE,"E67"),sQuery(id+"F0.wireOp",EDGE,"E68"),sQuery(id+"F0.wireOp",EDGE,"E69"),sQuery(id+"F0.wireOp",EDGE,"E70"),sQuery(id+"F0.wireOp",EDGE,"E71"),sQuery(id+"F0.wireOp",EDGE,"E72"),sQuery(id+"F0.wireOp",EDGE,"E73"),sQuery(id+"F0.wireOp",EDGE,"E74"),sQuery(id+"F0.wireOp",EDGE,"E75"),sQuery(id+"F0.wireOp",EDGE,"E76"),sQuery(id+"F0.wireOp",EDGE,"E77"),sQuery(id+"F0.wireOp",EDGE,"E78"),sQuery(id+"F0.wireOp",EDGE,"E79"),sQuery(id+"F0.wireOp",EDGE,"E80"),sQuery(id+"F0.wireOp",EDGE,"E81"),sQuery(id+"F0.wireOp",EDGE,"E82"),sQuery(id+"F0.wireOp",EDGE,"E83"),sQuery(id+"F0.wireOp",EDGE,"E84"),sQuery(id+"F0.wireOp",EDGE,"E85"),sQuery(id+"F0.wireOp",EDGE,"E86"),sQuery(id+"F0.wireOp",EDGE,"E87"),sQuery(id+"F0.wireOp",EDGE,"E88"),sQuery(id+"F0.wireOp",EDGE,"E89"),sQuery(id+"F0.wireOp",EDGE,"E90"),sQuery(id+"F0.wireOp",EDGE,"E91"),sQuery(id+"F0.wireOp",EDGE,"E92"),sQuery(id+"F0.wireOp",EDGE,"E93"),sQuery(id+"F0.wireOp",EDGE,"E94"),sQuery(id+"F0.wireOp",EDGE,"E95"),sQuery(id+"F0.wireOp",EDGE,"E96"),sQuery(id+"F0.wireOp",EDGE,"E97"),sQuery(id+"F0.wireOp",EDGE,"E98"),sQuery(id+"F0.wireOp",EDGE,"E99"),sQuery(id+"F0.wireOp",EDGE,"E100"),sQuery(id+"F0.wireOp",EDGE,"E101"),sQuery(id+"F0.wireOp",EDGE,"E102"),sQuery(id+"F0.wireOp",EDGE,"E103"),sQuery(id+"F0.wireOp",EDGE,"E104")])]}),"instanceName":"32"});
            var Q12;
            Q12=makeQuery(id+"F2.opPattern","COPY",BODY,{"derivedFrom":makeQuery(id+"F1.opExtrude","SWEPT_BODY",BODY,{"disambiguationData":[OSD([sQuery(id+"F0.wireOp",EDGE,"E1"),sQuery(id+"F0.wireOp",EDGE,"E2"),sQuery(id+"F0.wireOp",EDGE,"E3"),sQuery(id+"F0.wireOp",EDGE,"E4"),sQuery(id+"F0.wireOp",EDGE,"E5"),sQuery(id+"F0.wireOp",EDGE,"E6"),sQuery(id+"F0.wireOp",EDGE,"E7"),sQuery(id+"F0.wireOp",EDGE,"E8"),sQuery(id+"F0.wireOp",EDGE,"E9"),sQuery(id+"F0.wireOp",EDGE,"E10"),sQuery(id+"F0.wireOp",EDGE,"E11"),sQuery(id+"F0.wireOp",EDGE,"E12"),sQuery(id+"F0.wireOp",EDGE,"E13"),sQuery(id+"F0.wireOp",EDGE,"E14"),sQuery(id+"F0.wireOp",EDGE,"E15"),sQuery(id+"F0.wireOp",EDGE,"E16"),sQuery(id+"F0.wireOp",EDGE,"E17"),sQuery(id+"F0.wireOp",EDGE,"E18"),sQuery(id+"F0.wireOp",EDGE,"E19"),sQuery(id+"F0.wireOp",EDGE,"E20"),sQuery(id+"F0.wireOp",EDGE,"E21"),sQuery(id+"F0.wireOp",EDGE,"E22"),sQuery(id+"F0.wireOp",EDGE,"E23"),sQuery(id+"F0.wireOp",EDGE,"E24"),sQuery(id+"F0.wireOp",EDGE,"E25"),sQuery(id+"F0.wireOp",EDGE,"E26"),sQuery(id+"F0.wireOp",EDGE,"E27"),sQuery(id+"F0.wireOp",EDGE,"E28"),sQuery(id+"F0.wireOp",EDGE,"E29"),sQuery(id+"F0.wireOp",EDGE,"E30"),sQuery(id+"F0.wireOp",EDGE,"E31"),sQuery(id+"F0.wireOp",EDGE,"E32"),sQuery(id+"F0.wireOp",EDGE,"E33"),sQuery(id+"F0.wireOp",EDGE,"E34"),sQuery(id+"F0.wireOp",EDGE,"E35"),sQuery(id+"F0.wireOp",EDGE,"E36"),sQuery(id+"F0.wireOp",EDGE,"E37"),sQuery(id+"F0.wireOp",EDGE,"E38"),sQuery(id+"F0.wireOp",EDGE,"E39"),sQuery(id+"F0.wireOp",EDGE,"E40"),sQuery(id+"F0.wireOp",EDGE,"E41"),sQuery(id+"F0.wireOp",EDGE,"E42"),sQuery(id+"F0.wireOp",EDGE,"E43"),sQuery(id+"F0.wireOp",EDGE,"E44"),sQuery(id+"F0.wireOp",EDGE,"E45"),sQuery(id+"F0.wireOp",EDGE,"E46"),sQuery(id+"F0.wireOp",EDGE,"E47"),sQuery(id+"F0.wireOp",EDGE,"E48"),sQuery(id+"F0.wireOp",EDGE,"E49"),sQuery(id+"F0.wireOp",EDGE,"E50"),sQuery(id+"F0.wireOp",EDGE,"E51"),sQuery(id+"F0.wireOp",EDGE,"E52"),sQuery(id+"F0.wireOp",EDGE,"E53"),sQuery(id+"F0.wireOp",EDGE,"E54"),sQuery(id+"F0.wireOp",EDGE,"E55"),sQuery(id+"F0.wireOp",EDGE,"E56"),sQuery(id+"F0.wireOp",EDGE,"E57"),sQuery(id+"F0.wireOp",EDGE,"E58"),sQuery(id+"F0.wireOp",EDGE,"E59"),sQuery(id+"F0.wireOp",EDGE,"E60"),sQuery(id+"F0.wireOp",EDGE,"E61"),sQuery(id+"F0.wireOp",EDGE,"E62"),sQuery(id+"F0.wireOp",EDGE,"E63"),sQuery(id+"F0.wireOp",EDGE,"E64"),sQuery(id+"F0.wireOp",EDGE,"E65"),sQuery(id+"F0.wireOp",EDGE,"E66"),sQuery(id+"F0.wireOp",EDGE,"E67"),sQuery(id+"F0.wireOp",EDGE,"E68"),sQuery(id+"F0.wireOp",EDGE,"E69"),sQuery(id+"F0.wireOp",EDGE,"E70"),sQuery(id+"F0.wireOp",EDGE,"E71"),sQuery(id+"F0.wireOp",EDGE,"E72"),sQuery(id+"F0.wireOp",EDGE,"E73"),sQuery(id+"F0.wireOp",EDGE,"E74"),sQuery(id+"F0.wireOp",EDGE,"E75"),sQuery(id+"F0.wireOp",EDGE,"E76"),sQuery(id+"F0.wireOp",EDGE,"E77"),sQuery(id+"F0.wireOp",EDGE,"E78"),sQuery(id+"F0.wireOp",EDGE,"E79"),sQuery(id+"F0.wireOp",EDGE,"E80"),sQuery(id+"F0.wireOp",EDGE,"E81"),sQuery(id+"F0.wireOp",EDGE,"E82"),sQuery(id+"F0.wireOp",EDGE,"E83"),sQuery(id+"F0.wireOp",EDGE,"E84"),sQuery(id+"F0.wireOp",EDGE,"E85"),sQuery(id+"F0.wireOp",EDGE,"E86"),sQuery(id+"F0.wireOp",EDGE,"E87"),sQuery(id+"F0.wireOp",EDGE,"E88"),sQuery(id+"F0.wireOp",EDGE,"E89"),sQuery(id+"F0.wireOp",EDGE,"E90"),sQuery(id+"F0.wireOp",EDGE,"E91"),sQuery(id+"F0.wireOp",EDGE,"E92"),sQuery(id+"F0.wireOp",EDGE,"E93"),sQuery(id+"F0.wireOp",EDGE,"E94"),sQuery(id+"F0.wireOp",EDGE,"E95"),sQuery(id+"F0.wireOp",EDGE,"E96"),sQuery(id+"F0.wireOp",EDGE,"E97"),sQuery(id+"F0.wireOp",EDGE,"E98"),sQuery(id+"F0.wireOp",EDGE,"E99"),sQuery(id+"F0.wireOp",EDGE,"E100"),sQuery(id+"F0.wireOp",EDGE,"E101"),sQuery(id+"F0.wireOp",EDGE,"E102"),sQuery(id+"F0.wireOp",EDGE,"E103"),sQuery(id+"F0.wireOp",EDGE,"E104")])]}),"instanceName":"33"});
            var Q13;
            Q13=makeQuery(id+"F2.opPattern","COPY",BODY,{"derivedFrom":makeQuery(id+"F1.opExtrude","SWEPT_BODY",BODY,{"disambiguationData":[OSD([sQuery(id+"F0.wireOp",EDGE,"E1"),sQuery(id+"F0.wireOp",EDGE,"E2"),sQuery(id+"F0.wireOp",EDGE,"E3"),sQuery(id+"F0.wireOp",EDGE,"E4"),sQuery(id+"F0.wireOp",EDGE,"E5"),sQuery(id+"F0.wireOp",EDGE,"E6"),sQuery(id+"F0.wireOp",EDGE,"E7"),sQuery(id+"F0.wireOp",EDGE,"E8"),sQuery(id+"F0.wireOp",EDGE,"E9"),sQuery(id+"F0.wireOp",EDGE,"E10"),sQuery(id+"F0.wireOp",EDGE,"E11"),sQuery(id+"F0.wireOp",EDGE,"E12"),sQuery(id+"F0.wireOp",EDGE,"E13"),sQuery(id+"F0.wireOp",EDGE,"E14"),sQuery(id+"F0.wireOp",EDGE,"E15"),sQuery(id+"F0.wireOp",EDGE,"E16"),sQuery(id+"F0.wireOp",EDGE,"E17"),sQuery(id+"F0.wireOp",EDGE,"E18"),sQuery(id+"F0.wireOp",EDGE,"E19"),sQuery(id+"F0.wireOp",EDGE,"E20"),sQuery(id+"F0.wireOp",EDGE,"E21"),sQuery(id+"F0.wireOp",EDGE,"E22"),sQuery(id+"F0.wireOp",EDGE,"E23"),sQuery(id+"F0.wireOp",EDGE,"E24"),sQuery(id+"F0.wireOp",EDGE,"E25"),sQuery(id+"F0.wireOp",EDGE,"E26"),sQuery(id+"F0.wireOp",EDGE,"E27"),sQuery(id+"F0.wireOp",EDGE,"E28"),sQuery(id+"F0.wireOp",EDGE,"E29"),sQuery(id+"F0.wireOp",EDGE,"E30"),sQuery(id+"F0.wireOp",EDGE,"E31"),sQuery(id+"F0.wireOp",EDGE,"E32"),sQuery(id+"F0.wireOp",EDGE,"E33"),sQuery(id+"F0.wireOp",EDGE,"E34"),sQuery(id+"F0.wireOp",EDGE,"E35"),sQuery(id+"F0.wireOp",EDGE,"E36"),sQuery(id+"F0.wireOp",EDGE,"E37"),sQuery(id+"F0.wireOp",EDGE,"E38"),sQuery(id+"F0.wireOp",EDGE,"E39"),sQuery(id+"F0.wireOp",EDGE,"E40"),sQuery(id+"F0.wireOp",EDGE,"E41"),sQuery(id+"F0.wireOp",EDGE,"E42"),sQuery(id+"F0.wireOp",EDGE,"E43"),sQuery(id+"F0.wireOp",EDGE,"E44"),sQuery(id+"F0.wireOp",EDGE,"E45"),sQuery(id+"F0.wireOp",EDGE,"E46"),sQuery(id+"F0.wireOp",EDGE,"E47"),sQuery(id+"F0.wireOp",EDGE,"E48"),sQuery(id+"F0.wireOp",EDGE,"E49"),sQuery(id+"F0.wireOp",EDGE,"E50"),sQuery(id+"F0.wireOp",EDGE,"E51"),sQuery(id+"F0.wireOp",EDGE,"E52"),sQuery(id+"F0.wireOp",EDGE,"E53"),sQuery(id+"F0.wireOp",EDGE,"E54"),sQuery(id+"F0.wireOp",EDGE,"E55"),sQuery(id+"F0.wireOp",EDGE,"E56"),sQuery(id+"F0.wireOp",EDGE,"E57"),sQuery(id+"F0.wireOp",EDGE,"E58"),sQuery(id+"F0.wireOp",EDGE,"E59"),sQuery(id+"F0.wireOp",EDGE,"E60"),sQuery(id+"F0.wireOp",EDGE,"E61"),sQuery(id+"F0.wireOp",EDGE,"E62"),sQuery(id+"F0.wireOp",EDGE,"E63"),sQuery(id+"F0.wireOp",EDGE,"E64"),sQuery(id+"F0.wireOp",EDGE,"E65"),sQuery(id+"F0.wireOp",EDGE,"E66"),sQuery(id+"F0.wireOp",EDGE,"E67"),sQuery(id+"F0.wireOp",EDGE,"E68"),sQuery(id+"F0.wireOp",EDGE,"E69"),sQuery(id+"F0.wireOp",EDGE,"E70"),sQuery(id+"F0.wireOp",EDGE,"E71"),sQuery(id+"F0.wireOp",EDGE,"E72"),sQuery(id+"F0.wireOp",EDGE,"E73"),sQuery(id+"F0.wireOp",EDGE,"E74"),sQuery(id+"F0.wireOp",EDGE,"E75"),sQuery(id+"F0.wireOp",EDGE,"E76"),sQuery(id+"F0.wireOp",EDGE,"E77"),sQuery(id+"F0.wireOp",EDGE,"E78"),sQuery(id+"F0.wireOp",EDGE,"E79"),sQuery(id+"F0.wireOp",EDGE,"E80"),sQuery(id+"F0.wireOp",EDGE,"E81"),sQuery(id+"F0.wireOp",EDGE,"E82"),sQuery(id+"F0.wireOp",EDGE,"E83"),sQuery(id+"F0.wireOp",EDGE,"E84"),sQuery(id+"F0.wireOp",EDGE,"E85"),sQuery(id+"F0.wireOp",EDGE,"E86"),sQuery(id+"F0.wireOp",EDGE,"E87"),sQuery(id+"F0.wireOp",EDGE,"E88"),sQuery(id+"F0.wireOp",EDGE,"E89"),sQuery(id+"F0.wireOp",EDGE,"E90"),sQuery(id+"F0.wireOp",EDGE,"E91"),sQuery(id+"F0.wireOp",EDGE,"E92"),sQuery(id+"F0.wireOp",EDGE,"E93"),sQuery(id+"F0.wireOp",EDGE,"E94"),sQuery(id+"F0.wireOp",EDGE,"E95"),sQuery(id+"F0.wireOp",EDGE,"E96"),sQuery(id+"F0.wireOp",EDGE,"E97"),sQuery(id+"F0.wireOp",EDGE,"E98"),sQuery(id+"F0.wireOp",EDGE,"E99"),sQuery(id+"F0.wireOp",EDGE,"E100"),sQuery(id+"F0.wireOp",EDGE,"E101"),sQuery(id+"F0.wireOp",EDGE,"E102"),sQuery(id+"F0.wireOp",EDGE,"E103"),sQuery(id+"F0.wireOp",EDGE,"E104")])]}),"instanceName":"34"});
            booleanBodies(context, id + "F4", {"operationType" : BooleanOperationType.UNION, "tools" : qUnion([Q0, Q1, Q2, Q3, Q4, Q5, Q6, Q7, Q8, Q9, Q10, Q11, Q12, Q13])});
        }
        {
            var Q0;
            Q0=makeQuery(id+"F1.opExtrude","SWEPT_BODY",BODY,{"disambiguationData":[OSD([sQuery(id+"F0.wireOp",EDGE,"E105")])]});
            var Q1;
            Q1=makeQuery(id+"F2.opPattern","COPY",BODY,{"derivedFrom":makeQuery(id+"F1.opExtrude","SWEPT_BODY",BODY,{"disambiguationData":[OSD([sQuery(id+"F0.wireOp",EDGE,"E1"),sQuery(id+"F0.wireOp",EDGE,"E2"),sQuery(id+"F0.wireOp",EDGE,"E3"),sQuery(id+"F0.wireOp",EDGE,"E4"),sQuery(id+"F0.wireOp",EDGE,"E5"),sQuery(id+"F0.wireOp",EDGE,"E6"),sQuery(id+"F0.wireOp",EDGE,"E7"),sQuery(id+"F0.wireOp",EDGE,"E8"),sQuery(id+"F0.wireOp",EDGE,"E9"),sQuery(id+"F0.wireOp",EDGE,"E10"),sQuery(id+"F0.wireOp",EDGE,"E11"),sQuery(id+"F0.wireOp",EDGE,"E12"),sQuery(id+"F0.wireOp",EDGE,"E13"),sQuery(id+"F0.wireOp",EDGE,"E14"),sQuery(id+"F0.wireOp",EDGE,"E15"),sQuery(id+"F0.wireOp",EDGE,"E16"),sQuery(id+"F0.wireOp",EDGE,"E17"),sQuery(id+"F0.wireOp",EDGE,"E18"),sQuery(id+"F0.wireOp",EDGE,"E19"),sQuery(id+"F0.wireOp",EDGE,"E20"),sQuery(id+"F0.wireOp",EDGE,"E21"),sQuery(id+"F0.wireOp",EDGE,"E22"),sQuery(id+"F0.wireOp",EDGE,"E23"),sQuery(id+"F0.wireOp",EDGE,"E24"),sQuery(id+"F0.wireOp",EDGE,"E25"),sQuery(id+"F0.wireOp",EDGE,"E26"),sQuery(id+"F0.wireOp",EDGE,"E27"),sQuery(id+"F0.wireOp",EDGE,"E28"),sQuery(id+"F0.wireOp",EDGE,"E29"),sQuery(id+"F0.wireOp",EDGE,"E30"),sQuery(id+"F0.wireOp",EDGE,"E31"),sQuery(id+"F0.wireOp",EDGE,"E32"),sQuery(id+"F0.wireOp",EDGE,"E33"),sQuery(id+"F0.wireOp",EDGE,"E34"),sQuery(id+"F0.wireOp",EDGE,"E35"),sQuery(id+"F0.wireOp",EDGE,"E36"),sQuery(id+"F0.wireOp",EDGE,"E37"),sQuery(id+"F0.wireOp",EDGE,"E38"),sQuery(id+"F0.wireOp",EDGE,"E39"),sQuery(id+"F0.wireOp",EDGE,"E40"),sQuery(id+"F0.wireOp",EDGE,"E41"),sQuery(id+"F0.wireOp",EDGE,"E42"),sQuery(id+"F0.wireOp",EDGE,"E43"),sQuery(id+"F0.wireOp",EDGE,"E44"),sQuery(id+"F0.wireOp",EDGE,"E45"),sQuery(id+"F0.wireOp",EDGE,"E46"),sQuery(id+"F0.wireOp",EDGE,"E47"),sQuery(id+"F0.wireOp",EDGE,"E48"),sQuery(id+"F0.wireOp",EDGE,"E49"),sQuery(id+"F0.wireOp",EDGE,"E50"),sQuery(id+"F0.wireOp",EDGE,"E51"),sQuery(id+"F0.wireOp",EDGE,"E52"),sQuery(id+"F0.wireOp",EDGE,"E53"),sQuery(id+"F0.wireOp",EDGE,"E54"),sQuery(id+"F0.wireOp",EDGE,"E55"),sQuery(id+"F0.wireOp",EDGE,"E56"),sQuery(id+"F0.wireOp",EDGE,"E57"),sQuery(id+"F0.wireOp",EDGE,"E58"),sQuery(id+"F0.wireOp",EDGE,"E59"),sQuery(id+"F0.wireOp",EDGE,"E60"),sQuery(id+"F0.wireOp",EDGE,"E61"),sQuery(id+"F0.wireOp",EDGE,"E62"),sQuery(id+"F0.wireOp",EDGE,"E63"),sQuery(id+"F0.wireOp",EDGE,"E64"),sQuery(id+"F0.wireOp",EDGE,"E65"),sQuery(id+"F0.wireOp",EDGE,"E66"),sQuery(id+"F0.wireOp",EDGE,"E67"),sQuery(id+"F0.wireOp",EDGE,"E68"),sQuery(id+"F0.wireOp",EDGE,"E69"),sQuery(id+"F0.wireOp",EDGE,"E70"),sQuery(id+"F0.wireOp",EDGE,"E71"),sQuery(id+"F0.wireOp",EDGE,"E72"),sQuery(id+"F0.wireOp",EDGE,"E73"),sQuery(id+"F0.wireOp",EDGE,"E74"),sQuery(id+"F0.wireOp",EDGE,"E75"),sQuery(id+"F0.wireOp",EDGE,"E76"),sQuery(id+"F0.wireOp",EDGE,"E77"),sQuery(id+"F0.wireOp",EDGE,"E78"),sQuery(id+"F0.wireOp",EDGE,"E79"),sQuery(id+"F0.wireOp",EDGE,"E80"),sQuery(id+"F0.wireOp",EDGE,"E81"),sQuery(id+"F0.wireOp",EDGE,"E82"),sQuery(id+"F0.wireOp",EDGE,"E83"),sQuery(id+"F0.wireOp",EDGE,"E84"),sQuery(id+"F0.wireOp",EDGE,"E85"),sQuery(id+"F0.wireOp",EDGE,"E86"),sQuery(id+"F0.wireOp",EDGE,"E87"),sQuery(id+"F0.wireOp",EDGE,"E88"),sQuery(id+"F0.wireOp",EDGE,"E89"),sQuery(id+"F0.wireOp",EDGE,"E90"),sQuery(id+"F0.wireOp",EDGE,"E91"),sQuery(id+"F0.wireOp",EDGE,"E92"),sQuery(id+"F0.wireOp",EDGE,"E93"),sQuery(id+"F0.wireOp",EDGE,"E94"),sQuery(id+"F0.wireOp",EDGE,"E95"),sQuery(id+"F0.wireOp",EDGE,"E96"),sQuery(id+"F0.wireOp",EDGE,"E97"),sQuery(id+"F0.wireOp",EDGE,"E98"),sQuery(id+"F0.wireOp",EDGE,"E99"),sQuery(id+"F0.wireOp",EDGE,"E100"),sQuery(id+"F0.wireOp",EDGE,"E101"),sQuery(id+"F0.wireOp",EDGE,"E102"),sQuery(id+"F0.wireOp",EDGE,"E103"),sQuery(id+"F0.wireOp",EDGE,"E104")])]}),"instanceName":"1"});
            var Q2;
            Q2=makeQuery(id+"F2.opPattern","COPY",BODY,{"derivedFrom":makeQuery(id+"F1.opExtrude","SWEPT_BODY",BODY,{"disambiguationData":[OSD([sQuery(id+"F0.wireOp",EDGE,"E1"),sQuery(id+"F0.wireOp",EDGE,"E2"),sQuery(id+"F0.wireOp",EDGE,"E3"),sQuery(id+"F0.wireOp",EDGE,"E4"),sQuery(id+"F0.wireOp",EDGE,"E5"),sQuery(id+"F0.wireOp",EDGE,"E6"),sQuery(id+"F0.wireOp",EDGE,"E7"),sQuery(id+"F0.wireOp",EDGE,"E8"),sQuery(id+"F0.wireOp",EDGE,"E9"),sQuery(id+"F0.wireOp",EDGE,"E10"),sQuery(id+"F0.wireOp",EDGE,"E11"),sQuery(id+"F0.wireOp",EDGE,"E12"),sQuery(id+"F0.wireOp",EDGE,"E13"),sQuery(id+"F0.wireOp",EDGE,"E14"),sQuery(id+"F0.wireOp",EDGE,"E15"),sQuery(id+"F0.wireOp",EDGE,"E16"),sQuery(id+"F0.wireOp",EDGE,"E17"),sQuery(id+"F0.wireOp",EDGE,"E18"),sQuery(id+"F0.wireOp",EDGE,"E19"),sQuery(id+"F0.wireOp",EDGE,"E20"),sQuery(id+"F0.wireOp",EDGE,"E21"),sQuery(id+"F0.wireOp",EDGE,"E22"),sQuery(id+"F0.wireOp",EDGE,"E23"),sQuery(id+"F0.wireOp",EDGE,"E24"),sQuery(id+"F0.wireOp",EDGE,"E25"),sQuery(id+"F0.wireOp",EDGE,"E26"),sQuery(id+"F0.wireOp",EDGE,"E27"),sQuery(id+"F0.wireOp",EDGE,"E28"),sQuery(id+"F0.wireOp",EDGE,"E29"),sQuery(id+"F0.wireOp",EDGE,"E30"),sQuery(id+"F0.wireOp",EDGE,"E31"),sQuery(id+"F0.wireOp",EDGE,"E32"),sQuery(id+"F0.wireOp",EDGE,"E33"),sQuery(id+"F0.wireOp",EDGE,"E34"),sQuery(id+"F0.wireOp",EDGE,"E35"),sQuery(id+"F0.wireOp",EDGE,"E36"),sQuery(id+"F0.wireOp",EDGE,"E37"),sQuery(id+"F0.wireOp",EDGE,"E38"),sQuery(id+"F0.wireOp",EDGE,"E39"),sQuery(id+"F0.wireOp",EDGE,"E40"),sQuery(id+"F0.wireOp",EDGE,"E41"),sQuery(id+"F0.wireOp",EDGE,"E42"),sQuery(id+"F0.wireOp",EDGE,"E43"),sQuery(id+"F0.wireOp",EDGE,"E44"),sQuery(id+"F0.wireOp",EDGE,"E45"),sQuery(id+"F0.wireOp",EDGE,"E46"),sQuery(id+"F0.wireOp",EDGE,"E47"),sQuery(id+"F0.wireOp",EDGE,"E48"),sQuery(id+"F0.wireOp",EDGE,"E49"),sQuery(id+"F0.wireOp",EDGE,"E50"),sQuery(id+"F0.wireOp",EDGE,"E51"),sQuery(id+"F0.wireOp",EDGE,"E52"),sQuery(id+"F0.wireOp",EDGE,"E53"),sQuery(id+"F0.wireOp",EDGE,"E54"),sQuery(id+"F0.wireOp",EDGE,"E55"),sQuery(id+"F0.wireOp",EDGE,"E56"),sQuery(id+"F0.wireOp",EDGE,"E57"),sQuery(id+"F0.wireOp",EDGE,"E58"),sQuery(id+"F0.wireOp",EDGE,"E59"),sQuery(id+"F0.wireOp",EDGE,"E60"),sQuery(id+"F0.wireOp",EDGE,"E61"),sQuery(id+"F0.wireOp",EDGE,"E62"),sQuery(id+"F0.wireOp",EDGE,"E63"),sQuery(id+"F0.wireOp",EDGE,"E64"),sQuery(id+"F0.wireOp",EDGE,"E65"),sQuery(id+"F0.wireOp",EDGE,"E66"),sQuery(id+"F0.wireOp",EDGE,"E67"),sQuery(id+"F0.wireOp",EDGE,"E68"),sQuery(id+"F0.wireOp",EDGE,"E69"),sQuery(id+"F0.wireOp",EDGE,"E70"),sQuery(id+"F0.wireOp",EDGE,"E71"),sQuery(id+"F0.wireOp",EDGE,"E72"),sQuery(id+"F0.wireOp",EDGE,"E73"),sQuery(id+"F0.wireOp",EDGE,"E74"),sQuery(id+"F0.wireOp",EDGE,"E75"),sQuery(id+"F0.wireOp",EDGE,"E76"),sQuery(id+"F0.wireOp",EDGE,"E77"),sQuery(id+"F0.wireOp",EDGE,"E78"),sQuery(id+"F0.wireOp",EDGE,"E79"),sQuery(id+"F0.wireOp",EDGE,"E80"),sQuery(id+"F0.wireOp",EDGE,"E81"),sQuery(id+"F0.wireOp",EDGE,"E82"),sQuery(id+"F0.wireOp",EDGE,"E83"),sQuery(id+"F0.wireOp",EDGE,"E84"),sQuery(id+"F0.wireOp",EDGE,"E85"),sQuery(id+"F0.wireOp",EDGE,"E86"),sQuery(id+"F0.wireOp",EDGE,"E87"),sQuery(id+"F0.wireOp",EDGE,"E88"),sQuery(id+"F0.wireOp",EDGE,"E89"),sQuery(id+"F0.wireOp",EDGE,"E90"),sQuery(id+"F0.wireOp",EDGE,"E91"),sQuery(id+"F0.wireOp",EDGE,"E92"),sQuery(id+"F0.wireOp",EDGE,"E93"),sQuery(id+"F0.wireOp",EDGE,"E94"),sQuery(id+"F0.wireOp",EDGE,"E95"),sQuery(id+"F0.wireOp",EDGE,"E96"),sQuery(id+"F0.wireOp",EDGE,"E97"),sQuery(id+"F0.wireOp",EDGE,"E98"),sQuery(id+"F0.wireOp",EDGE,"E99"),sQuery(id+"F0.wireOp",EDGE,"E100"),sQuery(id+"F0.wireOp",EDGE,"E101"),sQuery(id+"F0.wireOp",EDGE,"E102"),sQuery(id+"F0.wireOp",EDGE,"E103"),sQuery(id+"F0.wireOp",EDGE,"E104")])]}),"instanceName":"35"});
            var Q3;
            Q3=makeQuery(id+"F2.opPattern","COPY",BODY,{"derivedFrom":makeQuery(id+"F1.opExtrude","SWEPT_BODY",BODY,{"disambiguationData":[OSD([sQuery(id+"F0.wireOp",EDGE,"E1"),sQuery(id+"F0.wireOp",EDGE,"E2"),sQuery(id+"F0.wireOp",EDGE,"E3"),sQuery(id+"F0.wireOp",EDGE,"E4"),sQuery(id+"F0.wireOp",EDGE,"E5"),sQuery(id+"F0.wireOp",EDGE,"E6"),sQuery(id+"F0.wireOp",EDGE,"E7"),sQuery(id+"F0.wireOp",EDGE,"E8"),sQuery(id+"F0.wireOp",EDGE,"E9"),sQuery(id+"F0.wireOp",EDGE,"E10"),sQuery(id+"F0.wireOp",EDGE,"E11"),sQuery(id+"F0.wireOp",EDGE,"E12"),sQuery(id+"F0.wireOp",EDGE,"E13"),sQuery(id+"F0.wireOp",EDGE,"E14"),sQuery(id+"F0.wireOp",EDGE,"E15"),sQuery(id+"F0.wireOp",EDGE,"E16"),sQuery(id+"F0.wireOp",EDGE,"E17"),sQuery(id+"F0.wireOp",EDGE,"E18"),sQuery(id+"F0.wireOp",EDGE,"E19"),sQuery(id+"F0.wireOp",EDGE,"E20"),sQuery(id+"F0.wireOp",EDGE,"E21"),sQuery(id+"F0.wireOp",EDGE,"E22"),sQuery(id+"F0.wireOp",EDGE,"E23"),sQuery(id+"F0.wireOp",EDGE,"E24"),sQuery(id+"F0.wireOp",EDGE,"E25"),sQuery(id+"F0.wireOp",EDGE,"E26"),sQuery(id+"F0.wireOp",EDGE,"E27"),sQuery(id+"F0.wireOp",EDGE,"E28"),sQuery(id+"F0.wireOp",EDGE,"E29"),sQuery(id+"F0.wireOp",EDGE,"E30"),sQuery(id+"F0.wireOp",EDGE,"E31"),sQuery(id+"F0.wireOp",EDGE,"E32"),sQuery(id+"F0.wireOp",EDGE,"E33"),sQuery(id+"F0.wireOp",EDGE,"E34"),sQuery(id+"F0.wireOp",EDGE,"E35"),sQuery(id+"F0.wireOp",EDGE,"E36"),sQuery(id+"F0.wireOp",EDGE,"E37"),sQuery(id+"F0.wireOp",EDGE,"E38"),sQuery(id+"F0.wireOp",EDGE,"E39"),sQuery(id+"F0.wireOp",EDGE,"E40"),sQuery(id+"F0.wireOp",EDGE,"E41"),sQuery(id+"F0.wireOp",EDGE,"E42"),sQuery(id+"F0.wireOp",EDGE,"E43"),sQuery(id+"F0.wireOp",EDGE,"E44"),sQuery(id+"F0.wireOp",EDGE,"E45"),sQuery(id+"F0.wireOp",EDGE,"E46"),sQuery(id+"F0.wireOp",EDGE,"E47"),sQuery(id+"F0.wireOp",EDGE,"E48"),sQuery(id+"F0.wireOp",EDGE,"E49"),sQuery(id+"F0.wireOp",EDGE,"E50"),sQuery(id+"F0.wireOp",EDGE,"E51"),sQuery(id+"F0.wireOp",EDGE,"E52"),sQuery(id+"F0.wireOp",EDGE,"E53"),sQuery(id+"F0.wireOp",EDGE,"E54"),sQuery(id+"F0.wireOp",EDGE,"E55"),sQuery(id+"F0.wireOp",EDGE,"E56"),sQuery(id+"F0.wireOp",EDGE,"E57"),sQuery(id+"F0.wireOp",EDGE,"E58"),sQuery(id+"F0.wireOp",EDGE,"E59"),sQuery(id+"F0.wireOp",EDGE,"E60"),sQuery(id+"F0.wireOp",EDGE,"E61"),sQuery(id+"F0.wireOp",EDGE,"E62"),sQuery(id+"F0.wireOp",EDGE,"E63"),sQuery(id+"F0.wireOp",EDGE,"E64"),sQuery(id+"F0.wireOp",EDGE,"E65"),sQuery(id+"F0.wireOp",EDGE,"E66"),sQuery(id+"F0.wireOp",EDGE,"E67"),sQuery(id+"F0.wireOp",EDGE,"E68"),sQuery(id+"F0.wireOp",EDGE,"E69"),sQuery(id+"F0.wireOp",EDGE,"E70"),sQuery(id+"F0.wireOp",EDGE,"E71"),sQuery(id+"F0.wireOp",EDGE,"E72"),sQuery(id+"F0.wireOp",EDGE,"E73"),sQuery(id+"F0.wireOp",EDGE,"E74"),sQuery(id+"F0.wireOp",EDGE,"E75"),sQuery(id+"F0.wireOp",EDGE,"E76"),sQuery(id+"F0.wireOp",EDGE,"E77"),sQuery(id+"F0.wireOp",EDGE,"E78"),sQuery(id+"F0.wireOp",EDGE,"E79"),sQuery(id+"F0.wireOp",EDGE,"E80"),sQuery(id+"F0.wireOp",EDGE,"E81"),sQuery(id+"F0.wireOp",EDGE,"E82"),sQuery(id+"F0.wireOp",EDGE,"E83"),sQuery(id+"F0.wireOp",EDGE,"E84"),sQuery(id+"F0.wireOp",EDGE,"E85"),sQuery(id+"F0.wireOp",EDGE,"E86"),sQuery(id+"F0.wireOp",EDGE,"E87"),sQuery(id+"F0.wireOp",EDGE,"E88"),sQuery(id+"F0.wireOp",EDGE,"E89"),sQuery(id+"F0.wireOp",EDGE,"E90"),sQuery(id+"F0.wireOp",EDGE,"E91"),sQuery(id+"F0.wireOp",EDGE,"E92"),sQuery(id+"F0.wireOp",EDGE,"E93"),sQuery(id+"F0.wireOp",EDGE,"E94"),sQuery(id+"F0.wireOp",EDGE,"E95"),sQuery(id+"F0.wireOp",EDGE,"E96"),sQuery(id+"F0.wireOp",EDGE,"E97"),sQuery(id+"F0.wireOp",EDGE,"E98"),sQuery(id+"F0.wireOp",EDGE,"E99"),sQuery(id+"F0.wireOp",EDGE,"E100"),sQuery(id+"F0.wireOp",EDGE,"E101"),sQuery(id+"F0.wireOp",EDGE,"E102"),sQuery(id+"F0.wireOp",EDGE,"E103"),sQuery(id+"F0.wireOp",EDGE,"E104")])]}),"instanceName":"36"});
            var Q4;
            Q4=makeQuery(id+"F2.opPattern","COPY",BODY,{"derivedFrom":makeQuery(id+"F1.opExtrude","SWEPT_BODY",BODY,{"disambiguationData":[OSD([sQuery(id+"F0.wireOp",EDGE,"E1"),sQuery(id+"F0.wireOp",EDGE,"E2"),sQuery(id+"F0.wireOp",EDGE,"E3"),sQuery(id+"F0.wireOp",EDGE,"E4"),sQuery(id+"F0.wireOp",EDGE,"E5"),sQuery(id+"F0.wireOp",EDGE,"E6"),sQuery(id+"F0.wireOp",EDGE,"E7"),sQuery(id+"F0.wireOp",EDGE,"E8"),sQuery(id+"F0.wireOp",EDGE,"E9"),sQuery(id+"F0.wireOp",EDGE,"E10"),sQuery(id+"F0.wireOp",EDGE,"E11"),sQuery(id+"F0.wireOp",EDGE,"E12"),sQuery(id+"F0.wireOp",EDGE,"E13"),sQuery(id+"F0.wireOp",EDGE,"E14"),sQuery(id+"F0.wireOp",EDGE,"E15"),sQuery(id+"F0.wireOp",EDGE,"E16"),sQuery(id+"F0.wireOp",EDGE,"E17"),sQuery(id+"F0.wireOp",EDGE,"E18"),sQuery(id+"F0.wireOp",EDGE,"E19"),sQuery(id+"F0.wireOp",EDGE,"E20"),sQuery(id+"F0.wireOp",EDGE,"E21"),sQuery(id+"F0.wireOp",EDGE,"E22"),sQuery(id+"F0.wireOp",EDGE,"E23"),sQuery(id+"F0.wireOp",EDGE,"E24"),sQuery(id+"F0.wireOp",EDGE,"E25"),sQuery(id+"F0.wireOp",EDGE,"E26"),sQuery(id+"F0.wireOp",EDGE,"E27"),sQuery(id+"F0.wireOp",EDGE,"E28"),sQuery(id+"F0.wireOp",EDGE,"E29"),sQuery(id+"F0.wireOp",EDGE,"E30"),sQuery(id+"F0.wireOp",EDGE,"E31"),sQuery(id+"F0.wireOp",EDGE,"E32"),sQuery(id+"F0.wireOp",EDGE,"E33"),sQuery(id+"F0.wireOp",EDGE,"E34"),sQuery(id+"F0.wireOp",EDGE,"E35"),sQuery(id+"F0.wireOp",EDGE,"E36"),sQuery(id+"F0.wireOp",EDGE,"E37"),sQuery(id+"F0.wireOp",EDGE,"E38"),sQuery(id+"F0.wireOp",EDGE,"E39"),sQuery(id+"F0.wireOp",EDGE,"E40"),sQuery(id+"F0.wireOp",EDGE,"E41"),sQuery(id+"F0.wireOp",EDGE,"E42"),sQuery(id+"F0.wireOp",EDGE,"E43"),sQuery(id+"F0.wireOp",EDGE,"E44"),sQuery(id+"F0.wireOp",EDGE,"E45"),sQuery(id+"F0.wireOp",EDGE,"E46"),sQuery(id+"F0.wireOp",EDGE,"E47"),sQuery(id+"F0.wireOp",EDGE,"E48"),sQuery(id+"F0.wireOp",EDGE,"E49"),sQuery(id+"F0.wireOp",EDGE,"E50"),sQuery(id+"F0.wireOp",EDGE,"E51"),sQuery(id+"F0.wireOp",EDGE,"E52"),sQuery(id+"F0.wireOp",EDGE,"E53"),sQuery(id+"F0.wireOp",EDGE,"E54"),sQuery(id+"F0.wireOp",EDGE,"E55"),sQuery(id+"F0.wireOp",EDGE,"E56"),sQuery(id+"F0.wireOp",EDGE,"E57"),sQuery(id+"F0.wireOp",EDGE,"E58"),sQuery(id+"F0.wireOp",EDGE,"E59"),sQuery(id+"F0.wireOp",EDGE,"E60"),sQuery(id+"F0.wireOp",EDGE,"E61"),sQuery(id+"F0.wireOp",EDGE,"E62"),sQuery(id+"F0.wireOp",EDGE,"E63"),sQuery(id+"F0.wireOp",EDGE,"E64"),sQuery(id+"F0.wireOp",EDGE,"E65"),sQuery(id+"F0.wireOp",EDGE,"E66"),sQuery(id+"F0.wireOp",EDGE,"E67"),sQuery(id+"F0.wireOp",EDGE,"E68"),sQuery(id+"F0.wireOp",EDGE,"E69"),sQuery(id+"F0.wireOp",EDGE,"E70"),sQuery(id+"F0.wireOp",EDGE,"E71"),sQuery(id+"F0.wireOp",EDGE,"E72"),sQuery(id+"F0.wireOp",EDGE,"E73"),sQuery(id+"F0.wireOp",EDGE,"E74"),sQuery(id+"F0.wireOp",EDGE,"E75"),sQuery(id+"F0.wireOp",EDGE,"E76"),sQuery(id+"F0.wireOp",EDGE,"E77"),sQuery(id+"F0.wireOp",EDGE,"E78"),sQuery(id+"F0.wireOp",EDGE,"E79"),sQuery(id+"F0.wireOp",EDGE,"E80"),sQuery(id+"F0.wireOp",EDGE,"E81"),sQuery(id+"F0.wireOp",EDGE,"E82"),sQuery(id+"F0.wireOp",EDGE,"E83"),sQuery(id+"F0.wireOp",EDGE,"E84"),sQuery(id+"F0.wireOp",EDGE,"E85"),sQuery(id+"F0.wireOp",EDGE,"E86"),sQuery(id+"F0.wireOp",EDGE,"E87"),sQuery(id+"F0.wireOp",EDGE,"E88"),sQuery(id+"F0.wireOp",EDGE,"E89"),sQuery(id+"F0.wireOp",EDGE,"E90"),sQuery(id+"F0.wireOp",EDGE,"E91"),sQuery(id+"F0.wireOp",EDGE,"E92"),sQuery(id+"F0.wireOp",EDGE,"E93"),sQuery(id+"F0.wireOp",EDGE,"E94"),sQuery(id+"F0.wireOp",EDGE,"E95"),sQuery(id+"F0.wireOp",EDGE,"E96"),sQuery(id+"F0.wireOp",EDGE,"E97"),sQuery(id+"F0.wireOp",EDGE,"E98"),sQuery(id+"F0.wireOp",EDGE,"E99"),sQuery(id+"F0.wireOp",EDGE,"E100"),sQuery(id+"F0.wireOp",EDGE,"E101"),sQuery(id+"F0.wireOp",EDGE,"E102"),sQuery(id+"F0.wireOp",EDGE,"E103"),sQuery(id+"F0.wireOp",EDGE,"E104")])]}),"instanceName":"37"});
            var Q5;
            Q5=makeQuery(id+"F2.opPattern","COPY",BODY,{"derivedFrom":makeQuery(id+"F1.opExtrude","SWEPT_BODY",BODY,{"disambiguationData":[OSD([sQuery(id+"F0.wireOp",EDGE,"E1"),sQuery(id+"F0.wireOp",EDGE,"E2"),sQuery(id+"F0.wireOp",EDGE,"E3"),sQuery(id+"F0.wireOp",EDGE,"E4"),sQuery(id+"F0.wireOp",EDGE,"E5"),sQuery(id+"F0.wireOp",EDGE,"E6"),sQuery(id+"F0.wireOp",EDGE,"E7"),sQuery(id+"F0.wireOp",EDGE,"E8"),sQuery(id+"F0.wireOp",EDGE,"E9"),sQuery(id+"F0.wireOp",EDGE,"E10"),sQuery(id+"F0.wireOp",EDGE,"E11"),sQuery(id+"F0.wireOp",EDGE,"E12"),sQuery(id+"F0.wireOp",EDGE,"E13"),sQuery(id+"F0.wireOp",EDGE,"E14"),sQuery(id+"F0.wireOp",EDGE,"E15"),sQuery(id+"F0.wireOp",EDGE,"E16"),sQuery(id+"F0.wireOp",EDGE,"E17"),sQuery(id+"F0.wireOp",EDGE,"E18"),sQuery(id+"F0.wireOp",EDGE,"E19"),sQuery(id+"F0.wireOp",EDGE,"E20"),sQuery(id+"F0.wireOp",EDGE,"E21"),sQuery(id+"F0.wireOp",EDGE,"E22"),sQuery(id+"F0.wireOp",EDGE,"E23"),sQuery(id+"F0.wireOp",EDGE,"E24"),sQuery(id+"F0.wireOp",EDGE,"E25"),sQuery(id+"F0.wireOp",EDGE,"E26"),sQuery(id+"F0.wireOp",EDGE,"E27"),sQuery(id+"F0.wireOp",EDGE,"E28"),sQuery(id+"F0.wireOp",EDGE,"E29"),sQuery(id+"F0.wireOp",EDGE,"E30"),sQuery(id+"F0.wireOp",EDGE,"E31"),sQuery(id+"F0.wireOp",EDGE,"E32"),sQuery(id+"F0.wireOp",EDGE,"E33"),sQuery(id+"F0.wireOp",EDGE,"E34"),sQuery(id+"F0.wireOp",EDGE,"E35"),sQuery(id+"F0.wireOp",EDGE,"E36"),sQuery(id+"F0.wireOp",EDGE,"E37"),sQuery(id+"F0.wireOp",EDGE,"E38"),sQuery(id+"F0.wireOp",EDGE,"E39"),sQuery(id+"F0.wireOp",EDGE,"E40"),sQuery(id+"F0.wireOp",EDGE,"E41"),sQuery(id+"F0.wireOp",EDGE,"E42"),sQuery(id+"F0.wireOp",EDGE,"E43"),sQuery(id+"F0.wireOp",EDGE,"E44"),sQuery(id+"F0.wireOp",EDGE,"E45"),sQuery(id+"F0.wireOp",EDGE,"E46"),sQuery(id+"F0.wireOp",EDGE,"E47"),sQuery(id+"F0.wireOp",EDGE,"E48"),sQuery(id+"F0.wireOp",EDGE,"E49"),sQuery(id+"F0.wireOp",EDGE,"E50"),sQuery(id+"F0.wireOp",EDGE,"E51"),sQuery(id+"F0.wireOp",EDGE,"E52"),sQuery(id+"F0.wireOp",EDGE,"E53"),sQuery(id+"F0.wireOp",EDGE,"E54"),sQuery(id+"F0.wireOp",EDGE,"E55"),sQuery(id+"F0.wireOp",EDGE,"E56"),sQuery(id+"F0.wireOp",EDGE,"E57"),sQuery(id+"F0.wireOp",EDGE,"E58"),sQuery(id+"F0.wireOp",EDGE,"E59"),sQuery(id+"F0.wireOp",EDGE,"E60"),sQuery(id+"F0.wireOp",EDGE,"E61"),sQuery(id+"F0.wireOp",EDGE,"E62"),sQuery(id+"F0.wireOp",EDGE,"E63"),sQuery(id+"F0.wireOp",EDGE,"E64"),sQuery(id+"F0.wireOp",EDGE,"E65"),sQuery(id+"F0.wireOp",EDGE,"E66"),sQuery(id+"F0.wireOp",EDGE,"E67"),sQuery(id+"F0.wireOp",EDGE,"E68"),sQuery(id+"F0.wireOp",EDGE,"E69"),sQuery(id+"F0.wireOp",EDGE,"E70"),sQuery(id+"F0.wireOp",EDGE,"E71"),sQuery(id+"F0.wireOp",EDGE,"E72"),sQuery(id+"F0.wireOp",EDGE,"E73"),sQuery(id+"F0.wireOp",EDGE,"E74"),sQuery(id+"F0.wireOp",EDGE,"E75"),sQuery(id+"F0.wireOp",EDGE,"E76"),sQuery(id+"F0.wireOp",EDGE,"E77"),sQuery(id+"F0.wireOp",EDGE,"E78"),sQuery(id+"F0.wireOp",EDGE,"E79"),sQuery(id+"F0.wireOp",EDGE,"E80"),sQuery(id+"F0.wireOp",EDGE,"E81"),sQuery(id+"F0.wireOp",EDGE,"E82"),sQuery(id+"F0.wireOp",EDGE,"E83"),sQuery(id+"F0.wireOp",EDGE,"E84"),sQuery(id+"F0.wireOp",EDGE,"E85"),sQuery(id+"F0.wireOp",EDGE,"E86"),sQuery(id+"F0.wireOp",EDGE,"E87"),sQuery(id+"F0.wireOp",EDGE,"E88"),sQuery(id+"F0.wireOp",EDGE,"E89"),sQuery(id+"F0.wireOp",EDGE,"E90"),sQuery(id+"F0.wireOp",EDGE,"E91"),sQuery(id+"F0.wireOp",EDGE,"E92"),sQuery(id+"F0.wireOp",EDGE,"E93"),sQuery(id+"F0.wireOp",EDGE,"E94"),sQuery(id+"F0.wireOp",EDGE,"E95"),sQuery(id+"F0.wireOp",EDGE,"E96"),sQuery(id+"F0.wireOp",EDGE,"E97"),sQuery(id+"F0.wireOp",EDGE,"E98"),sQuery(id+"F0.wireOp",EDGE,"E99"),sQuery(id+"F0.wireOp",EDGE,"E100"),sQuery(id+"F0.wireOp",EDGE,"E101"),sQuery(id+"F0.wireOp",EDGE,"E102"),sQuery(id+"F0.wireOp",EDGE,"E103"),sQuery(id+"F0.wireOp",EDGE,"E104")])]}),"instanceName":"38"});
            var Q6;
            Q6=makeQuery(id+"F2.opPattern","COPY",BODY,{"derivedFrom":makeQuery(id+"F1.opExtrude","SWEPT_BODY",BODY,{"disambiguationData":[OSD([sQuery(id+"F0.wireOp",EDGE,"E1"),sQuery(id+"F0.wireOp",EDGE,"E2"),sQuery(id+"F0.wireOp",EDGE,"E3"),sQuery(id+"F0.wireOp",EDGE,"E4"),sQuery(id+"F0.wireOp",EDGE,"E5"),sQuery(id+"F0.wireOp",EDGE,"E6"),sQuery(id+"F0.wireOp",EDGE,"E7"),sQuery(id+"F0.wireOp",EDGE,"E8"),sQuery(id+"F0.wireOp",EDGE,"E9"),sQuery(id+"F0.wireOp",EDGE,"E10"),sQuery(id+"F0.wireOp",EDGE,"E11"),sQuery(id+"F0.wireOp",EDGE,"E12"),sQuery(id+"F0.wireOp",EDGE,"E13"),sQuery(id+"F0.wireOp",EDGE,"E14"),sQuery(id+"F0.wireOp",EDGE,"E15"),sQuery(id+"F0.wireOp",EDGE,"E16"),sQuery(id+"F0.wireOp",EDGE,"E17"),sQuery(id+"F0.wireOp",EDGE,"E18"),sQuery(id+"F0.wireOp",EDGE,"E19"),sQuery(id+"F0.wireOp",EDGE,"E20"),sQuery(id+"F0.wireOp",EDGE,"E21"),sQuery(id+"F0.wireOp",EDGE,"E22"),sQuery(id+"F0.wireOp",EDGE,"E23"),sQuery(id+"F0.wireOp",EDGE,"E24"),sQuery(id+"F0.wireOp",EDGE,"E25"),sQuery(id+"F0.wireOp",EDGE,"E26"),sQuery(id+"F0.wireOp",EDGE,"E27"),sQuery(id+"F0.wireOp",EDGE,"E28"),sQuery(id+"F0.wireOp",EDGE,"E29"),sQuery(id+"F0.wireOp",EDGE,"E30"),sQuery(id+"F0.wireOp",EDGE,"E31"),sQuery(id+"F0.wireOp",EDGE,"E32"),sQuery(id+"F0.wireOp",EDGE,"E33"),sQuery(id+"F0.wireOp",EDGE,"E34"),sQuery(id+"F0.wireOp",EDGE,"E35"),sQuery(id+"F0.wireOp",EDGE,"E36"),sQuery(id+"F0.wireOp",EDGE,"E37"),sQuery(id+"F0.wireOp",EDGE,"E38"),sQuery(id+"F0.wireOp",EDGE,"E39"),sQuery(id+"F0.wireOp",EDGE,"E40"),sQuery(id+"F0.wireOp",EDGE,"E41"),sQuery(id+"F0.wireOp",EDGE,"E42"),sQuery(id+"F0.wireOp",EDGE,"E43"),sQuery(id+"F0.wireOp",EDGE,"E44"),sQuery(id+"F0.wireOp",EDGE,"E45"),sQuery(id+"F0.wireOp",EDGE,"E46"),sQuery(id+"F0.wireOp",EDGE,"E47"),sQuery(id+"F0.wireOp",EDGE,"E48"),sQuery(id+"F0.wireOp",EDGE,"E49"),sQuery(id+"F0.wireOp",EDGE,"E50"),sQuery(id+"F0.wireOp",EDGE,"E51"),sQuery(id+"F0.wireOp",EDGE,"E52"),sQuery(id+"F0.wireOp",EDGE,"E53"),sQuery(id+"F0.wireOp",EDGE,"E54"),sQuery(id+"F0.wireOp",EDGE,"E55"),sQuery(id+"F0.wireOp",EDGE,"E56"),sQuery(id+"F0.wireOp",EDGE,"E57"),sQuery(id+"F0.wireOp",EDGE,"E58"),sQuery(id+"F0.wireOp",EDGE,"E59"),sQuery(id+"F0.wireOp",EDGE,"E60"),sQuery(id+"F0.wireOp",EDGE,"E61"),sQuery(id+"F0.wireOp",EDGE,"E62"),sQuery(id+"F0.wireOp",EDGE,"E63"),sQuery(id+"F0.wireOp",EDGE,"E64"),sQuery(id+"F0.wireOp",EDGE,"E65"),sQuery(id+"F0.wireOp",EDGE,"E66"),sQuery(id+"F0.wireOp",EDGE,"E67"),sQuery(id+"F0.wireOp",EDGE,"E68"),sQuery(id+"F0.wireOp",EDGE,"E69"),sQuery(id+"F0.wireOp",EDGE,"E70"),sQuery(id+"F0.wireOp",EDGE,"E71"),sQuery(id+"F0.wireOp",EDGE,"E72"),sQuery(id+"F0.wireOp",EDGE,"E73"),sQuery(id+"F0.wireOp",EDGE,"E74"),sQuery(id+"F0.wireOp",EDGE,"E75"),sQuery(id+"F0.wireOp",EDGE,"E76"),sQuery(id+"F0.wireOp",EDGE,"E77"),sQuery(id+"F0.wireOp",EDGE,"E78"),sQuery(id+"F0.wireOp",EDGE,"E79"),sQuery(id+"F0.wireOp",EDGE,"E80"),sQuery(id+"F0.wireOp",EDGE,"E81"),sQuery(id+"F0.wireOp",EDGE,"E82"),sQuery(id+"F0.wireOp",EDGE,"E83"),sQuery(id+"F0.wireOp",EDGE,"E84"),sQuery(id+"F0.wireOp",EDGE,"E85"),sQuery(id+"F0.wireOp",EDGE,"E86"),sQuery(id+"F0.wireOp",EDGE,"E87"),sQuery(id+"F0.wireOp",EDGE,"E88"),sQuery(id+"F0.wireOp",EDGE,"E89"),sQuery(id+"F0.wireOp",EDGE,"E90"),sQuery(id+"F0.wireOp",EDGE,"E91"),sQuery(id+"F0.wireOp",EDGE,"E92"),sQuery(id+"F0.wireOp",EDGE,"E93"),sQuery(id+"F0.wireOp",EDGE,"E94"),sQuery(id+"F0.wireOp",EDGE,"E95"),sQuery(id+"F0.wireOp",EDGE,"E96"),sQuery(id+"F0.wireOp",EDGE,"E97"),sQuery(id+"F0.wireOp",EDGE,"E98"),sQuery(id+"F0.wireOp",EDGE,"E99"),sQuery(id+"F0.wireOp",EDGE,"E100"),sQuery(id+"F0.wireOp",EDGE,"E101"),sQuery(id+"F0.wireOp",EDGE,"E102"),sQuery(id+"F0.wireOp",EDGE,"E103"),sQuery(id+"F0.wireOp",EDGE,"E104")])]}),"instanceName":"39"});
            var Q7;
            Q7=makeQuery(id+"F2.opPattern","COPY",BODY,{"derivedFrom":makeQuery(id+"F1.opExtrude","SWEPT_BODY",BODY,{"disambiguationData":[OSD([sQuery(id+"F0.wireOp",EDGE,"E1"),sQuery(id+"F0.wireOp",EDGE,"E2"),sQuery(id+"F0.wireOp",EDGE,"E3"),sQuery(id+"F0.wireOp",EDGE,"E4"),sQuery(id+"F0.wireOp",EDGE,"E5"),sQuery(id+"F0.wireOp",EDGE,"E6"),sQuery(id+"F0.wireOp",EDGE,"E7"),sQuery(id+"F0.wireOp",EDGE,"E8"),sQuery(id+"F0.wireOp",EDGE,"E9"),sQuery(id+"F0.wireOp",EDGE,"E10"),sQuery(id+"F0.wireOp",EDGE,"E11"),sQuery(id+"F0.wireOp",EDGE,"E12"),sQuery(id+"F0.wireOp",EDGE,"E13"),sQuery(id+"F0.wireOp",EDGE,"E14"),sQuery(id+"F0.wireOp",EDGE,"E15"),sQuery(id+"F0.wireOp",EDGE,"E16"),sQuery(id+"F0.wireOp",EDGE,"E17"),sQuery(id+"F0.wireOp",EDGE,"E18"),sQuery(id+"F0.wireOp",EDGE,"E19"),sQuery(id+"F0.wireOp",EDGE,"E20"),sQuery(id+"F0.wireOp",EDGE,"E21"),sQuery(id+"F0.wireOp",EDGE,"E22"),sQuery(id+"F0.wireOp",EDGE,"E23"),sQuery(id+"F0.wireOp",EDGE,"E24"),sQuery(id+"F0.wireOp",EDGE,"E25"),sQuery(id+"F0.wireOp",EDGE,"E26"),sQuery(id+"F0.wireOp",EDGE,"E27"),sQuery(id+"F0.wireOp",EDGE,"E28"),sQuery(id+"F0.wireOp",EDGE,"E29"),sQuery(id+"F0.wireOp",EDGE,"E30"),sQuery(id+"F0.wireOp",EDGE,"E31"),sQuery(id+"F0.wireOp",EDGE,"E32"),sQuery(id+"F0.wireOp",EDGE,"E33"),sQuery(id+"F0.wireOp",EDGE,"E34"),sQuery(id+"F0.wireOp",EDGE,"E35"),sQuery(id+"F0.wireOp",EDGE,"E36"),sQuery(id+"F0.wireOp",EDGE,"E37"),sQuery(id+"F0.wireOp",EDGE,"E38"),sQuery(id+"F0.wireOp",EDGE,"E39"),sQuery(id+"F0.wireOp",EDGE,"E40"),sQuery(id+"F0.wireOp",EDGE,"E41"),sQuery(id+"F0.wireOp",EDGE,"E42"),sQuery(id+"F0.wireOp",EDGE,"E43"),sQuery(id+"F0.wireOp",EDGE,"E44"),sQuery(id+"F0.wireOp",EDGE,"E45"),sQuery(id+"F0.wireOp",EDGE,"E46"),sQuery(id+"F0.wireOp",EDGE,"E47"),sQuery(id+"F0.wireOp",EDGE,"E48"),sQuery(id+"F0.wireOp",EDGE,"E49"),sQuery(id+"F0.wireOp",EDGE,"E50"),sQuery(id+"F0.wireOp",EDGE,"E51"),sQuery(id+"F0.wireOp",EDGE,"E52"),sQuery(id+"F0.wireOp",EDGE,"E53"),sQuery(id+"F0.wireOp",EDGE,"E54"),sQuery(id+"F0.wireOp",EDGE,"E55"),sQuery(id+"F0.wireOp",EDGE,"E56"),sQuery(id+"F0.wireOp",EDGE,"E57"),sQuery(id+"F0.wireOp",EDGE,"E58"),sQuery(id+"F0.wireOp",EDGE,"E59"),sQuery(id+"F0.wireOp",EDGE,"E60"),sQuery(id+"F0.wireOp",EDGE,"E61"),sQuery(id+"F0.wireOp",EDGE,"E62"),sQuery(id+"F0.wireOp",EDGE,"E63"),sQuery(id+"F0.wireOp",EDGE,"E64"),sQuery(id+"F0.wireOp",EDGE,"E65"),sQuery(id+"F0.wireOp",EDGE,"E66"),sQuery(id+"F0.wireOp",EDGE,"E67"),sQuery(id+"F0.wireOp",EDGE,"E68"),sQuery(id+"F0.wireOp",EDGE,"E69"),sQuery(id+"F0.wireOp",EDGE,"E70"),sQuery(id+"F0.wireOp",EDGE,"E71"),sQuery(id+"F0.wireOp",EDGE,"E72"),sQuery(id+"F0.wireOp",EDGE,"E73"),sQuery(id+"F0.wireOp",EDGE,"E74"),sQuery(id+"F0.wireOp",EDGE,"E75"),sQuery(id+"F0.wireOp",EDGE,"E76"),sQuery(id+"F0.wireOp",EDGE,"E77"),sQuery(id+"F0.wireOp",EDGE,"E78"),sQuery(id+"F0.wireOp",EDGE,"E79"),sQuery(id+"F0.wireOp",EDGE,"E80"),sQuery(id+"F0.wireOp",EDGE,"E81"),sQuery(id+"F0.wireOp",EDGE,"E82"),sQuery(id+"F0.wireOp",EDGE,"E83"),sQuery(id+"F0.wireOp",EDGE,"E84"),sQuery(id+"F0.wireOp",EDGE,"E85"),sQuery(id+"F0.wireOp",EDGE,"E86"),sQuery(id+"F0.wireOp",EDGE,"E87"),sQuery(id+"F0.wireOp",EDGE,"E88"),sQuery(id+"F0.wireOp",EDGE,"E89"),sQuery(id+"F0.wireOp",EDGE,"E90"),sQuery(id+"F0.wireOp",EDGE,"E91"),sQuery(id+"F0.wireOp",EDGE,"E92"),sQuery(id+"F0.wireOp",EDGE,"E93"),sQuery(id+"F0.wireOp",EDGE,"E94"),sQuery(id+"F0.wireOp",EDGE,"E95"),sQuery(id+"F0.wireOp",EDGE,"E96"),sQuery(id+"F0.wireOp",EDGE,"E97"),sQuery(id+"F0.wireOp",EDGE,"E98"),sQuery(id+"F0.wireOp",EDGE,"E99"),sQuery(id+"F0.wireOp",EDGE,"E100"),sQuery(id+"F0.wireOp",EDGE,"E101"),sQuery(id+"F0.wireOp",EDGE,"E102"),sQuery(id+"F0.wireOp",EDGE,"E103"),sQuery(id+"F0.wireOp",EDGE,"E104")])]}),"instanceName":"40"});
            var Q8;
            Q8=makeQuery(id+"F2.opPattern","COPY",BODY,{"derivedFrom":makeQuery(id+"F1.opExtrude","SWEPT_BODY",BODY,{"disambiguationData":[OSD([sQuery(id+"F0.wireOp",EDGE,"E1"),sQuery(id+"F0.wireOp",EDGE,"E2"),sQuery(id+"F0.wireOp",EDGE,"E3"),sQuery(id+"F0.wireOp",EDGE,"E4"),sQuery(id+"F0.wireOp",EDGE,"E5"),sQuery(id+"F0.wireOp",EDGE,"E6"),sQuery(id+"F0.wireOp",EDGE,"E7"),sQuery(id+"F0.wireOp",EDGE,"E8"),sQuery(id+"F0.wireOp",EDGE,"E9"),sQuery(id+"F0.wireOp",EDGE,"E10"),sQuery(id+"F0.wireOp",EDGE,"E11"),sQuery(id+"F0.wireOp",EDGE,"E12"),sQuery(id+"F0.wireOp",EDGE,"E13"),sQuery(id+"F0.wireOp",EDGE,"E14"),sQuery(id+"F0.wireOp",EDGE,"E15"),sQuery(id+"F0.wireOp",EDGE,"E16"),sQuery(id+"F0.wireOp",EDGE,"E17"),sQuery(id+"F0.wireOp",EDGE,"E18"),sQuery(id+"F0.wireOp",EDGE,"E19"),sQuery(id+"F0.wireOp",EDGE,"E20"),sQuery(id+"F0.wireOp",EDGE,"E21"),sQuery(id+"F0.wireOp",EDGE,"E22"),sQuery(id+"F0.wireOp",EDGE,"E23"),sQuery(id+"F0.wireOp",EDGE,"E24"),sQuery(id+"F0.wireOp",EDGE,"E25"),sQuery(id+"F0.wireOp",EDGE,"E26"),sQuery(id+"F0.wireOp",EDGE,"E27"),sQuery(id+"F0.wireOp",EDGE,"E28"),sQuery(id+"F0.wireOp",EDGE,"E29"),sQuery(id+"F0.wireOp",EDGE,"E30"),sQuery(id+"F0.wireOp",EDGE,"E31"),sQuery(id+"F0.wireOp",EDGE,"E32"),sQuery(id+"F0.wireOp",EDGE,"E33"),sQuery(id+"F0.wireOp",EDGE,"E34"),sQuery(id+"F0.wireOp",EDGE,"E35"),sQuery(id+"F0.wireOp",EDGE,"E36"),sQuery(id+"F0.wireOp",EDGE,"E37"),sQuery(id+"F0.wireOp",EDGE,"E38"),sQuery(id+"F0.wireOp",EDGE,"E39"),sQuery(id+"F0.wireOp",EDGE,"E40"),sQuery(id+"F0.wireOp",EDGE,"E41"),sQuery(id+"F0.wireOp",EDGE,"E42"),sQuery(id+"F0.wireOp",EDGE,"E43"),sQuery(id+"F0.wireOp",EDGE,"E44"),sQuery(id+"F0.wireOp",EDGE,"E45"),sQuery(id+"F0.wireOp",EDGE,"E46"),sQuery(id+"F0.wireOp",EDGE,"E47"),sQuery(id+"F0.wireOp",EDGE,"E48"),sQuery(id+"F0.wireOp",EDGE,"E49"),sQuery(id+"F0.wireOp",EDGE,"E50"),sQuery(id+"F0.wireOp",EDGE,"E51"),sQuery(id+"F0.wireOp",EDGE,"E52"),sQuery(id+"F0.wireOp",EDGE,"E53"),sQuery(id+"F0.wireOp",EDGE,"E54"),sQuery(id+"F0.wireOp",EDGE,"E55"),sQuery(id+"F0.wireOp",EDGE,"E56"),sQuery(id+"F0.wireOp",EDGE,"E57"),sQuery(id+"F0.wireOp",EDGE,"E58"),sQuery(id+"F0.wireOp",EDGE,"E59"),sQuery(id+"F0.wireOp",EDGE,"E60"),sQuery(id+"F0.wireOp",EDGE,"E61"),sQuery(id+"F0.wireOp",EDGE,"E62"),sQuery(id+"F0.wireOp",EDGE,"E63"),sQuery(id+"F0.wireOp",EDGE,"E64"),sQuery(id+"F0.wireOp",EDGE,"E65"),sQuery(id+"F0.wireOp",EDGE,"E66"),sQuery(id+"F0.wireOp",EDGE,"E67"),sQuery(id+"F0.wireOp",EDGE,"E68"),sQuery(id+"F0.wireOp",EDGE,"E69"),sQuery(id+"F0.wireOp",EDGE,"E70"),sQuery(id+"F0.wireOp",EDGE,"E71"),sQuery(id+"F0.wireOp",EDGE,"E72"),sQuery(id+"F0.wireOp",EDGE,"E73"),sQuery(id+"F0.wireOp",EDGE,"E74"),sQuery(id+"F0.wireOp",EDGE,"E75"),sQuery(id+"F0.wireOp",EDGE,"E76"),sQuery(id+"F0.wireOp",EDGE,"E77"),sQuery(id+"F0.wireOp",EDGE,"E78"),sQuery(id+"F0.wireOp",EDGE,"E79"),sQuery(id+"F0.wireOp",EDGE,"E80"),sQuery(id+"F0.wireOp",EDGE,"E81"),sQuery(id+"F0.wireOp",EDGE,"E82"),sQuery(id+"F0.wireOp",EDGE,"E83"),sQuery(id+"F0.wireOp",EDGE,"E84"),sQuery(id+"F0.wireOp",EDGE,"E85"),sQuery(id+"F0.wireOp",EDGE,"E86"),sQuery(id+"F0.wireOp",EDGE,"E87"),sQuery(id+"F0.wireOp",EDGE,"E88"),sQuery(id+"F0.wireOp",EDGE,"E89"),sQuery(id+"F0.wireOp",EDGE,"E90"),sQuery(id+"F0.wireOp",EDGE,"E91"),sQuery(id+"F0.wireOp",EDGE,"E92"),sQuery(id+"F0.wireOp",EDGE,"E93"),sQuery(id+"F0.wireOp",EDGE,"E94"),sQuery(id+"F0.wireOp",EDGE,"E95"),sQuery(id+"F0.wireOp",EDGE,"E96"),sQuery(id+"F0.wireOp",EDGE,"E97"),sQuery(id+"F0.wireOp",EDGE,"E98"),sQuery(id+"F0.wireOp",EDGE,"E99"),sQuery(id+"F0.wireOp",EDGE,"E100"),sQuery(id+"F0.wireOp",EDGE,"E101"),sQuery(id+"F0.wireOp",EDGE,"E102"),sQuery(id+"F0.wireOp",EDGE,"E103"),sQuery(id+"F0.wireOp",EDGE,"E104")])]}),"instanceName":"41"});
            var Q9;
            Q9=makeQuery(id+"F2.opPattern","COPY",BODY,{"derivedFrom":makeQuery(id+"F1.opExtrude","SWEPT_BODY",BODY,{"disambiguationData":[OSD([sQuery(id+"F0.wireOp",EDGE,"E1"),sQuery(id+"F0.wireOp",EDGE,"E2"),sQuery(id+"F0.wireOp",EDGE,"E3"),sQuery(id+"F0.wireOp",EDGE,"E4"),sQuery(id+"F0.wireOp",EDGE,"E5"),sQuery(id+"F0.wireOp",EDGE,"E6"),sQuery(id+"F0.wireOp",EDGE,"E7"),sQuery(id+"F0.wireOp",EDGE,"E8"),sQuery(id+"F0.wireOp",EDGE,"E9"),sQuery(id+"F0.wireOp",EDGE,"E10"),sQuery(id+"F0.wireOp",EDGE,"E11"),sQuery(id+"F0.wireOp",EDGE,"E12"),sQuery(id+"F0.wireOp",EDGE,"E13"),sQuery(id+"F0.wireOp",EDGE,"E14"),sQuery(id+"F0.wireOp",EDGE,"E15"),sQuery(id+"F0.wireOp",EDGE,"E16"),sQuery(id+"F0.wireOp",EDGE,"E17"),sQuery(id+"F0.wireOp",EDGE,"E18"),sQuery(id+"F0.wireOp",EDGE,"E19"),sQuery(id+"F0.wireOp",EDGE,"E20"),sQuery(id+"F0.wireOp",EDGE,"E21"),sQuery(id+"F0.wireOp",EDGE,"E22"),sQuery(id+"F0.wireOp",EDGE,"E23"),sQuery(id+"F0.wireOp",EDGE,"E24"),sQuery(id+"F0.wireOp",EDGE,"E25"),sQuery(id+"F0.wireOp",EDGE,"E26"),sQuery(id+"F0.wireOp",EDGE,"E27"),sQuery(id+"F0.wireOp",EDGE,"E28"),sQuery(id+"F0.wireOp",EDGE,"E29"),sQuery(id+"F0.wireOp",EDGE,"E30"),sQuery(id+"F0.wireOp",EDGE,"E31"),sQuery(id+"F0.wireOp",EDGE,"E32"),sQuery(id+"F0.wireOp",EDGE,"E33"),sQuery(id+"F0.wireOp",EDGE,"E34"),sQuery(id+"F0.wireOp",EDGE,"E35"),sQuery(id+"F0.wireOp",EDGE,"E36"),sQuery(id+"F0.wireOp",EDGE,"E37"),sQuery(id+"F0.wireOp",EDGE,"E38"),sQuery(id+"F0.wireOp",EDGE,"E39"),sQuery(id+"F0.wireOp",EDGE,"E40"),sQuery(id+"F0.wireOp",EDGE,"E41"),sQuery(id+"F0.wireOp",EDGE,"E42"),sQuery(id+"F0.wireOp",EDGE,"E43"),sQuery(id+"F0.wireOp",EDGE,"E44"),sQuery(id+"F0.wireOp",EDGE,"E45"),sQuery(id+"F0.wireOp",EDGE,"E46"),sQuery(id+"F0.wireOp",EDGE,"E47"),sQuery(id+"F0.wireOp",EDGE,"E48"),sQuery(id+"F0.wireOp",EDGE,"E49"),sQuery(id+"F0.wireOp",EDGE,"E50"),sQuery(id+"F0.wireOp",EDGE,"E51"),sQuery(id+"F0.wireOp",EDGE,"E52"),sQuery(id+"F0.wireOp",EDGE,"E53"),sQuery(id+"F0.wireOp",EDGE,"E54"),sQuery(id+"F0.wireOp",EDGE,"E55"),sQuery(id+"F0.wireOp",EDGE,"E56"),sQuery(id+"F0.wireOp",EDGE,"E57"),sQuery(id+"F0.wireOp",EDGE,"E58"),sQuery(id+"F0.wireOp",EDGE,"E59"),sQuery(id+"F0.wireOp",EDGE,"E60"),sQuery(id+"F0.wireOp",EDGE,"E61"),sQuery(id+"F0.wireOp",EDGE,"E62"),sQuery(id+"F0.wireOp",EDGE,"E63"),sQuery(id+"F0.wireOp",EDGE,"E64"),sQuery(id+"F0.wireOp",EDGE,"E65"),sQuery(id+"F0.wireOp",EDGE,"E66"),sQuery(id+"F0.wireOp",EDGE,"E67"),sQuery(id+"F0.wireOp",EDGE,"E68"),sQuery(id+"F0.wireOp",EDGE,"E69"),sQuery(id+"F0.wireOp",EDGE,"E70"),sQuery(id+"F0.wireOp",EDGE,"E71"),sQuery(id+"F0.wireOp",EDGE,"E72"),sQuery(id+"F0.wireOp",EDGE,"E73"),sQuery(id+"F0.wireOp",EDGE,"E74"),sQuery(id+"F0.wireOp",EDGE,"E75"),sQuery(id+"F0.wireOp",EDGE,"E76"),sQuery(id+"F0.wireOp",EDGE,"E77"),sQuery(id+"F0.wireOp",EDGE,"E78"),sQuery(id+"F0.wireOp",EDGE,"E79"),sQuery(id+"F0.wireOp",EDGE,"E80"),sQuery(id+"F0.wireOp",EDGE,"E81"),sQuery(id+"F0.wireOp",EDGE,"E82"),sQuery(id+"F0.wireOp",EDGE,"E83"),sQuery(id+"F0.wireOp",EDGE,"E84"),sQuery(id+"F0.wireOp",EDGE,"E85"),sQuery(id+"F0.wireOp",EDGE,"E86"),sQuery(id+"F0.wireOp",EDGE,"E87"),sQuery(id+"F0.wireOp",EDGE,"E88"),sQuery(id+"F0.wireOp",EDGE,"E89"),sQuery(id+"F0.wireOp",EDGE,"E90"),sQuery(id+"F0.wireOp",EDGE,"E91"),sQuery(id+"F0.wireOp",EDGE,"E92"),sQuery(id+"F0.wireOp",EDGE,"E93"),sQuery(id+"F0.wireOp",EDGE,"E94"),sQuery(id+"F0.wireOp",EDGE,"E95"),sQuery(id+"F0.wireOp",EDGE,"E96"),sQuery(id+"F0.wireOp",EDGE,"E97"),sQuery(id+"F0.wireOp",EDGE,"E98"),sQuery(id+"F0.wireOp",EDGE,"E99"),sQuery(id+"F0.wireOp",EDGE,"E100"),sQuery(id+"F0.wireOp",EDGE,"E101"),sQuery(id+"F0.wireOp",EDGE,"E102"),sQuery(id+"F0.wireOp",EDGE,"E103"),sQuery(id+"F0.wireOp",EDGE,"E104")])]}),"instanceName":"42"});
            var Q10;
            Q10=makeQuery(id+"F2.opPattern","COPY",BODY,{"derivedFrom":makeQuery(id+"F1.opExtrude","SWEPT_BODY",BODY,{"disambiguationData":[OSD([sQuery(id+"F0.wireOp",EDGE,"E1"),sQuery(id+"F0.wireOp",EDGE,"E2"),sQuery(id+"F0.wireOp",EDGE,"E3"),sQuery(id+"F0.wireOp",EDGE,"E4"),sQuery(id+"F0.wireOp",EDGE,"E5"),sQuery(id+"F0.wireOp",EDGE,"E6"),sQuery(id+"F0.wireOp",EDGE,"E7"),sQuery(id+"F0.wireOp",EDGE,"E8"),sQuery(id+"F0.wireOp",EDGE,"E9"),sQuery(id+"F0.wireOp",EDGE,"E10"),sQuery(id+"F0.wireOp",EDGE,"E11"),sQuery(id+"F0.wireOp",EDGE,"E12"),sQuery(id+"F0.wireOp",EDGE,"E13"),sQuery(id+"F0.wireOp",EDGE,"E14"),sQuery(id+"F0.wireOp",EDGE,"E15"),sQuery(id+"F0.wireOp",EDGE,"E16"),sQuery(id+"F0.wireOp",EDGE,"E17"),sQuery(id+"F0.wireOp",EDGE,"E18"),sQuery(id+"F0.wireOp",EDGE,"E19"),sQuery(id+"F0.wireOp",EDGE,"E20"),sQuery(id+"F0.wireOp",EDGE,"E21"),sQuery(id+"F0.wireOp",EDGE,"E22"),sQuery(id+"F0.wireOp",EDGE,"E23"),sQuery(id+"F0.wireOp",EDGE,"E24"),sQuery(id+"F0.wireOp",EDGE,"E25"),sQuery(id+"F0.wireOp",EDGE,"E26"),sQuery(id+"F0.wireOp",EDGE,"E27"),sQuery(id+"F0.wireOp",EDGE,"E28"),sQuery(id+"F0.wireOp",EDGE,"E29"),sQuery(id+"F0.wireOp",EDGE,"E30"),sQuery(id+"F0.wireOp",EDGE,"E31"),sQuery(id+"F0.wireOp",EDGE,"E32"),sQuery(id+"F0.wireOp",EDGE,"E33"),sQuery(id+"F0.wireOp",EDGE,"E34"),sQuery(id+"F0.wireOp",EDGE,"E35"),sQuery(id+"F0.wireOp",EDGE,"E36"),sQuery(id+"F0.wireOp",EDGE,"E37"),sQuery(id+"F0.wireOp",EDGE,"E38"),sQuery(id+"F0.wireOp",EDGE,"E39"),sQuery(id+"F0.wireOp",EDGE,"E40"),sQuery(id+"F0.wireOp",EDGE,"E41"),sQuery(id+"F0.wireOp",EDGE,"E42"),sQuery(id+"F0.wireOp",EDGE,"E43"),sQuery(id+"F0.wireOp",EDGE,"E44"),sQuery(id+"F0.wireOp",EDGE,"E45"),sQuery(id+"F0.wireOp",EDGE,"E46"),sQuery(id+"F0.wireOp",EDGE,"E47"),sQuery(id+"F0.wireOp",EDGE,"E48"),sQuery(id+"F0.wireOp",EDGE,"E49"),sQuery(id+"F0.wireOp",EDGE,"E50"),sQuery(id+"F0.wireOp",EDGE,"E51"),sQuery(id+"F0.wireOp",EDGE,"E52"),sQuery(id+"F0.wireOp",EDGE,"E53"),sQuery(id+"F0.wireOp",EDGE,"E54"),sQuery(id+"F0.wireOp",EDGE,"E55"),sQuery(id+"F0.wireOp",EDGE,"E56"),sQuery(id+"F0.wireOp",EDGE,"E57"),sQuery(id+"F0.wireOp",EDGE,"E58"),sQuery(id+"F0.wireOp",EDGE,"E59"),sQuery(id+"F0.wireOp",EDGE,"E60"),sQuery(id+"F0.wireOp",EDGE,"E61"),sQuery(id+"F0.wireOp",EDGE,"E62"),sQuery(id+"F0.wireOp",EDGE,"E63"),sQuery(id+"F0.wireOp",EDGE,"E64"),sQuery(id+"F0.wireOp",EDGE,"E65"),sQuery(id+"F0.wireOp",EDGE,"E66"),sQuery(id+"F0.wireOp",EDGE,"E67"),sQuery(id+"F0.wireOp",EDGE,"E68"),sQuery(id+"F0.wireOp",EDGE,"E69"),sQuery(id+"F0.wireOp",EDGE,"E70"),sQuery(id+"F0.wireOp",EDGE,"E71"),sQuery(id+"F0.wireOp",EDGE,"E72"),sQuery(id+"F0.wireOp",EDGE,"E73"),sQuery(id+"F0.wireOp",EDGE,"E74"),sQuery(id+"F0.wireOp",EDGE,"E75"),sQuery(id+"F0.wireOp",EDGE,"E76"),sQuery(id+"F0.wireOp",EDGE,"E77"),sQuery(id+"F0.wireOp",EDGE,"E78"),sQuery(id+"F0.wireOp",EDGE,"E79"),sQuery(id+"F0.wireOp",EDGE,"E80"),sQuery(id+"F0.wireOp",EDGE,"E81"),sQuery(id+"F0.wireOp",EDGE,"E82"),sQuery(id+"F0.wireOp",EDGE,"E83"),sQuery(id+"F0.wireOp",EDGE,"E84"),sQuery(id+"F0.wireOp",EDGE,"E85"),sQuery(id+"F0.wireOp",EDGE,"E86"),sQuery(id+"F0.wireOp",EDGE,"E87"),sQuery(id+"F0.wireOp",EDGE,"E88"),sQuery(id+"F0.wireOp",EDGE,"E89"),sQuery(id+"F0.wireOp",EDGE,"E90"),sQuery(id+"F0.wireOp",EDGE,"E91"),sQuery(id+"F0.wireOp",EDGE,"E92"),sQuery(id+"F0.wireOp",EDGE,"E93"),sQuery(id+"F0.wireOp",EDGE,"E94"),sQuery(id+"F0.wireOp",EDGE,"E95"),sQuery(id+"F0.wireOp",EDGE,"E96"),sQuery(id+"F0.wireOp",EDGE,"E97"),sQuery(id+"F0.wireOp",EDGE,"E98"),sQuery(id+"F0.wireOp",EDGE,"E99"),sQuery(id+"F0.wireOp",EDGE,"E100"),sQuery(id+"F0.wireOp",EDGE,"E101"),sQuery(id+"F0.wireOp",EDGE,"E102"),sQuery(id+"F0.wireOp",EDGE,"E103"),sQuery(id+"F0.wireOp",EDGE,"E104")])]}),"instanceName":"43"});
            var Q11;
            Q11=makeQuery(id+"F2.opPattern","COPY",BODY,{"derivedFrom":makeQuery(id+"F1.opExtrude","SWEPT_BODY",BODY,{"disambiguationData":[OSD([sQuery(id+"F0.wireOp",EDGE,"E1"),sQuery(id+"F0.wireOp",EDGE,"E2"),sQuery(id+"F0.wireOp",EDGE,"E3"),sQuery(id+"F0.wireOp",EDGE,"E4"),sQuery(id+"F0.wireOp",EDGE,"E5"),sQuery(id+"F0.wireOp",EDGE,"E6"),sQuery(id+"F0.wireOp",EDGE,"E7"),sQuery(id+"F0.wireOp",EDGE,"E8"),sQuery(id+"F0.wireOp",EDGE,"E9"),sQuery(id+"F0.wireOp",EDGE,"E10"),sQuery(id+"F0.wireOp",EDGE,"E11"),sQuery(id+"F0.wireOp",EDGE,"E12"),sQuery(id+"F0.wireOp",EDGE,"E13"),sQuery(id+"F0.wireOp",EDGE,"E14"),sQuery(id+"F0.wireOp",EDGE,"E15"),sQuery(id+"F0.wireOp",EDGE,"E16"),sQuery(id+"F0.wireOp",EDGE,"E17"),sQuery(id+"F0.wireOp",EDGE,"E18"),sQuery(id+"F0.wireOp",EDGE,"E19"),sQuery(id+"F0.wireOp",EDGE,"E20"),sQuery(id+"F0.wireOp",EDGE,"E21"),sQuery(id+"F0.wireOp",EDGE,"E22"),sQuery(id+"F0.wireOp",EDGE,"E23"),sQuery(id+"F0.wireOp",EDGE,"E24"),sQuery(id+"F0.wireOp",EDGE,"E25"),sQuery(id+"F0.wireOp",EDGE,"E26"),sQuery(id+"F0.wireOp",EDGE,"E27"),sQuery(id+"F0.wireOp",EDGE,"E28"),sQuery(id+"F0.wireOp",EDGE,"E29"),sQuery(id+"F0.wireOp",EDGE,"E30"),sQuery(id+"F0.wireOp",EDGE,"E31"),sQuery(id+"F0.wireOp",EDGE,"E32"),sQuery(id+"F0.wireOp",EDGE,"E33"),sQuery(id+"F0.wireOp",EDGE,"E34"),sQuery(id+"F0.wireOp",EDGE,"E35"),sQuery(id+"F0.wireOp",EDGE,"E36"),sQuery(id+"F0.wireOp",EDGE,"E37"),sQuery(id+"F0.wireOp",EDGE,"E38"),sQuery(id+"F0.wireOp",EDGE,"E39"),sQuery(id+"F0.wireOp",EDGE,"E40"),sQuery(id+"F0.wireOp",EDGE,"E41"),sQuery(id+"F0.wireOp",EDGE,"E42"),sQuery(id+"F0.wireOp",EDGE,"E43"),sQuery(id+"F0.wireOp",EDGE,"E44"),sQuery(id+"F0.wireOp",EDGE,"E45"),sQuery(id+"F0.wireOp",EDGE,"E46"),sQuery(id+"F0.wireOp",EDGE,"E47"),sQuery(id+"F0.wireOp",EDGE,"E48"),sQuery(id+"F0.wireOp",EDGE,"E49"),sQuery(id+"F0.wireOp",EDGE,"E50"),sQuery(id+"F0.wireOp",EDGE,"E51"),sQuery(id+"F0.wireOp",EDGE,"E52"),sQuery(id+"F0.wireOp",EDGE,"E53"),sQuery(id+"F0.wireOp",EDGE,"E54"),sQuery(id+"F0.wireOp",EDGE,"E55"),sQuery(id+"F0.wireOp",EDGE,"E56"),sQuery(id+"F0.wireOp",EDGE,"E57"),sQuery(id+"F0.wireOp",EDGE,"E58"),sQuery(id+"F0.wireOp",EDGE,"E59"),sQuery(id+"F0.wireOp",EDGE,"E60"),sQuery(id+"F0.wireOp",EDGE,"E61"),sQuery(id+"F0.wireOp",EDGE,"E62"),sQuery(id+"F0.wireOp",EDGE,"E63"),sQuery(id+"F0.wireOp",EDGE,"E64"),sQuery(id+"F0.wireOp",EDGE,"E65"),sQuery(id+"F0.wireOp",EDGE,"E66"),sQuery(id+"F0.wireOp",EDGE,"E67"),sQuery(id+"F0.wireOp",EDGE,"E68"),sQuery(id+"F0.wireOp",EDGE,"E69"),sQuery(id+"F0.wireOp",EDGE,"E70"),sQuery(id+"F0.wireOp",EDGE,"E71"),sQuery(id+"F0.wireOp",EDGE,"E72"),sQuery(id+"F0.wireOp",EDGE,"E73"),sQuery(id+"F0.wireOp",EDGE,"E74"),sQuery(id+"F0.wireOp",EDGE,"E75"),sQuery(id+"F0.wireOp",EDGE,"E76"),sQuery(id+"F0.wireOp",EDGE,"E77"),sQuery(id+"F0.wireOp",EDGE,"E78"),sQuery(id+"F0.wireOp",EDGE,"E79"),sQuery(id+"F0.wireOp",EDGE,"E80"),sQuery(id+"F0.wireOp",EDGE,"E81"),sQuery(id+"F0.wireOp",EDGE,"E82"),sQuery(id+"F0.wireOp",EDGE,"E83"),sQuery(id+"F0.wireOp",EDGE,"E84"),sQuery(id+"F0.wireOp",EDGE,"E85"),sQuery(id+"F0.wireOp",EDGE,"E86"),sQuery(id+"F0.wireOp",EDGE,"E87"),sQuery(id+"F0.wireOp",EDGE,"E88"),sQuery(id+"F0.wireOp",EDGE,"E89"),sQuery(id+"F0.wireOp",EDGE,"E90"),sQuery(id+"F0.wireOp",EDGE,"E91"),sQuery(id+"F0.wireOp",EDGE,"E92"),sQuery(id+"F0.wireOp",EDGE,"E93"),sQuery(id+"F0.wireOp",EDGE,"E94"),sQuery(id+"F0.wireOp",EDGE,"E95"),sQuery(id+"F0.wireOp",EDGE,"E96"),sQuery(id+"F0.wireOp",EDGE,"E97"),sQuery(id+"F0.wireOp",EDGE,"E98"),sQuery(id+"F0.wireOp",EDGE,"E99"),sQuery(id+"F0.wireOp",EDGE,"E100"),sQuery(id+"F0.wireOp",EDGE,"E101"),sQuery(id+"F0.wireOp",EDGE,"E102"),sQuery(id+"F0.wireOp",EDGE,"E103"),sQuery(id+"F0.wireOp",EDGE,"E104")])]}),"instanceName":"44"});
            var Q12;
            Q12=makeQuery(id+"F2.opPattern","COPY",BODY,{"derivedFrom":makeQuery(id+"F1.opExtrude","SWEPT_BODY",BODY,{"disambiguationData":[OSD([sQuery(id+"F0.wireOp",EDGE,"E1"),sQuery(id+"F0.wireOp",EDGE,"E2"),sQuery(id+"F0.wireOp",EDGE,"E3"),sQuery(id+"F0.wireOp",EDGE,"E4"),sQuery(id+"F0.wireOp",EDGE,"E5"),sQuery(id+"F0.wireOp",EDGE,"E6"),sQuery(id+"F0.wireOp",EDGE,"E7"),sQuery(id+"F0.wireOp",EDGE,"E8"),sQuery(id+"F0.wireOp",EDGE,"E9"),sQuery(id+"F0.wireOp",EDGE,"E10"),sQuery(id+"F0.wireOp",EDGE,"E11"),sQuery(id+"F0.wireOp",EDGE,"E12"),sQuery(id+"F0.wireOp",EDGE,"E13"),sQuery(id+"F0.wireOp",EDGE,"E14"),sQuery(id+"F0.wireOp",EDGE,"E15"),sQuery(id+"F0.wireOp",EDGE,"E16"),sQuery(id+"F0.wireOp",EDGE,"E17"),sQuery(id+"F0.wireOp",EDGE,"E18"),sQuery(id+"F0.wireOp",EDGE,"E19"),sQuery(id+"F0.wireOp",EDGE,"E20"),sQuery(id+"F0.wireOp",EDGE,"E21"),sQuery(id+"F0.wireOp",EDGE,"E22"),sQuery(id+"F0.wireOp",EDGE,"E23"),sQuery(id+"F0.wireOp",EDGE,"E24"),sQuery(id+"F0.wireOp",EDGE,"E25"),sQuery(id+"F0.wireOp",EDGE,"E26"),sQuery(id+"F0.wireOp",EDGE,"E27"),sQuery(id+"F0.wireOp",EDGE,"E28"),sQuery(id+"F0.wireOp",EDGE,"E29"),sQuery(id+"F0.wireOp",EDGE,"E30"),sQuery(id+"F0.wireOp",EDGE,"E31"),sQuery(id+"F0.wireOp",EDGE,"E32"),sQuery(id+"F0.wireOp",EDGE,"E33"),sQuery(id+"F0.wireOp",EDGE,"E34"),sQuery(id+"F0.wireOp",EDGE,"E35"),sQuery(id+"F0.wireOp",EDGE,"E36"),sQuery(id+"F0.wireOp",EDGE,"E37"),sQuery(id+"F0.wireOp",EDGE,"E38"),sQuery(id+"F0.wireOp",EDGE,"E39"),sQuery(id+"F0.wireOp",EDGE,"E40"),sQuery(id+"F0.wireOp",EDGE,"E41"),sQuery(id+"F0.wireOp",EDGE,"E42"),sQuery(id+"F0.wireOp",EDGE,"E43"),sQuery(id+"F0.wireOp",EDGE,"E44"),sQuery(id+"F0.wireOp",EDGE,"E45"),sQuery(id+"F0.wireOp",EDGE,"E46"),sQuery(id+"F0.wireOp",EDGE,"E47"),sQuery(id+"F0.wireOp",EDGE,"E48"),sQuery(id+"F0.wireOp",EDGE,"E49"),sQuery(id+"F0.wireOp",EDGE,"E50"),sQuery(id+"F0.wireOp",EDGE,"E51"),sQuery(id+"F0.wireOp",EDGE,"E52"),sQuery(id+"F0.wireOp",EDGE,"E53"),sQuery(id+"F0.wireOp",EDGE,"E54"),sQuery(id+"F0.wireOp",EDGE,"E55"),sQuery(id+"F0.wireOp",EDGE,"E56"),sQuery(id+"F0.wireOp",EDGE,"E57"),sQuery(id+"F0.wireOp",EDGE,"E58"),sQuery(id+"F0.wireOp",EDGE,"E59"),sQuery(id+"F0.wireOp",EDGE,"E60"),sQuery(id+"F0.wireOp",EDGE,"E61"),sQuery(id+"F0.wireOp",EDGE,"E62"),sQuery(id+"F0.wireOp",EDGE,"E63"),sQuery(id+"F0.wireOp",EDGE,"E64"),sQuery(id+"F0.wireOp",EDGE,"E65"),sQuery(id+"F0.wireOp",EDGE,"E66"),sQuery(id+"F0.wireOp",EDGE,"E67"),sQuery(id+"F0.wireOp",EDGE,"E68"),sQuery(id+"F0.wireOp",EDGE,"E69"),sQuery(id+"F0.wireOp",EDGE,"E70"),sQuery(id+"F0.wireOp",EDGE,"E71"),sQuery(id+"F0.wireOp",EDGE,"E72"),sQuery(id+"F0.wireOp",EDGE,"E73"),sQuery(id+"F0.wireOp",EDGE,"E74"),sQuery(id+"F0.wireOp",EDGE,"E75"),sQuery(id+"F0.wireOp",EDGE,"E76"),sQuery(id+"F0.wireOp",EDGE,"E77"),sQuery(id+"F0.wireOp",EDGE,"E78"),sQuery(id+"F0.wireOp",EDGE,"E79"),sQuery(id+"F0.wireOp",EDGE,"E80"),sQuery(id+"F0.wireOp",EDGE,"E81"),sQuery(id+"F0.wireOp",EDGE,"E82"),sQuery(id+"F0.wireOp",EDGE,"E83"),sQuery(id+"F0.wireOp",EDGE,"E84"),sQuery(id+"F0.wireOp",EDGE,"E85"),sQuery(id+"F0.wireOp",EDGE,"E86"),sQuery(id+"F0.wireOp",EDGE,"E87"),sQuery(id+"F0.wireOp",EDGE,"E88"),sQuery(id+"F0.wireOp",EDGE,"E89"),sQuery(id+"F0.wireOp",EDGE,"E90"),sQuery(id+"F0.wireOp",EDGE,"E91"),sQuery(id+"F0.wireOp",EDGE,"E92"),sQuery(id+"F0.wireOp",EDGE,"E93"),sQuery(id+"F0.wireOp",EDGE,"E94"),sQuery(id+"F0.wireOp",EDGE,"E95"),sQuery(id+"F0.wireOp",EDGE,"E96"),sQuery(id+"F0.wireOp",EDGE,"E97"),sQuery(id+"F0.wireOp",EDGE,"E98"),sQuery(id+"F0.wireOp",EDGE,"E99"),sQuery(id+"F0.wireOp",EDGE,"E100"),sQuery(id+"F0.wireOp",EDGE,"E101"),sQuery(id+"F0.wireOp",EDGE,"E102"),sQuery(id+"F0.wireOp",EDGE,"E103"),sQuery(id+"F0.wireOp",EDGE,"E104")])]}),"instanceName":"45"});
            var Q13;
            Q13=makeQuery(id+"F2.opPattern","COPY",BODY,{"derivedFrom":makeQuery(id+"F1.opExtrude","SWEPT_BODY",BODY,{"disambiguationData":[OSD([sQuery(id+"F0.wireOp",EDGE,"E1"),sQuery(id+"F0.wireOp",EDGE,"E2"),sQuery(id+"F0.wireOp",EDGE,"E3"),sQuery(id+"F0.wireOp",EDGE,"E4"),sQuery(id+"F0.wireOp",EDGE,"E5"),sQuery(id+"F0.wireOp",EDGE,"E6"),sQuery(id+"F0.wireOp",EDGE,"E7"),sQuery(id+"F0.wireOp",EDGE,"E8"),sQuery(id+"F0.wireOp",EDGE,"E9"),sQuery(id+"F0.wireOp",EDGE,"E10"),sQuery(id+"F0.wireOp",EDGE,"E11"),sQuery(id+"F0.wireOp",EDGE,"E12"),sQuery(id+"F0.wireOp",EDGE,"E13"),sQuery(id+"F0.wireOp",EDGE,"E14"),sQuery(id+"F0.wireOp",EDGE,"E15"),sQuery(id+"F0.wireOp",EDGE,"E16"),sQuery(id+"F0.wireOp",EDGE,"E17"),sQuery(id+"F0.wireOp",EDGE,"E18"),sQuery(id+"F0.wireOp",EDGE,"E19"),sQuery(id+"F0.wireOp",EDGE,"E20"),sQuery(id+"F0.wireOp",EDGE,"E21"),sQuery(id+"F0.wireOp",EDGE,"E22"),sQuery(id+"F0.wireOp",EDGE,"E23"),sQuery(id+"F0.wireOp",EDGE,"E24"),sQuery(id+"F0.wireOp",EDGE,"E25"),sQuery(id+"F0.wireOp",EDGE,"E26"),sQuery(id+"F0.wireOp",EDGE,"E27"),sQuery(id+"F0.wireOp",EDGE,"E28"),sQuery(id+"F0.wireOp",EDGE,"E29"),sQuery(id+"F0.wireOp",EDGE,"E30"),sQuery(id+"F0.wireOp",EDGE,"E31"),sQuery(id+"F0.wireOp",EDGE,"E32"),sQuery(id+"F0.wireOp",EDGE,"E33"),sQuery(id+"F0.wireOp",EDGE,"E34"),sQuery(id+"F0.wireOp",EDGE,"E35"),sQuery(id+"F0.wireOp",EDGE,"E36"),sQuery(id+"F0.wireOp",EDGE,"E37"),sQuery(id+"F0.wireOp",EDGE,"E38"),sQuery(id+"F0.wireOp",EDGE,"E39"),sQuery(id+"F0.wireOp",EDGE,"E40"),sQuery(id+"F0.wireOp",EDGE,"E41"),sQuery(id+"F0.wireOp",EDGE,"E42"),sQuery(id+"F0.wireOp",EDGE,"E43"),sQuery(id+"F0.wireOp",EDGE,"E44"),sQuery(id+"F0.wireOp",EDGE,"E45"),sQuery(id+"F0.wireOp",EDGE,"E46"),sQuery(id+"F0.wireOp",EDGE,"E47"),sQuery(id+"F0.wireOp",EDGE,"E48"),sQuery(id+"F0.wireOp",EDGE,"E49"),sQuery(id+"F0.wireOp",EDGE,"E50"),sQuery(id+"F0.wireOp",EDGE,"E51"),sQuery(id+"F0.wireOp",EDGE,"E52"),sQuery(id+"F0.wireOp",EDGE,"E53"),sQuery(id+"F0.wireOp",EDGE,"E54"),sQuery(id+"F0.wireOp",EDGE,"E55"),sQuery(id+"F0.wireOp",EDGE,"E56"),sQuery(id+"F0.wireOp",EDGE,"E57"),sQuery(id+"F0.wireOp",EDGE,"E58"),sQuery(id+"F0.wireOp",EDGE,"E59"),sQuery(id+"F0.wireOp",EDGE,"E60"),sQuery(id+"F0.wireOp",EDGE,"E61"),sQuery(id+"F0.wireOp",EDGE,"E62"),sQuery(id+"F0.wireOp",EDGE,"E63"),sQuery(id+"F0.wireOp",EDGE,"E64"),sQuery(id+"F0.wireOp",EDGE,"E65"),sQuery(id+"F0.wireOp",EDGE,"E66"),sQuery(id+"F0.wireOp",EDGE,"E67"),sQuery(id+"F0.wireOp",EDGE,"E68"),sQuery(id+"F0.wireOp",EDGE,"E69"),sQuery(id+"F0.wireOp",EDGE,"E70"),sQuery(id+"F0.wireOp",EDGE,"E71"),sQuery(id+"F0.wireOp",EDGE,"E72"),sQuery(id+"F0.wireOp",EDGE,"E73"),sQuery(id+"F0.wireOp",EDGE,"E74"),sQuery(id+"F0.wireOp",EDGE,"E75"),sQuery(id+"F0.wireOp",EDGE,"E76"),sQuery(id+"F0.wireOp",EDGE,"E77"),sQuery(id+"F0.wireOp",EDGE,"E78"),sQuery(id+"F0.wireOp",EDGE,"E79"),sQuery(id+"F0.wireOp",EDGE,"E80"),sQuery(id+"F0.wireOp",EDGE,"E81"),sQuery(id+"F0.wireOp",EDGE,"E82"),sQuery(id+"F0.wireOp",EDGE,"E83"),sQuery(id+"F0.wireOp",EDGE,"E84"),sQuery(id+"F0.wireOp",EDGE,"E85"),sQuery(id+"F0.wireOp",EDGE,"E86"),sQuery(id+"F0.wireOp",EDGE,"E87"),sQuery(id+"F0.wireOp",EDGE,"E88"),sQuery(id+"F0.wireOp",EDGE,"E89"),sQuery(id+"F0.wireOp",EDGE,"E90"),sQuery(id+"F0.wireOp",EDGE,"E91"),sQuery(id+"F0.wireOp",EDGE,"E92"),sQuery(id+"F0.wireOp",EDGE,"E93"),sQuery(id+"F0.wireOp",EDGE,"E94"),sQuery(id+"F0.wireOp",EDGE,"E95"),sQuery(id+"F0.wireOp",EDGE,"E96"),sQuery(id+"F0.wireOp",EDGE,"E97"),sQuery(id+"F0.wireOp",EDGE,"E98"),sQuery(id+"F0.wireOp",EDGE,"E99"),sQuery(id+"F0.wireOp",EDGE,"E100"),sQuery(id+"F0.wireOp",EDGE,"E101"),sQuery(id+"F0.wireOp",EDGE,"E102"),sQuery(id+"F0.wireOp",EDGE,"E103"),sQuery(id+"F0.wireOp",EDGE,"E104")])]}),"instanceName":"46"});
            var Q14;
            Q14=makeQuery(id+"F2.opPattern","COPY",BODY,{"derivedFrom":makeQuery(id+"F1.opExtrude","SWEPT_BODY",BODY,{"disambiguationData":[OSD([sQuery(id+"F0.wireOp",EDGE,"E1"),sQuery(id+"F0.wireOp",EDGE,"E2"),sQuery(id+"F0.wireOp",EDGE,"E3"),sQuery(id+"F0.wireOp",EDGE,"E4"),sQuery(id+"F0.wireOp",EDGE,"E5"),sQuery(id+"F0.wireOp",EDGE,"E6"),sQuery(id+"F0.wireOp",EDGE,"E7"),sQuery(id+"F0.wireOp",EDGE,"E8"),sQuery(id+"F0.wireOp",EDGE,"E9"),sQuery(id+"F0.wireOp",EDGE,"E10"),sQuery(id+"F0.wireOp",EDGE,"E11"),sQuery(id+"F0.wireOp",EDGE,"E12"),sQuery(id+"F0.wireOp",EDGE,"E13"),sQuery(id+"F0.wireOp",EDGE,"E14"),sQuery(id+"F0.wireOp",EDGE,"E15"),sQuery(id+"F0.wireOp",EDGE,"E16"),sQuery(id+"F0.wireOp",EDGE,"E17"),sQuery(id+"F0.wireOp",EDGE,"E18"),sQuery(id+"F0.wireOp",EDGE,"E19"),sQuery(id+"F0.wireOp",EDGE,"E20"),sQuery(id+"F0.wireOp",EDGE,"E21"),sQuery(id+"F0.wireOp",EDGE,"E22"),sQuery(id+"F0.wireOp",EDGE,"E23"),sQuery(id+"F0.wireOp",EDGE,"E24"),sQuery(id+"F0.wireOp",EDGE,"E25"),sQuery(id+"F0.wireOp",EDGE,"E26"),sQuery(id+"F0.wireOp",EDGE,"E27"),sQuery(id+"F0.wireOp",EDGE,"E28"),sQuery(id+"F0.wireOp",EDGE,"E29"),sQuery(id+"F0.wireOp",EDGE,"E30"),sQuery(id+"F0.wireOp",EDGE,"E31"),sQuery(id+"F0.wireOp",EDGE,"E32"),sQuery(id+"F0.wireOp",EDGE,"E33"),sQuery(id+"F0.wireOp",EDGE,"E34"),sQuery(id+"F0.wireOp",EDGE,"E35"),sQuery(id+"F0.wireOp",EDGE,"E36"),sQuery(id+"F0.wireOp",EDGE,"E37"),sQuery(id+"F0.wireOp",EDGE,"E38"),sQuery(id+"F0.wireOp",EDGE,"E39"),sQuery(id+"F0.wireOp",EDGE,"E40"),sQuery(id+"F0.wireOp",EDGE,"E41"),sQuery(id+"F0.wireOp",EDGE,"E42"),sQuery(id+"F0.wireOp",EDGE,"E43"),sQuery(id+"F0.wireOp",EDGE,"E44"),sQuery(id+"F0.wireOp",EDGE,"E45"),sQuery(id+"F0.wireOp",EDGE,"E46"),sQuery(id+"F0.wireOp",EDGE,"E47"),sQuery(id+"F0.wireOp",EDGE,"E48"),sQuery(id+"F0.wireOp",EDGE,"E49"),sQuery(id+"F0.wireOp",EDGE,"E50"),sQuery(id+"F0.wireOp",EDGE,"E51"),sQuery(id+"F0.wireOp",EDGE,"E52"),sQuery(id+"F0.wireOp",EDGE,"E53"),sQuery(id+"F0.wireOp",EDGE,"E54"),sQuery(id+"F0.wireOp",EDGE,"E55"),sQuery(id+"F0.wireOp",EDGE,"E56"),sQuery(id+"F0.wireOp",EDGE,"E57"),sQuery(id+"F0.wireOp",EDGE,"E58"),sQuery(id+"F0.wireOp",EDGE,"E59"),sQuery(id+"F0.wireOp",EDGE,"E60"),sQuery(id+"F0.wireOp",EDGE,"E61"),sQuery(id+"F0.wireOp",EDGE,"E62"),sQuery(id+"F0.wireOp",EDGE,"E63"),sQuery(id+"F0.wireOp",EDGE,"E64"),sQuery(id+"F0.wireOp",EDGE,"E65"),sQuery(id+"F0.wireOp",EDGE,"E66"),sQuery(id+"F0.wireOp",EDGE,"E67"),sQuery(id+"F0.wireOp",EDGE,"E68"),sQuery(id+"F0.wireOp",EDGE,"E69"),sQuery(id+"F0.wireOp",EDGE,"E70"),sQuery(id+"F0.wireOp",EDGE,"E71"),sQuery(id+"F0.wireOp",EDGE,"E72"),sQuery(id+"F0.wireOp",EDGE,"E73"),sQuery(id+"F0.wireOp",EDGE,"E74"),sQuery(id+"F0.wireOp",EDGE,"E75"),sQuery(id+"F0.wireOp",EDGE,"E76"),sQuery(id+"F0.wireOp",EDGE,"E77"),sQuery(id+"F0.wireOp",EDGE,"E78"),sQuery(id+"F0.wireOp",EDGE,"E79"),sQuery(id+"F0.wireOp",EDGE,"E80"),sQuery(id+"F0.wireOp",EDGE,"E81"),sQuery(id+"F0.wireOp",EDGE,"E82"),sQuery(id+"F0.wireOp",EDGE,"E83"),sQuery(id+"F0.wireOp",EDGE,"E84"),sQuery(id+"F0.wireOp",EDGE,"E85"),sQuery(id+"F0.wireOp",EDGE,"E86"),sQuery(id+"F0.wireOp",EDGE,"E87"),sQuery(id+"F0.wireOp",EDGE,"E88"),sQuery(id+"F0.wireOp",EDGE,"E89"),sQuery(id+"F0.wireOp",EDGE,"E90"),sQuery(id+"F0.wireOp",EDGE,"E91"),sQuery(id+"F0.wireOp",EDGE,"E92"),sQuery(id+"F0.wireOp",EDGE,"E93"),sQuery(id+"F0.wireOp",EDGE,"E94"),sQuery(id+"F0.wireOp",EDGE,"E95"),sQuery(id+"F0.wireOp",EDGE,"E96"),sQuery(id+"F0.wireOp",EDGE,"E97"),sQuery(id+"F0.wireOp",EDGE,"E98"),sQuery(id+"F0.wireOp",EDGE,"E99"),sQuery(id+"F0.wireOp",EDGE,"E100"),sQuery(id+"F0.wireOp",EDGE,"E101"),sQuery(id+"F0.wireOp",EDGE,"E102"),sQuery(id+"F0.wireOp",EDGE,"E103"),sQuery(id+"F0.wireOp",EDGE,"E104")])]}),"instanceName":"47"});
            var Q15;
            Q15=makeQuery(id+"F2.opPattern","COPY",BODY,{"derivedFrom":makeQuery(id+"F1.opExtrude","SWEPT_BODY",BODY,{"disambiguationData":[OSD([sQuery(id+"F0.wireOp",EDGE,"E1"),sQuery(id+"F0.wireOp",EDGE,"E2"),sQuery(id+"F0.wireOp",EDGE,"E3"),sQuery(id+"F0.wireOp",EDGE,"E4"),sQuery(id+"F0.wireOp",EDGE,"E5"),sQuery(id+"F0.wireOp",EDGE,"E6"),sQuery(id+"F0.wireOp",EDGE,"E7"),sQuery(id+"F0.wireOp",EDGE,"E8"),sQuery(id+"F0.wireOp",EDGE,"E9"),sQuery(id+"F0.wireOp",EDGE,"E10"),sQuery(id+"F0.wireOp",EDGE,"E11"),sQuery(id+"F0.wireOp",EDGE,"E12"),sQuery(id+"F0.wireOp",EDGE,"E13"),sQuery(id+"F0.wireOp",EDGE,"E14"),sQuery(id+"F0.wireOp",EDGE,"E15"),sQuery(id+"F0.wireOp",EDGE,"E16"),sQuery(id+"F0.wireOp",EDGE,"E17"),sQuery(id+"F0.wireOp",EDGE,"E18"),sQuery(id+"F0.wireOp",EDGE,"E19"),sQuery(id+"F0.wireOp",EDGE,"E20"),sQuery(id+"F0.wireOp",EDGE,"E21"),sQuery(id+"F0.wireOp",EDGE,"E22"),sQuery(id+"F0.wireOp",EDGE,"E23"),sQuery(id+"F0.wireOp",EDGE,"E24"),sQuery(id+"F0.wireOp",EDGE,"E25"),sQuery(id+"F0.wireOp",EDGE,"E26"),sQuery(id+"F0.wireOp",EDGE,"E27"),sQuery(id+"F0.wireOp",EDGE,"E28"),sQuery(id+"F0.wireOp",EDGE,"E29"),sQuery(id+"F0.wireOp",EDGE,"E30"),sQuery(id+"F0.wireOp",EDGE,"E31"),sQuery(id+"F0.wireOp",EDGE,"E32"),sQuery(id+"F0.wireOp",EDGE,"E33"),sQuery(id+"F0.wireOp",EDGE,"E34"),sQuery(id+"F0.wireOp",EDGE,"E35"),sQuery(id+"F0.wireOp",EDGE,"E36"),sQuery(id+"F0.wireOp",EDGE,"E37"),sQuery(id+"F0.wireOp",EDGE,"E38"),sQuery(id+"F0.wireOp",EDGE,"E39"),sQuery(id+"F0.wireOp",EDGE,"E40"),sQuery(id+"F0.wireOp",EDGE,"E41"),sQuery(id+"F0.wireOp",EDGE,"E42"),sQuery(id+"F0.wireOp",EDGE,"E43"),sQuery(id+"F0.wireOp",EDGE,"E44"),sQuery(id+"F0.wireOp",EDGE,"E45"),sQuery(id+"F0.wireOp",EDGE,"E46"),sQuery(id+"F0.wireOp",EDGE,"E47"),sQuery(id+"F0.wireOp",EDGE,"E48"),sQuery(id+"F0.wireOp",EDGE,"E49"),sQuery(id+"F0.wireOp",EDGE,"E50"),sQuery(id+"F0.wireOp",EDGE,"E51"),sQuery(id+"F0.wireOp",EDGE,"E52"),sQuery(id+"F0.wireOp",EDGE,"E53"),sQuery(id+"F0.wireOp",EDGE,"E54"),sQuery(id+"F0.wireOp",EDGE,"E55"),sQuery(id+"F0.wireOp",EDGE,"E56"),sQuery(id+"F0.wireOp",EDGE,"E57"),sQuery(id+"F0.wireOp",EDGE,"E58"),sQuery(id+"F0.wireOp",EDGE,"E59"),sQuery(id+"F0.wireOp",EDGE,"E60"),sQuery(id+"F0.wireOp",EDGE,"E61"),sQuery(id+"F0.wireOp",EDGE,"E62"),sQuery(id+"F0.wireOp",EDGE,"E63"),sQuery(id+"F0.wireOp",EDGE,"E64"),sQuery(id+"F0.wireOp",EDGE,"E65"),sQuery(id+"F0.wireOp",EDGE,"E66"),sQuery(id+"F0.wireOp",EDGE,"E67"),sQuery(id+"F0.wireOp",EDGE,"E68"),sQuery(id+"F0.wireOp",EDGE,"E69"),sQuery(id+"F0.wireOp",EDGE,"E70"),sQuery(id+"F0.wireOp",EDGE,"E71"),sQuery(id+"F0.wireOp",EDGE,"E72"),sQuery(id+"F0.wireOp",EDGE,"E73"),sQuery(id+"F0.wireOp",EDGE,"E74"),sQuery(id+"F0.wireOp",EDGE,"E75"),sQuery(id+"F0.wireOp",EDGE,"E76"),sQuery(id+"F0.wireOp",EDGE,"E77"),sQuery(id+"F0.wireOp",EDGE,"E78"),sQuery(id+"F0.wireOp",EDGE,"E79"),sQuery(id+"F0.wireOp",EDGE,"E80"),sQuery(id+"F0.wireOp",EDGE,"E81"),sQuery(id+"F0.wireOp",EDGE,"E82"),sQuery(id+"F0.wireOp",EDGE,"E83"),sQuery(id+"F0.wireOp",EDGE,"E84"),sQuery(id+"F0.wireOp",EDGE,"E85"),sQuery(id+"F0.wireOp",EDGE,"E86"),sQuery(id+"F0.wireOp",EDGE,"E87"),sQuery(id+"F0.wireOp",EDGE,"E88"),sQuery(id+"F0.wireOp",EDGE,"E89"),sQuery(id+"F0.wireOp",EDGE,"E90"),sQuery(id+"F0.wireOp",EDGE,"E91"),sQuery(id+"F0.wireOp",EDGE,"E92"),sQuery(id+"F0.wireOp",EDGE,"E93"),sQuery(id+"F0.wireOp",EDGE,"E94"),sQuery(id+"F0.wireOp",EDGE,"E95"),sQuery(id+"F0.wireOp",EDGE,"E96"),sQuery(id+"F0.wireOp",EDGE,"E97"),sQuery(id+"F0.wireOp",EDGE,"E98"),sQuery(id+"F0.wireOp",EDGE,"E99"),sQuery(id+"F0.wireOp",EDGE,"E100"),sQuery(id+"F0.wireOp",EDGE,"E101"),sQuery(id+"F0.wireOp",EDGE,"E102"),sQuery(id+"F0.wireOp",EDGE,"E103"),sQuery(id+"F0.wireOp",EDGE,"E104")])]}),"instanceName":"48"});
            var Q16;
            Q16=makeQuery(id+"F2.opPattern","COPY",BODY,{"derivedFrom":makeQuery(id+"F1.opExtrude","SWEPT_BODY",BODY,{"disambiguationData":[OSD([sQuery(id+"F0.wireOp",EDGE,"E1"),sQuery(id+"F0.wireOp",EDGE,"E2"),sQuery(id+"F0.wireOp",EDGE,"E3"),sQuery(id+"F0.wireOp",EDGE,"E4"),sQuery(id+"F0.wireOp",EDGE,"E5"),sQuery(id+"F0.wireOp",EDGE,"E6"),sQuery(id+"F0.wireOp",EDGE,"E7"),sQuery(id+"F0.wireOp",EDGE,"E8"),sQuery(id+"F0.wireOp",EDGE,"E9"),sQuery(id+"F0.wireOp",EDGE,"E10"),sQuery(id+"F0.wireOp",EDGE,"E11"),sQuery(id+"F0.wireOp",EDGE,"E12"),sQuery(id+"F0.wireOp",EDGE,"E13"),sQuery(id+"F0.wireOp",EDGE,"E14"),sQuery(id+"F0.wireOp",EDGE,"E15"),sQuery(id+"F0.wireOp",EDGE,"E16"),sQuery(id+"F0.wireOp",EDGE,"E17"),sQuery(id+"F0.wireOp",EDGE,"E18"),sQuery(id+"F0.wireOp",EDGE,"E19"),sQuery(id+"F0.wireOp",EDGE,"E20"),sQuery(id+"F0.wireOp",EDGE,"E21"),sQuery(id+"F0.wireOp",EDGE,"E22"),sQuery(id+"F0.wireOp",EDGE,"E23"),sQuery(id+"F0.wireOp",EDGE,"E24"),sQuery(id+"F0.wireOp",EDGE,"E25"),sQuery(id+"F0.wireOp",EDGE,"E26"),sQuery(id+"F0.wireOp",EDGE,"E27"),sQuery(id+"F0.wireOp",EDGE,"E28"),sQuery(id+"F0.wireOp",EDGE,"E29"),sQuery(id+"F0.wireOp",EDGE,"E30"),sQuery(id+"F0.wireOp",EDGE,"E31"),sQuery(id+"F0.wireOp",EDGE,"E32"),sQuery(id+"F0.wireOp",EDGE,"E33"),sQuery(id+"F0.wireOp",EDGE,"E34"),sQuery(id+"F0.wireOp",EDGE,"E35"),sQuery(id+"F0.wireOp",EDGE,"E36"),sQuery(id+"F0.wireOp",EDGE,"E37"),sQuery(id+"F0.wireOp",EDGE,"E38"),sQuery(id+"F0.wireOp",EDGE,"E39"),sQuery(id+"F0.wireOp",EDGE,"E40"),sQuery(id+"F0.wireOp",EDGE,"E41"),sQuery(id+"F0.wireOp",EDGE,"E42"),sQuery(id+"F0.wireOp",EDGE,"E43"),sQuery(id+"F0.wireOp",EDGE,"E44"),sQuery(id+"F0.wireOp",EDGE,"E45"),sQuery(id+"F0.wireOp",EDGE,"E46"),sQuery(id+"F0.wireOp",EDGE,"E47"),sQuery(id+"F0.wireOp",EDGE,"E48"),sQuery(id+"F0.wireOp",EDGE,"E49"),sQuery(id+"F0.wireOp",EDGE,"E50"),sQuery(id+"F0.wireOp",EDGE,"E51"),sQuery(id+"F0.wireOp",EDGE,"E52"),sQuery(id+"F0.wireOp",EDGE,"E53"),sQuery(id+"F0.wireOp",EDGE,"E54"),sQuery(id+"F0.wireOp",EDGE,"E55"),sQuery(id+"F0.wireOp",EDGE,"E56"),sQuery(id+"F0.wireOp",EDGE,"E57"),sQuery(id+"F0.wireOp",EDGE,"E58"),sQuery(id+"F0.wireOp",EDGE,"E59"),sQuery(id+"F0.wireOp",EDGE,"E60"),sQuery(id+"F0.wireOp",EDGE,"E61"),sQuery(id+"F0.wireOp",EDGE,"E62"),sQuery(id+"F0.wireOp",EDGE,"E63"),sQuery(id+"F0.wireOp",EDGE,"E64"),sQuery(id+"F0.wireOp",EDGE,"E65"),sQuery(id+"F0.wireOp",EDGE,"E66"),sQuery(id+"F0.wireOp",EDGE,"E67"),sQuery(id+"F0.wireOp",EDGE,"E68"),sQuery(id+"F0.wireOp",EDGE,"E69"),sQuery(id+"F0.wireOp",EDGE,"E70"),sQuery(id+"F0.wireOp",EDGE,"E71"),sQuery(id+"F0.wireOp",EDGE,"E72"),sQuery(id+"F0.wireOp",EDGE,"E73"),sQuery(id+"F0.wireOp",EDGE,"E74"),sQuery(id+"F0.wireOp",EDGE,"E75"),sQuery(id+"F0.wireOp",EDGE,"E76"),sQuery(id+"F0.wireOp",EDGE,"E77"),sQuery(id+"F0.wireOp",EDGE,"E78"),sQuery(id+"F0.wireOp",EDGE,"E79"),sQuery(id+"F0.wireOp",EDGE,"E80"),sQuery(id+"F0.wireOp",EDGE,"E81"),sQuery(id+"F0.wireOp",EDGE,"E82"),sQuery(id+"F0.wireOp",EDGE,"E83"),sQuery(id+"F0.wireOp",EDGE,"E84"),sQuery(id+"F0.wireOp",EDGE,"E85"),sQuery(id+"F0.wireOp",EDGE,"E86"),sQuery(id+"F0.wireOp",EDGE,"E87"),sQuery(id+"F0.wireOp",EDGE,"E88"),sQuery(id+"F0.wireOp",EDGE,"E89"),sQuery(id+"F0.wireOp",EDGE,"E90"),sQuery(id+"F0.wireOp",EDGE,"E91"),sQuery(id+"F0.wireOp",EDGE,"E92"),sQuery(id+"F0.wireOp",EDGE,"E93"),sQuery(id+"F0.wireOp",EDGE,"E94"),sQuery(id+"F0.wireOp",EDGE,"E95"),sQuery(id+"F0.wireOp",EDGE,"E96"),sQuery(id+"F0.wireOp",EDGE,"E97"),sQuery(id+"F0.wireOp",EDGE,"E98"),sQuery(id+"F0.wireOp",EDGE,"E99"),sQuery(id+"F0.wireOp",EDGE,"E100"),sQuery(id+"F0.wireOp",EDGE,"E101"),sQuery(id+"F0.wireOp",EDGE,"E102"),sQuery(id+"F0.wireOp",EDGE,"E103"),sQuery(id+"F0.wireOp",EDGE,"E104")])]}),"instanceName":"49"});
            var Q17;
            Q17=makeQuery(id+"F2.opPattern","COPY",BODY,{"derivedFrom":makeQuery(id+"F1.opExtrude","SWEPT_BODY",BODY,{"disambiguationData":[OSD([sQuery(id+"F0.wireOp",EDGE,"E1"),sQuery(id+"F0.wireOp",EDGE,"E2"),sQuery(id+"F0.wireOp",EDGE,"E3"),sQuery(id+"F0.wireOp",EDGE,"E4"),sQuery(id+"F0.wireOp",EDGE,"E5"),sQuery(id+"F0.wireOp",EDGE,"E6"),sQuery(id+"F0.wireOp",EDGE,"E7"),sQuery(id+"F0.wireOp",EDGE,"E8"),sQuery(id+"F0.wireOp",EDGE,"E9"),sQuery(id+"F0.wireOp",EDGE,"E10"),sQuery(id+"F0.wireOp",EDGE,"E11"),sQuery(id+"F0.wireOp",EDGE,"E12"),sQuery(id+"F0.wireOp",EDGE,"E13"),sQuery(id+"F0.wireOp",EDGE,"E14"),sQuery(id+"F0.wireOp",EDGE,"E15"),sQuery(id+"F0.wireOp",EDGE,"E16"),sQuery(id+"F0.wireOp",EDGE,"E17"),sQuery(id+"F0.wireOp",EDGE,"E18"),sQuery(id+"F0.wireOp",EDGE,"E19"),sQuery(id+"F0.wireOp",EDGE,"E20"),sQuery(id+"F0.wireOp",EDGE,"E21"),sQuery(id+"F0.wireOp",EDGE,"E22"),sQuery(id+"F0.wireOp",EDGE,"E23"),sQuery(id+"F0.wireOp",EDGE,"E24"),sQuery(id+"F0.wireOp",EDGE,"E25"),sQuery(id+"F0.wireOp",EDGE,"E26"),sQuery(id+"F0.wireOp",EDGE,"E27"),sQuery(id+"F0.wireOp",EDGE,"E28"),sQuery(id+"F0.wireOp",EDGE,"E29"),sQuery(id+"F0.wireOp",EDGE,"E30"),sQuery(id+"F0.wireOp",EDGE,"E31"),sQuery(id+"F0.wireOp",EDGE,"E32"),sQuery(id+"F0.wireOp",EDGE,"E33"),sQuery(id+"F0.wireOp",EDGE,"E34"),sQuery(id+"F0.wireOp",EDGE,"E35"),sQuery(id+"F0.wireOp",EDGE,"E36"),sQuery(id+"F0.wireOp",EDGE,"E37"),sQuery(id+"F0.wireOp",EDGE,"E38"),sQuery(id+"F0.wireOp",EDGE,"E39"),sQuery(id+"F0.wireOp",EDGE,"E40"),sQuery(id+"F0.wireOp",EDGE,"E41"),sQuery(id+"F0.wireOp",EDGE,"E42"),sQuery(id+"F0.wireOp",EDGE,"E43"),sQuery(id+"F0.wireOp",EDGE,"E44"),sQuery(id+"F0.wireOp",EDGE,"E45"),sQuery(id+"F0.wireOp",EDGE,"E46"),sQuery(id+"F0.wireOp",EDGE,"E47"),sQuery(id+"F0.wireOp",EDGE,"E48"),sQuery(id+"F0.wireOp",EDGE,"E49"),sQuery(id+"F0.wireOp",EDGE,"E50"),sQuery(id+"F0.wireOp",EDGE,"E51"),sQuery(id+"F0.wireOp",EDGE,"E52"),sQuery(id+"F0.wireOp",EDGE,"E53"),sQuery(id+"F0.wireOp",EDGE,"E54"),sQuery(id+"F0.wireOp",EDGE,"E55"),sQuery(id+"F0.wireOp",EDGE,"E56"),sQuery(id+"F0.wireOp",EDGE,"E57"),sQuery(id+"F0.wireOp",EDGE,"E58"),sQuery(id+"F0.wireOp",EDGE,"E59"),sQuery(id+"F0.wireOp",EDGE,"E60"),sQuery(id+"F0.wireOp",EDGE,"E61"),sQuery(id+"F0.wireOp",EDGE,"E62"),sQuery(id+"F0.wireOp",EDGE,"E63"),sQuery(id+"F0.wireOp",EDGE,"E64"),sQuery(id+"F0.wireOp",EDGE,"E65"),sQuery(id+"F0.wireOp",EDGE,"E66"),sQuery(id+"F0.wireOp",EDGE,"E67"),sQuery(id+"F0.wireOp",EDGE,"E68"),sQuery(id+"F0.wireOp",EDGE,"E69"),sQuery(id+"F0.wireOp",EDGE,"E70"),sQuery(id+"F0.wireOp",EDGE,"E71"),sQuery(id+"F0.wireOp",EDGE,"E72"),sQuery(id+"F0.wireOp",EDGE,"E73"),sQuery(id+"F0.wireOp",EDGE,"E74"),sQuery(id+"F0.wireOp",EDGE,"E75"),sQuery(id+"F0.wireOp",EDGE,"E76"),sQuery(id+"F0.wireOp",EDGE,"E77"),sQuery(id+"F0.wireOp",EDGE,"E78"),sQuery(id+"F0.wireOp",EDGE,"E79"),sQuery(id+"F0.wireOp",EDGE,"E80"),sQuery(id+"F0.wireOp",EDGE,"E81"),sQuery(id+"F0.wireOp",EDGE,"E82"),sQuery(id+"F0.wireOp",EDGE,"E83"),sQuery(id+"F0.wireOp",EDGE,"E84"),sQuery(id+"F0.wireOp",EDGE,"E85"),sQuery(id+"F0.wireOp",EDGE,"E86"),sQuery(id+"F0.wireOp",EDGE,"E87"),sQuery(id+"F0.wireOp",EDGE,"E88"),sQuery(id+"F0.wireOp",EDGE,"E89"),sQuery(id+"F0.wireOp",EDGE,"E90"),sQuery(id+"F0.wireOp",EDGE,"E91"),sQuery(id+"F0.wireOp",EDGE,"E92"),sQuery(id+"F0.wireOp",EDGE,"E93"),sQuery(id+"F0.wireOp",EDGE,"E94"),sQuery(id+"F0.wireOp",EDGE,"E95"),sQuery(id+"F0.wireOp",EDGE,"E96"),sQuery(id+"F0.wireOp",EDGE,"E97"),sQuery(id+"F0.wireOp",EDGE,"E98"),sQuery(id+"F0.wireOp",EDGE,"E99"),sQuery(id+"F0.wireOp",EDGE,"E100"),sQuery(id+"F0.wireOp",EDGE,"E101"),sQuery(id+"F0.wireOp",EDGE,"E102"),sQuery(id+"F0.wireOp",EDGE,"E103"),sQuery(id+"F0.wireOp",EDGE,"E104")])]}),"instanceName":"50"});
            var Q18;
            Q18=makeQuery(id+"F2.opPattern","COPY",BODY,{"derivedFrom":makeQuery(id+"F1.opExtrude","SWEPT_BODY",BODY,{"disambiguationData":[OSD([sQuery(id+"F0.wireOp",EDGE,"E1"),sQuery(id+"F0.wireOp",EDGE,"E2"),sQuery(id+"F0.wireOp",EDGE,"E3"),sQuery(id+"F0.wireOp",EDGE,"E4"),sQuery(id+"F0.wireOp",EDGE,"E5"),sQuery(id+"F0.wireOp",EDGE,"E6"),sQuery(id+"F0.wireOp",EDGE,"E7"),sQuery(id+"F0.wireOp",EDGE,"E8"),sQuery(id+"F0.wireOp",EDGE,"E9"),sQuery(id+"F0.wireOp",EDGE,"E10"),sQuery(id+"F0.wireOp",EDGE,"E11"),sQuery(id+"F0.wireOp",EDGE,"E12"),sQuery(id+"F0.wireOp",EDGE,"E13"),sQuery(id+"F0.wireOp",EDGE,"E14"),sQuery(id+"F0.wireOp",EDGE,"E15"),sQuery(id+"F0.wireOp",EDGE,"E16"),sQuery(id+"F0.wireOp",EDGE,"E17"),sQuery(id+"F0.wireOp",EDGE,"E18"),sQuery(id+"F0.wireOp",EDGE,"E19"),sQuery(id+"F0.wireOp",EDGE,"E20"),sQuery(id+"F0.wireOp",EDGE,"E21"),sQuery(id+"F0.wireOp",EDGE,"E22"),sQuery(id+"F0.wireOp",EDGE,"E23"),sQuery(id+"F0.wireOp",EDGE,"E24"),sQuery(id+"F0.wireOp",EDGE,"E25"),sQuery(id+"F0.wireOp",EDGE,"E26"),sQuery(id+"F0.wireOp",EDGE,"E27"),sQuery(id+"F0.wireOp",EDGE,"E28"),sQuery(id+"F0.wireOp",EDGE,"E29"),sQuery(id+"F0.wireOp",EDGE,"E30"),sQuery(id+"F0.wireOp",EDGE,"E31"),sQuery(id+"F0.wireOp",EDGE,"E32"),sQuery(id+"F0.wireOp",EDGE,"E33"),sQuery(id+"F0.wireOp",EDGE,"E34"),sQuery(id+"F0.wireOp",EDGE,"E35"),sQuery(id+"F0.wireOp",EDGE,"E36"),sQuery(id+"F0.wireOp",EDGE,"E37"),sQuery(id+"F0.wireOp",EDGE,"E38"),sQuery(id+"F0.wireOp",EDGE,"E39"),sQuery(id+"F0.wireOp",EDGE,"E40"),sQuery(id+"F0.wireOp",EDGE,"E41"),sQuery(id+"F0.wireOp",EDGE,"E42"),sQuery(id+"F0.wireOp",EDGE,"E43"),sQuery(id+"F0.wireOp",EDGE,"E44"),sQuery(id+"F0.wireOp",EDGE,"E45"),sQuery(id+"F0.wireOp",EDGE,"E46"),sQuery(id+"F0.wireOp",EDGE,"E47"),sQuery(id+"F0.wireOp",EDGE,"E48"),sQuery(id+"F0.wireOp",EDGE,"E49"),sQuery(id+"F0.wireOp",EDGE,"E50"),sQuery(id+"F0.wireOp",EDGE,"E51"),sQuery(id+"F0.wireOp",EDGE,"E52"),sQuery(id+"F0.wireOp",EDGE,"E53"),sQuery(id+"F0.wireOp",EDGE,"E54"),sQuery(id+"F0.wireOp",EDGE,"E55"),sQuery(id+"F0.wireOp",EDGE,"E56"),sQuery(id+"F0.wireOp",EDGE,"E57"),sQuery(id+"F0.wireOp",EDGE,"E58"),sQuery(id+"F0.wireOp",EDGE,"E59"),sQuery(id+"F0.wireOp",EDGE,"E60"),sQuery(id+"F0.wireOp",EDGE,"E61"),sQuery(id+"F0.wireOp",EDGE,"E62"),sQuery(id+"F0.wireOp",EDGE,"E63"),sQuery(id+"F0.wireOp",EDGE,"E64"),sQuery(id+"F0.wireOp",EDGE,"E65"),sQuery(id+"F0.wireOp",EDGE,"E66"),sQuery(id+"F0.wireOp",EDGE,"E67"),sQuery(id+"F0.wireOp",EDGE,"E68"),sQuery(id+"F0.wireOp",EDGE,"E69"),sQuery(id+"F0.wireOp",EDGE,"E70"),sQuery(id+"F0.wireOp",EDGE,"E71"),sQuery(id+"F0.wireOp",EDGE,"E72"),sQuery(id+"F0.wireOp",EDGE,"E73"),sQuery(id+"F0.wireOp",EDGE,"E74"),sQuery(id+"F0.wireOp",EDGE,"E75"),sQuery(id+"F0.wireOp",EDGE,"E76"),sQuery(id+"F0.wireOp",EDGE,"E77"),sQuery(id+"F0.wireOp",EDGE,"E78"),sQuery(id+"F0.wireOp",EDGE,"E79"),sQuery(id+"F0.wireOp",EDGE,"E80"),sQuery(id+"F0.wireOp",EDGE,"E81"),sQuery(id+"F0.wireOp",EDGE,"E82"),sQuery(id+"F0.wireOp",EDGE,"E83"),sQuery(id+"F0.wireOp",EDGE,"E84"),sQuery(id+"F0.wireOp",EDGE,"E85"),sQuery(id+"F0.wireOp",EDGE,"E86"),sQuery(id+"F0.wireOp",EDGE,"E87"),sQuery(id+"F0.wireOp",EDGE,"E88"),sQuery(id+"F0.wireOp",EDGE,"E89"),sQuery(id+"F0.wireOp",EDGE,"E90"),sQuery(id+"F0.wireOp",EDGE,"E91"),sQuery(id+"F0.wireOp",EDGE,"E92"),sQuery(id+"F0.wireOp",EDGE,"E93"),sQuery(id+"F0.wireOp",EDGE,"E94"),sQuery(id+"F0.wireOp",EDGE,"E95"),sQuery(id+"F0.wireOp",EDGE,"E96"),sQuery(id+"F0.wireOp",EDGE,"E97"),sQuery(id+"F0.wireOp",EDGE,"E98"),sQuery(id+"F0.wireOp",EDGE,"E99"),sQuery(id+"F0.wireOp",EDGE,"E100"),sQuery(id+"F0.wireOp",EDGE,"E101"),sQuery(id+"F0.wireOp",EDGE,"E102"),sQuery(id+"F0.wireOp",EDGE,"E103"),sQuery(id+"F0.wireOp",EDGE,"E104")])]}),"instanceName":"51"});
            var Q19;
            Q19=makeQuery(id+"F2.opPattern","COPY",BODY,{"derivedFrom":makeQuery(id+"F1.opExtrude","SWEPT_BODY",BODY,{"disambiguationData":[OSD([sQuery(id+"F0.wireOp",EDGE,"E1"),sQuery(id+"F0.wireOp",EDGE,"E2"),sQuery(id+"F0.wireOp",EDGE,"E3"),sQuery(id+"F0.wireOp",EDGE,"E4"),sQuery(id+"F0.wireOp",EDGE,"E5"),sQuery(id+"F0.wireOp",EDGE,"E6"),sQuery(id+"F0.wireOp",EDGE,"E7"),sQuery(id+"F0.wireOp",EDGE,"E8"),sQuery(id+"F0.wireOp",EDGE,"E9"),sQuery(id+"F0.wireOp",EDGE,"E10"),sQuery(id+"F0.wireOp",EDGE,"E11"),sQuery(id+"F0.wireOp",EDGE,"E12"),sQuery(id+"F0.wireOp",EDGE,"E13"),sQuery(id+"F0.wireOp",EDGE,"E14"),sQuery(id+"F0.wireOp",EDGE,"E15"),sQuery(id+"F0.wireOp",EDGE,"E16"),sQuery(id+"F0.wireOp",EDGE,"E17"),sQuery(id+"F0.wireOp",EDGE,"E18"),sQuery(id+"F0.wireOp",EDGE,"E19"),sQuery(id+"F0.wireOp",EDGE,"E20"),sQuery(id+"F0.wireOp",EDGE,"E21"),sQuery(id+"F0.wireOp",EDGE,"E22"),sQuery(id+"F0.wireOp",EDGE,"E23"),sQuery(id+"F0.wireOp",EDGE,"E24"),sQuery(id+"F0.wireOp",EDGE,"E25"),sQuery(id+"F0.wireOp",EDGE,"E26"),sQuery(id+"F0.wireOp",EDGE,"E27"),sQuery(id+"F0.wireOp",EDGE,"E28"),sQuery(id+"F0.wireOp",EDGE,"E29"),sQuery(id+"F0.wireOp",EDGE,"E30"),sQuery(id+"F0.wireOp",EDGE,"E31"),sQuery(id+"F0.wireOp",EDGE,"E32"),sQuery(id+"F0.wireOp",EDGE,"E33"),sQuery(id+"F0.wireOp",EDGE,"E34"),sQuery(id+"F0.wireOp",EDGE,"E35"),sQuery(id+"F0.wireOp",EDGE,"E36"),sQuery(id+"F0.wireOp",EDGE,"E37"),sQuery(id+"F0.wireOp",EDGE,"E38"),sQuery(id+"F0.wireOp",EDGE,"E39"),sQuery(id+"F0.wireOp",EDGE,"E40"),sQuery(id+"F0.wireOp",EDGE,"E41"),sQuery(id+"F0.wireOp",EDGE,"E42"),sQuery(id+"F0.wireOp",EDGE,"E43"),sQuery(id+"F0.wireOp",EDGE,"E44"),sQuery(id+"F0.wireOp",EDGE,"E45"),sQuery(id+"F0.wireOp",EDGE,"E46"),sQuery(id+"F0.wireOp",EDGE,"E47"),sQuery(id+"F0.wireOp",EDGE,"E48"),sQuery(id+"F0.wireOp",EDGE,"E49"),sQuery(id+"F0.wireOp",EDGE,"E50"),sQuery(id+"F0.wireOp",EDGE,"E51"),sQuery(id+"F0.wireOp",EDGE,"E52"),sQuery(id+"F0.wireOp",EDGE,"E53"),sQuery(id+"F0.wireOp",EDGE,"E54"),sQuery(id+"F0.wireOp",EDGE,"E55"),sQuery(id+"F0.wireOp",EDGE,"E56"),sQuery(id+"F0.wireOp",EDGE,"E57"),sQuery(id+"F0.wireOp",EDGE,"E58"),sQuery(id+"F0.wireOp",EDGE,"E59"),sQuery(id+"F0.wireOp",EDGE,"E60"),sQuery(id+"F0.wireOp",EDGE,"E61"),sQuery(id+"F0.wireOp",EDGE,"E62"),sQuery(id+"F0.wireOp",EDGE,"E63"),sQuery(id+"F0.wireOp",EDGE,"E64"),sQuery(id+"F0.wireOp",EDGE,"E65"),sQuery(id+"F0.wireOp",EDGE,"E66"),sQuery(id+"F0.wireOp",EDGE,"E67"),sQuery(id+"F0.wireOp",EDGE,"E68"),sQuery(id+"F0.wireOp",EDGE,"E69"),sQuery(id+"F0.wireOp",EDGE,"E70"),sQuery(id+"F0.wireOp",EDGE,"E71"),sQuery(id+"F0.wireOp",EDGE,"E72"),sQuery(id+"F0.wireOp",EDGE,"E73"),sQuery(id+"F0.wireOp",EDGE,"E74"),sQuery(id+"F0.wireOp",EDGE,"E75"),sQuery(id+"F0.wireOp",EDGE,"E76"),sQuery(id+"F0.wireOp",EDGE,"E77"),sQuery(id+"F0.wireOp",EDGE,"E78"),sQuery(id+"F0.wireOp",EDGE,"E79"),sQuery(id+"F0.wireOp",EDGE,"E80"),sQuery(id+"F0.wireOp",EDGE,"E81"),sQuery(id+"F0.wireOp",EDGE,"E82"),sQuery(id+"F0.wireOp",EDGE,"E83"),sQuery(id+"F0.wireOp",EDGE,"E84"),sQuery(id+"F0.wireOp",EDGE,"E85"),sQuery(id+"F0.wireOp",EDGE,"E86"),sQuery(id+"F0.wireOp",EDGE,"E87"),sQuery(id+"F0.wireOp",EDGE,"E88"),sQuery(id+"F0.wireOp",EDGE,"E89"),sQuery(id+"F0.wireOp",EDGE,"E90"),sQuery(id+"F0.wireOp",EDGE,"E91"),sQuery(id+"F0.wireOp",EDGE,"E92"),sQuery(id+"F0.wireOp",EDGE,"E93"),sQuery(id+"F0.wireOp",EDGE,"E94"),sQuery(id+"F0.wireOp",EDGE,"E95"),sQuery(id+"F0.wireOp",EDGE,"E96"),sQuery(id+"F0.wireOp",EDGE,"E97"),sQuery(id+"F0.wireOp",EDGE,"E98"),sQuery(id+"F0.wireOp",EDGE,"E99"),sQuery(id+"F0.wireOp",EDGE,"E100"),sQuery(id+"F0.wireOp",EDGE,"E101"),sQuery(id+"F0.wireOp",EDGE,"E102"),sQuery(id+"F0.wireOp",EDGE,"E103"),sQuery(id+"F0.wireOp",EDGE,"E104")])]}),"instanceName":"52"});
            var Q20;
            Q20=makeQuery(id+"F2.opPattern","COPY",BODY,{"derivedFrom":makeQuery(id+"F1.opExtrude","SWEPT_BODY",BODY,{"disambiguationData":[OSD([sQuery(id+"F0.wireOp",EDGE,"E1"),sQuery(id+"F0.wireOp",EDGE,"E2"),sQuery(id+"F0.wireOp",EDGE,"E3"),sQuery(id+"F0.wireOp",EDGE,"E4"),sQuery(id+"F0.wireOp",EDGE,"E5"),sQuery(id+"F0.wireOp",EDGE,"E6"),sQuery(id+"F0.wireOp",EDGE,"E7"),sQuery(id+"F0.wireOp",EDGE,"E8"),sQuery(id+"F0.wireOp",EDGE,"E9"),sQuery(id+"F0.wireOp",EDGE,"E10"),sQuery(id+"F0.wireOp",EDGE,"E11"),sQuery(id+"F0.wireOp",EDGE,"E12"),sQuery(id+"F0.wireOp",EDGE,"E13"),sQuery(id+"F0.wireOp",EDGE,"E14"),sQuery(id+"F0.wireOp",EDGE,"E15"),sQuery(id+"F0.wireOp",EDGE,"E16"),sQuery(id+"F0.wireOp",EDGE,"E17"),sQuery(id+"F0.wireOp",EDGE,"E18"),sQuery(id+"F0.wireOp",EDGE,"E19"),sQuery(id+"F0.wireOp",EDGE,"E20"),sQuery(id+"F0.wireOp",EDGE,"E21"),sQuery(id+"F0.wireOp",EDGE,"E22"),sQuery(id+"F0.wireOp",EDGE,"E23"),sQuery(id+"F0.wireOp",EDGE,"E24"),sQuery(id+"F0.wireOp",EDGE,"E25"),sQuery(id+"F0.wireOp",EDGE,"E26"),sQuery(id+"F0.wireOp",EDGE,"E27"),sQuery(id+"F0.wireOp",EDGE,"E28"),sQuery(id+"F0.wireOp",EDGE,"E29"),sQuery(id+"F0.wireOp",EDGE,"E30"),sQuery(id+"F0.wireOp",EDGE,"E31"),sQuery(id+"F0.wireOp",EDGE,"E32"),sQuery(id+"F0.wireOp",EDGE,"E33"),sQuery(id+"F0.wireOp",EDGE,"E34"),sQuery(id+"F0.wireOp",EDGE,"E35"),sQuery(id+"F0.wireOp",EDGE,"E36"),sQuery(id+"F0.wireOp",EDGE,"E37"),sQuery(id+"F0.wireOp",EDGE,"E38"),sQuery(id+"F0.wireOp",EDGE,"E39"),sQuery(id+"F0.wireOp",EDGE,"E40"),sQuery(id+"F0.wireOp",EDGE,"E41"),sQuery(id+"F0.wireOp",EDGE,"E42"),sQuery(id+"F0.wireOp",EDGE,"E43"),sQuery(id+"F0.wireOp",EDGE,"E44"),sQuery(id+"F0.wireOp",EDGE,"E45"),sQuery(id+"F0.wireOp",EDGE,"E46"),sQuery(id+"F0.wireOp",EDGE,"E47"),sQuery(id+"F0.wireOp",EDGE,"E48"),sQuery(id+"F0.wireOp",EDGE,"E49"),sQuery(id+"F0.wireOp",EDGE,"E50"),sQuery(id+"F0.wireOp",EDGE,"E51"),sQuery(id+"F0.wireOp",EDGE,"E52"),sQuery(id+"F0.wireOp",EDGE,"E53"),sQuery(id+"F0.wireOp",EDGE,"E54"),sQuery(id+"F0.wireOp",EDGE,"E55"),sQuery(id+"F0.wireOp",EDGE,"E56"),sQuery(id+"F0.wireOp",EDGE,"E57"),sQuery(id+"F0.wireOp",EDGE,"E58"),sQuery(id+"F0.wireOp",EDGE,"E59"),sQuery(id+"F0.wireOp",EDGE,"E60"),sQuery(id+"F0.wireOp",EDGE,"E61"),sQuery(id+"F0.wireOp",EDGE,"E62"),sQuery(id+"F0.wireOp",EDGE,"E63"),sQuery(id+"F0.wireOp",EDGE,"E64"),sQuery(id+"F0.wireOp",EDGE,"E65"),sQuery(id+"F0.wireOp",EDGE,"E66"),sQuery(id+"F0.wireOp",EDGE,"E67"),sQuery(id+"F0.wireOp",EDGE,"E68"),sQuery(id+"F0.wireOp",EDGE,"E69"),sQuery(id+"F0.wireOp",EDGE,"E70"),sQuery(id+"F0.wireOp",EDGE,"E71"),sQuery(id+"F0.wireOp",EDGE,"E72"),sQuery(id+"F0.wireOp",EDGE,"E73"),sQuery(id+"F0.wireOp",EDGE,"E74"),sQuery(id+"F0.wireOp",EDGE,"E75"),sQuery(id+"F0.wireOp",EDGE,"E76"),sQuery(id+"F0.wireOp",EDGE,"E77"),sQuery(id+"F0.wireOp",EDGE,"E78"),sQuery(id+"F0.wireOp",EDGE,"E79"),sQuery(id+"F0.wireOp",EDGE,"E80"),sQuery(id+"F0.wireOp",EDGE,"E81"),sQuery(id+"F0.wireOp",EDGE,"E82"),sQuery(id+"F0.wireOp",EDGE,"E83"),sQuery(id+"F0.wireOp",EDGE,"E84"),sQuery(id+"F0.wireOp",EDGE,"E85"),sQuery(id+"F0.wireOp",EDGE,"E86"),sQuery(id+"F0.wireOp",EDGE,"E87"),sQuery(id+"F0.wireOp",EDGE,"E88"),sQuery(id+"F0.wireOp",EDGE,"E89"),sQuery(id+"F0.wireOp",EDGE,"E90"),sQuery(id+"F0.wireOp",EDGE,"E91"),sQuery(id+"F0.wireOp",EDGE,"E92"),sQuery(id+"F0.wireOp",EDGE,"E93"),sQuery(id+"F0.wireOp",EDGE,"E94"),sQuery(id+"F0.wireOp",EDGE,"E95"),sQuery(id+"F0.wireOp",EDGE,"E96"),sQuery(id+"F0.wireOp",EDGE,"E97"),sQuery(id+"F0.wireOp",EDGE,"E98"),sQuery(id+"F0.wireOp",EDGE,"E99"),sQuery(id+"F0.wireOp",EDGE,"E100"),sQuery(id+"F0.wireOp",EDGE,"E101"),sQuery(id+"F0.wireOp",EDGE,"E102"),sQuery(id+"F0.wireOp",EDGE,"E103"),sQuery(id+"F0.wireOp",EDGE,"E104")])]}),"instanceName":"53"});
            var Q21;
            Q21=makeQuery(id+"F2.opPattern","COPY",BODY,{"derivedFrom":makeQuery(id+"F1.opExtrude","SWEPT_BODY",BODY,{"disambiguationData":[OSD([sQuery(id+"F0.wireOp",EDGE,"E1"),sQuery(id+"F0.wireOp",EDGE,"E2"),sQuery(id+"F0.wireOp",EDGE,"E3"),sQuery(id+"F0.wireOp",EDGE,"E4"),sQuery(id+"F0.wireOp",EDGE,"E5"),sQuery(id+"F0.wireOp",EDGE,"E6"),sQuery(id+"F0.wireOp",EDGE,"E7"),sQuery(id+"F0.wireOp",EDGE,"E8"),sQuery(id+"F0.wireOp",EDGE,"E9"),sQuery(id+"F0.wireOp",EDGE,"E10"),sQuery(id+"F0.wireOp",EDGE,"E11"),sQuery(id+"F0.wireOp",EDGE,"E12"),sQuery(id+"F0.wireOp",EDGE,"E13"),sQuery(id+"F0.wireOp",EDGE,"E14"),sQuery(id+"F0.wireOp",EDGE,"E15"),sQuery(id+"F0.wireOp",EDGE,"E16"),sQuery(id+"F0.wireOp",EDGE,"E17"),sQuery(id+"F0.wireOp",EDGE,"E18"),sQuery(id+"F0.wireOp",EDGE,"E19"),sQuery(id+"F0.wireOp",EDGE,"E20"),sQuery(id+"F0.wireOp",EDGE,"E21"),sQuery(id+"F0.wireOp",EDGE,"E22"),sQuery(id+"F0.wireOp",EDGE,"E23"),sQuery(id+"F0.wireOp",EDGE,"E24"),sQuery(id+"F0.wireOp",EDGE,"E25"),sQuery(id+"F0.wireOp",EDGE,"E26"),sQuery(id+"F0.wireOp",EDGE,"E27"),sQuery(id+"F0.wireOp",EDGE,"E28"),sQuery(id+"F0.wireOp",EDGE,"E29"),sQuery(id+"F0.wireOp",EDGE,"E30"),sQuery(id+"F0.wireOp",EDGE,"E31"),sQuery(id+"F0.wireOp",EDGE,"E32"),sQuery(id+"F0.wireOp",EDGE,"E33"),sQuery(id+"F0.wireOp",EDGE,"E34"),sQuery(id+"F0.wireOp",EDGE,"E35"),sQuery(id+"F0.wireOp",EDGE,"E36"),sQuery(id+"F0.wireOp",EDGE,"E37"),sQuery(id+"F0.wireOp",EDGE,"E38"),sQuery(id+"F0.wireOp",EDGE,"E39"),sQuery(id+"F0.wireOp",EDGE,"E40"),sQuery(id+"F0.wireOp",EDGE,"E41"),sQuery(id+"F0.wireOp",EDGE,"E42"),sQuery(id+"F0.wireOp",EDGE,"E43"),sQuery(id+"F0.wireOp",EDGE,"E44"),sQuery(id+"F0.wireOp",EDGE,"E45"),sQuery(id+"F0.wireOp",EDGE,"E46"),sQuery(id+"F0.wireOp",EDGE,"E47"),sQuery(id+"F0.wireOp",EDGE,"E48"),sQuery(id+"F0.wireOp",EDGE,"E49"),sQuery(id+"F0.wireOp",EDGE,"E50"),sQuery(id+"F0.wireOp",EDGE,"E51"),sQuery(id+"F0.wireOp",EDGE,"E52"),sQuery(id+"F0.wireOp",EDGE,"E53"),sQuery(id+"F0.wireOp",EDGE,"E54"),sQuery(id+"F0.wireOp",EDGE,"E55"),sQuery(id+"F0.wireOp",EDGE,"E56"),sQuery(id+"F0.wireOp",EDGE,"E57"),sQuery(id+"F0.wireOp",EDGE,"E58"),sQuery(id+"F0.wireOp",EDGE,"E59"),sQuery(id+"F0.wireOp",EDGE,"E60"),sQuery(id+"F0.wireOp",EDGE,"E61"),sQuery(id+"F0.wireOp",EDGE,"E62"),sQuery(id+"F0.wireOp",EDGE,"E63"),sQuery(id+"F0.wireOp",EDGE,"E64"),sQuery(id+"F0.wireOp",EDGE,"E65"),sQuery(id+"F0.wireOp",EDGE,"E66"),sQuery(id+"F0.wireOp",EDGE,"E67"),sQuery(id+"F0.wireOp",EDGE,"E68"),sQuery(id+"F0.wireOp",EDGE,"E69"),sQuery(id+"F0.wireOp",EDGE,"E70"),sQuery(id+"F0.wireOp",EDGE,"E71"),sQuery(id+"F0.wireOp",EDGE,"E72"),sQuery(id+"F0.wireOp",EDGE,"E73"),sQuery(id+"F0.wireOp",EDGE,"E74"),sQuery(id+"F0.wireOp",EDGE,"E75"),sQuery(id+"F0.wireOp",EDGE,"E76"),sQuery(id+"F0.wireOp",EDGE,"E77"),sQuery(id+"F0.wireOp",EDGE,"E78"),sQuery(id+"F0.wireOp",EDGE,"E79"),sQuery(id+"F0.wireOp",EDGE,"E80"),sQuery(id+"F0.wireOp",EDGE,"E81"),sQuery(id+"F0.wireOp",EDGE,"E82"),sQuery(id+"F0.wireOp",EDGE,"E83"),sQuery(id+"F0.wireOp",EDGE,"E84"),sQuery(id+"F0.wireOp",EDGE,"E85"),sQuery(id+"F0.wireOp",EDGE,"E86"),sQuery(id+"F0.wireOp",EDGE,"E87"),sQuery(id+"F0.wireOp",EDGE,"E88"),sQuery(id+"F0.wireOp",EDGE,"E89"),sQuery(id+"F0.wireOp",EDGE,"E90"),sQuery(id+"F0.wireOp",EDGE,"E91"),sQuery(id+"F0.wireOp",EDGE,"E92"),sQuery(id+"F0.wireOp",EDGE,"E93"),sQuery(id+"F0.wireOp",EDGE,"E94"),sQuery(id+"F0.wireOp",EDGE,"E95"),sQuery(id+"F0.wireOp",EDGE,"E96"),sQuery(id+"F0.wireOp",EDGE,"E97"),sQuery(id+"F0.wireOp",EDGE,"E98"),sQuery(id+"F0.wireOp",EDGE,"E99"),sQuery(id+"F0.wireOp",EDGE,"E100"),sQuery(id+"F0.wireOp",EDGE,"E101"),sQuery(id+"F0.wireOp",EDGE,"E102"),sQuery(id+"F0.wireOp",EDGE,"E103"),sQuery(id+"F0.wireOp",EDGE,"E104")])]}),"instanceName":"54"});
            var Q22;
            Q22=makeQuery(id+"F2.opPattern","COPY",BODY,{"derivedFrom":makeQuery(id+"F1.opExtrude","SWEPT_BODY",BODY,{"disambiguationData":[OSD([sQuery(id+"F0.wireOp",EDGE,"E1"),sQuery(id+"F0.wireOp",EDGE,"E2"),sQuery(id+"F0.wireOp",EDGE,"E3"),sQuery(id+"F0.wireOp",EDGE,"E4"),sQuery(id+"F0.wireOp",EDGE,"E5"),sQuery(id+"F0.wireOp",EDGE,"E6"),sQuery(id+"F0.wireOp",EDGE,"E7"),sQuery(id+"F0.wireOp",EDGE,"E8"),sQuery(id+"F0.wireOp",EDGE,"E9"),sQuery(id+"F0.wireOp",EDGE,"E10"),sQuery(id+"F0.wireOp",EDGE,"E11"),sQuery(id+"F0.wireOp",EDGE,"E12"),sQuery(id+"F0.wireOp",EDGE,"E13"),sQuery(id+"F0.wireOp",EDGE,"E14"),sQuery(id+"F0.wireOp",EDGE,"E15"),sQuery(id+"F0.wireOp",EDGE,"E16"),sQuery(id+"F0.wireOp",EDGE,"E17"),sQuery(id+"F0.wireOp",EDGE,"E18"),sQuery(id+"F0.wireOp",EDGE,"E19"),sQuery(id+"F0.wireOp",EDGE,"E20"),sQuery(id+"F0.wireOp",EDGE,"E21"),sQuery(id+"F0.wireOp",EDGE,"E22"),sQuery(id+"F0.wireOp",EDGE,"E23"),sQuery(id+"F0.wireOp",EDGE,"E24"),sQuery(id+"F0.wireOp",EDGE,"E25"),sQuery(id+"F0.wireOp",EDGE,"E26"),sQuery(id+"F0.wireOp",EDGE,"E27"),sQuery(id+"F0.wireOp",EDGE,"E28"),sQuery(id+"F0.wireOp",EDGE,"E29"),sQuery(id+"F0.wireOp",EDGE,"E30"),sQuery(id+"F0.wireOp",EDGE,"E31"),sQuery(id+"F0.wireOp",EDGE,"E32"),sQuery(id+"F0.wireOp",EDGE,"E33"),sQuery(id+"F0.wireOp",EDGE,"E34"),sQuery(id+"F0.wireOp",EDGE,"E35"),sQuery(id+"F0.wireOp",EDGE,"E36"),sQuery(id+"F0.wireOp",EDGE,"E37"),sQuery(id+"F0.wireOp",EDGE,"E38"),sQuery(id+"F0.wireOp",EDGE,"E39"),sQuery(id+"F0.wireOp",EDGE,"E40"),sQuery(id+"F0.wireOp",EDGE,"E41"),sQuery(id+"F0.wireOp",EDGE,"E42"),sQuery(id+"F0.wireOp",EDGE,"E43"),sQuery(id+"F0.wireOp",EDGE,"E44"),sQuery(id+"F0.wireOp",EDGE,"E45"),sQuery(id+"F0.wireOp",EDGE,"E46"),sQuery(id+"F0.wireOp",EDGE,"E47"),sQuery(id+"F0.wireOp",EDGE,"E48"),sQuery(id+"F0.wireOp",EDGE,"E49"),sQuery(id+"F0.wireOp",EDGE,"E50"),sQuery(id+"F0.wireOp",EDGE,"E51"),sQuery(id+"F0.wireOp",EDGE,"E52"),sQuery(id+"F0.wireOp",EDGE,"E53"),sQuery(id+"F0.wireOp",EDGE,"E54"),sQuery(id+"F0.wireOp",EDGE,"E55"),sQuery(id+"F0.wireOp",EDGE,"E56"),sQuery(id+"F0.wireOp",EDGE,"E57"),sQuery(id+"F0.wireOp",EDGE,"E58"),sQuery(id+"F0.wireOp",EDGE,"E59"),sQuery(id+"F0.wireOp",EDGE,"E60"),sQuery(id+"F0.wireOp",EDGE,"E61"),sQuery(id+"F0.wireOp",EDGE,"E62"),sQuery(id+"F0.wireOp",EDGE,"E63"),sQuery(id+"F0.wireOp",EDGE,"E64"),sQuery(id+"F0.wireOp",EDGE,"E65"),sQuery(id+"F0.wireOp",EDGE,"E66"),sQuery(id+"F0.wireOp",EDGE,"E67"),sQuery(id+"F0.wireOp",EDGE,"E68"),sQuery(id+"F0.wireOp",EDGE,"E69"),sQuery(id+"F0.wireOp",EDGE,"E70"),sQuery(id+"F0.wireOp",EDGE,"E71"),sQuery(id+"F0.wireOp",EDGE,"E72"),sQuery(id+"F0.wireOp",EDGE,"E73"),sQuery(id+"F0.wireOp",EDGE,"E74"),sQuery(id+"F0.wireOp",EDGE,"E75"),sQuery(id+"F0.wireOp",EDGE,"E76"),sQuery(id+"F0.wireOp",EDGE,"E77"),sQuery(id+"F0.wireOp",EDGE,"E78"),sQuery(id+"F0.wireOp",EDGE,"E79"),sQuery(id+"F0.wireOp",EDGE,"E80"),sQuery(id+"F0.wireOp",EDGE,"E81"),sQuery(id+"F0.wireOp",EDGE,"E82"),sQuery(id+"F0.wireOp",EDGE,"E83"),sQuery(id+"F0.wireOp",EDGE,"E84"),sQuery(id+"F0.wireOp",EDGE,"E85"),sQuery(id+"F0.wireOp",EDGE,"E86"),sQuery(id+"F0.wireOp",EDGE,"E87"),sQuery(id+"F0.wireOp",EDGE,"E88"),sQuery(id+"F0.wireOp",EDGE,"E89"),sQuery(id+"F0.wireOp",EDGE,"E90"),sQuery(id+"F0.wireOp",EDGE,"E91"),sQuery(id+"F0.wireOp",EDGE,"E92"),sQuery(id+"F0.wireOp",EDGE,"E93"),sQuery(id+"F0.wireOp",EDGE,"E94"),sQuery(id+"F0.wireOp",EDGE,"E95"),sQuery(id+"F0.wireOp",EDGE,"E96"),sQuery(id+"F0.wireOp",EDGE,"E97"),sQuery(id+"F0.wireOp",EDGE,"E98"),sQuery(id+"F0.wireOp",EDGE,"E99"),sQuery(id+"F0.wireOp",EDGE,"E100"),sQuery(id+"F0.wireOp",EDGE,"E101"),sQuery(id+"F0.wireOp",EDGE,"E102"),sQuery(id+"F0.wireOp",EDGE,"E103"),sQuery(id+"F0.wireOp",EDGE,"E104")])]}),"instanceName":"55"});
            booleanBodies(context, id + "F5", {"operationType" : BooleanOperationType.UNION, "tools" : qUnion([Q0, Q1, Q2, Q3, Q4, Q5, Q6, Q7, Q8, Q9, Q10, Q11, Q12, Q13, Q14, Q15, Q16, Q17, Q18, Q19, Q20, Q21, Q22])});
        }
        {
            var Q0;
            Q0=qCreatedBy(makeId("Top.planeOp"),FACE);
            var sketch = newSketch(context, id + "F6", { "sketchPlane" : qUnion([Q0])});
            skCircle(sketch, "E106", {"center": v(0, 0) * mm, "radius": 3.69 * mm});
            skSolve(sketch);
        }
        {
            var Q0;
            Q0=makeQuery(id+"F6.imprint","IMPRINT",FACE,{"disambiguationData":[TD([[makeQuery(id+"F6.imprint","IMPRINT",EDGE,{"derivedFrom":sQuery(id+"F6.wireOp",EDGE,"E106")}),1.0]])]});
            extrude(context, id + "F7", {"entities" : qUnion([Q0]), "operationType" : NewBodyOperationType.REMOVE, "depth" : 25 * mm});
        }
        {
            var Q0;
            Q0=qCreatedBy(makeId("Top.planeOp"),FACE);
            var sketch = newSketch(context, id + "F8", { "sketchPlane" : qUnion([Q0])});
            skLineSegment(sketch, "E107.0", {"start": v(-52.74, -1.17) * mm, "end": v(-52.7, 2.25) * mm});
            skLineSegment(sketch, "E108", {"start": v(-52.73, 0) * mm, "end": v(-52.73, -37.85) * mm});
            skLineSegment(sketch, "E109", {"start": v(-52.73, -37.85) * mm, "end": v(-57.94, -37.85) * mm});
            skLineSegment(sketch, "E110", {"start": v(-57.94, -37.85) * mm, "end": v(-56.98, 30.53) * mm});
            skLineSegment(sketch, "E111", {"start": v(-56.98, 30.53) * mm, "end": v(-52.74, 30.48) * mm});
            skLineSegment(sketch, "E112", {"start": v(-52.74, 30.48) * mm, "end": v(-52.74, -1.17) * mm});
            skLineSegment(sketch, "E113.0", {"start": v(-44.67, 28.06) * mm, "end": v(-42.76, 30.89) * mm});
            skPoint(sketch, "E114.0", {"position": v(-46.4, 25.1) * mm});
            skLineSegment(sketch, "E115.0", {"start": v(-47.92, 22.05) * mm, "end": v(-46.4, 25.1) * mm});
            skLineSegment(sketch, "E116.0", {"start": v(-49.25, 18.9) * mm, "end": v(-47.92, 22.05) * mm});
            skLineSegment(sketch, "E117.0", {"start": v(-50.37, 15.67) * mm, "end": v(-49.25, 18.9) * mm});
            skLineSegment(sketch, "E118.0", {"start": v(-51.28, 12.38) * mm, "end": v(-50.37, 15.67) * mm});
            skLineSegment(sketch, "E119.0", {"start": v(-51.97, 9.04) * mm, "end": v(-51.28, 12.38) * mm});
            skLineSegment(sketch, "E120.0", {"start": v(-52.45, 5.65) * mm, "end": v(-51.97, 9.04) * mm});
            skLineSegment(sketch, "E121.0", {"start": v(-52.7, 2.25) * mm, "end": v(-52.45, 5.65) * mm});
            skLineSegment(sketch, "E122.0", {"start": v(-36.77, -37.82) * mm, "end": v(-39.14, -35.36) * mm});
            skLineSegment(sketch, "E123.0", {"start": v(-39.14, -35.36) * mm, "end": v(-41.35, -32.75) * mm});
            skLineSegment(sketch, "E124.0", {"start": v(-41.35, -32.75) * mm, "end": v(-43.38, -30) * mm});
            skLineSegment(sketch, "E125.0", {"start": v(-43.38, -30) * mm, "end": v(-45.23, -27.14) * mm});
            skLineSegment(sketch, "E126.0", {"start": v(-45.23, -27.14) * mm, "end": v(-46.9, -24.15) * mm});
            skLineSegment(sketch, "E127.0", {"start": v(-46.9, -24.15) * mm, "end": v(-48.36, -21.07) * mm});
            skLineSegment(sketch, "E128.0", {"start": v(-48.36, -21.07) * mm, "end": v(-49.62, -17.9) * mm});
            skLineSegment(sketch, "E129.0", {"start": v(-49.62, -17.9) * mm, "end": v(-50.68, -14.64) * mm});
            skLineSegment(sketch, "E130.0", {"start": v(-50.68, -14.64) * mm, "end": v(-51.52, -11.33) * mm});
            skLineSegment(sketch, "E131.0", {"start": v(-51.52, -11.33) * mm, "end": v(-52.14, -7.97) * mm});
            skLineSegment(sketch, "E132.0", {"start": v(-52.14, -7.97) * mm, "end": v(-52.55, -4.58) * mm});
            skLineSegment(sketch, "E133.0", {"start": v(-52.55, -4.58) * mm, "end": v(-52.74, -1.17) * mm});
            skLineSegment(sketch, "E134", {"start": v(-52.73, -37.85) * mm, "end": v(-36.77, -37.82) * mm});
            skLineSegment(sketch, "E135", {"start": v(-52.74, 30.48) * mm, "end": v(-42.76, 30.89) * mm});
            skLineSegment(sketch, "E136.0", {"start": v(-46.4, 25.1) * mm, "end": v(-44.67, 28.06) * mm});
            skSolve(sketch);
        }
        {
            var Q0;
            {var subQ4=sQuery(id+"F8.wireOp",EDGE,"E109");Q0=makeQuery(id+"F8.imprint","IMPRINT",FACE,{"disambiguationData":[TD([[makeQuery(id+"F8.imprint","IMPRINT",EDGE,{"derivedFrom":subQ4}),-1.0]])]});}
            var Q1;
            {var subQ1=sQuery(id+"F8.wireOp",EDGE,"E112");Q1=makeQuery(id+"F8.imprint","IMPRINT",FACE,{"disambiguationData":[TD([[makeQuery(id+"F8.imprint","IMPRINT",EDGE,{"derivedFrom":subQ1}),1.0]])]});}
            var Q2;
            Q2=makeQuery(id+"F8.imprint","IMPRINT",FACE,{"disambiguationData":[TD([[makeQuery(id+"F8.imprint","IMPRINT",EDGE,{"derivedFrom":sQuery(id+"F8.wireOp",EDGE,"E122.0")}),1.0]])]});
            extrude(context, id + "F9", {"entities" : qUnion([Q0, Q1, Q2]), "operationType" : NewBodyOperationType.ADD, "depth" : 5 * mm});
        }
        {
            var Q0;
            Q0=makeQuery(id+"F9.opExtrude","SWEPT_FACE",FACE,{"disambiguationData":[OSD([sQuery(id+"F8.wireOp",EDGE,"E134")])]});
            var sketch = newSketch(context, id + "F10", { "sketchPlane" : qUnion([Q0])});
            skLineSegment(sketch, "E137.0.0", {"start": v(-58, 0) * mm, "end": v(-52.79, 0) * mm});
            skLineSegment(sketch, "E137.0.1", {"start": v(-52.79, 0) * mm, "end": v(-52.79, 5) * mm});
            skLineSegment(sketch, "E137.0.2", {"start": v(-52.79, 5) * mm, "end": v(-58, 5) * mm});
            skLineSegment(sketch, "E137.0.3", {"start": v(-58, 5) * mm, "end": v(-58, 0) * mm});
            skLineSegment(sketch, "E138.0.0", {"start": v(-52.79, 0) * mm, "end": v(-36.83, 0) * mm});
            skLineSegment(sketch, "E138.0.1", {"start": v(-36.83, 0) * mm, "end": v(-36.83, 5) * mm});
            skLineSegment(sketch, "E138.0.2", {"start": v(-36.83, 5) * mm, "end": v(-52.79, 5) * mm});
            skLineSegment(sketch, "E138.0.3", {"start": v(-52.79, 5) * mm, "end": v(-52.79, 0) * mm});
            skLineSegment(sketch, "E139", {"start": v(-58, 2.5) * mm, "end": v(-52.79, 2.5) * mm, "construction": true});
            skCircle(sketch, "E140", {"center": v(-55.4, 2.5) * mm, "radius": 1.5 * mm});
            skSolve(sketch);
        }
        {
            var Q0;
            {var subQ0=sQuery(id+"F0.wireOp",EDGE,"E0");var subQ1=sQuery(id+"F0.wireOp",EDGE,"E104");Q0=makeQuery(id+"F9.boolean.opBoolean","MERGE",EDGE,{"derivedFrom":[makeQuery(id+"F5.opBoolean","MERGE",EDGE,{"derivedFrom":[makeQuery(id+"F2.opPattern","COPY",EDGE,{"derivedFrom":makeQuery(id+"F1.opExtrude","SWEPT_EDGE",EDGE,{"disambiguationData":[OSD([subQ0,sQuery(id+"F0.wireOp",EDGE,"E102"),subQ1])]}),"instanceName":"36"}),makeQuery(id+"F2.opPattern","COPY",EDGE,{"derivedFrom":makeQuery(id+"F1.opExtrude","SWEPT_EDGE",EDGE,{"disambiguationData":[OSD([subQ0,sQuery(id+"F0.wireOp",EDGE,"E103"),subQ1])]}),"instanceName":"37"})]}),makeQuery(id+"F9.opExtrude","SWEPT_EDGE",EDGE,{"disambiguationData":[OSD([sQuery(id+"F8.wireOp",EDGE,"E122.0"),sQuery(id+"F8.wireOp",EDGE,"E134")])]})]});}
            var Q1;
            {var subQ0=sQuery(id+"F0.wireOp",EDGE,"E0");var subQ1=sQuery(id+"F0.wireOp",EDGE,"E104");Q1=makeQuery(id+"F9.boolean.opBoolean","MERGE",EDGE,{"derivedFrom":[makeQuery(id+"F3.opBoolean","MERGE",EDGE,{"derivedFrom":[makeQuery(id+"F2.opPattern","COPY",EDGE,{"derivedFrom":makeQuery(id+"F1.opExtrude","SWEPT_EDGE",EDGE,{"disambiguationData":[OSD([subQ0,sQuery(id+"F0.wireOp",EDGE,"E102"),subQ1])]}),"instanceName":"14"}),makeQuery(id+"F2.opPattern","COPY",EDGE,{"derivedFrom":makeQuery(id+"F1.opExtrude","SWEPT_EDGE",EDGE,{"disambiguationData":[OSD([subQ0,sQuery(id+"F0.wireOp",EDGE,"E103"),subQ1])]}),"instanceName":"15"})]}),makeQuery(id+"F9.opExtrude","SWEPT_EDGE",EDGE,{"disambiguationData":[OSD([sQuery(id+"F8.wireOp",EDGE,"E113.0"),sQuery(id+"F8.wireOp",EDGE,"E135")])]})]});}
            fillet(context, id + "F11", {"entities" : qUnion([Q0, Q1]), "radius" : 5 * mm, "tangentPropagation" : true, "allowEdgeOverflow" : false});
        }
        {
            var Q0;
            Q0=makeQuery(id+"F10.imprint","IMPRINT",FACE,{"disambiguationData":[TD([[makeQuery(id+"F10.imprint","IMPRINT",EDGE,{"derivedFrom":sQuery(id+"F10.wireOp",EDGE,"E140")}),1.0]])]});
            extrude(context, id + "F12", {"entities" : qUnion([Q0]), "operationType" : NewBodyOperationType.REMOVE, "oppositeDirection" : true, "depth" : 15 * mm});
        }
        {
            var Q0;
            Q0=makeQuery(id+"F9.opExtrude","SWEPT_FACE",FACE,{"disambiguationData":[OSD([sQuery(id+"F8.wireOp",EDGE,"E111")])]});
            var sketch = newSketch(context, id + "F13", { "sketchPlane" : qUnion([Q0])});
            skEllipse(sketch, "E141.0", {"center": v(54.8, 2.5) * mm, "majorRadius": 1.5 * mm, "minorRadius": 1.5 * mm, "majorAxis": v(0, 1)});
            skSolve(sketch);
        }
        {
            var Q0;
            Q0=makeQuery(id+"F13.imprint","IMPRINT",FACE,{"disambiguationData":[TD([[makeQuery(id+"F13.imprint","IMPRINT",EDGE,{"derivedFrom":sQuery(id+"F13.wireOp",EDGE,"E141.0")}),1.0]])]});
            extrude(context, id + "F14", {"entities" : qUnion([Q0]), "operationType" : NewBodyOperationType.REMOVE, "oppositeDirection" : true, "depth" : 25 * mm});
        }
        {
            var Q0;
            {var subQ1=sQuery(id+"F0.wireOp",EDGE,"E103");var subQ3=sQuery(id+"F0.wireOp",EDGE,"E102");var subQ5=makeQuery(id+"F0.imprint","INTERSECT",VERTEX,{"derivedFrom":[subQ3,subQ1]});Q0=makeQuery(id+"F0.imprint","IMPRINT",FACE,{"disambiguationData":[TD([[makeQuery(id+"F0.imprint","IMPRINT",EDGE,{"disambiguationData":[TD([[subQ5,-1.0]])],"derivedFrom":subQ3}),1.0]])]});}
            var Q1;
            {var subQ0=sQuery(id+"F0.wireOp",EDGE,"E103");var subQ3=sQuery(id+"F0.wireOp",EDGE,"E102");var subQ4=makeQuery(id+"F0.imprint","INTERSECT",VERTEX,{"derivedFrom":[subQ3,subQ0]});Q1=makeQuery(id+"F0.imprint","IMPRINT",FACE,{"disambiguationData":[TD([[makeQuery(id+"F0.imprint","IMPRINT",EDGE,{"disambiguationData":[TD([[subQ4,-1.0]])],"derivedFrom":subQ3}),-1.0]])]});}
            extrude(context, id + "F15", {"entities" : qUnion([Q0, Q1]), "oppositeDirection" : true, "depth" : 5 * mm});
        }
        {
            var Q0;
            Q0=makeQuery(id+"F1.opExtrude","SWEPT_BODY",BODY,{"disambiguationData":[OSD([sQuery(id+"F0.wireOp",EDGE,"E1"),sQuery(id+"F0.wireOp",EDGE,"E2"),sQuery(id+"F0.wireOp",EDGE,"E3"),sQuery(id+"F0.wireOp",EDGE,"E4"),sQuery(id+"F0.wireOp",EDGE,"E5"),sQuery(id+"F0.wireOp",EDGE,"E6"),sQuery(id+"F0.wireOp",EDGE,"E7"),sQuery(id+"F0.wireOp",EDGE,"E8"),sQuery(id+"F0.wireOp",EDGE,"E9"),sQuery(id+"F0.wireOp",EDGE,"E10"),sQuery(id+"F0.wireOp",EDGE,"E11"),sQuery(id+"F0.wireOp",EDGE,"E12"),sQuery(id+"F0.wireOp",EDGE,"E13"),sQuery(id+"F0.wireOp",EDGE,"E14"),sQuery(id+"F0.wireOp",EDGE,"E15"),sQuery(id+"F0.wireOp",EDGE,"E16"),sQuery(id+"F0.wireOp",EDGE,"E17"),sQuery(id+"F0.wireOp",EDGE,"E18"),sQuery(id+"F0.wireOp",EDGE,"E19"),sQuery(id+"F0.wireOp",EDGE,"E20"),sQuery(id+"F0.wireOp",EDGE,"E21"),sQuery(id+"F0.wireOp",EDGE,"E22"),sQuery(id+"F0.wireOp",EDGE,"E23"),sQuery(id+"F0.wireOp",EDGE,"E24"),sQuery(id+"F0.wireOp",EDGE,"E25"),sQuery(id+"F0.wireOp",EDGE,"E26"),sQuery(id+"F0.wireOp",EDGE,"E27"),sQuery(id+"F0.wireOp",EDGE,"E28"),sQuery(id+"F0.wireOp",EDGE,"E29"),sQuery(id+"F0.wireOp",EDGE,"E30"),sQuery(id+"F0.wireOp",EDGE,"E31"),sQuery(id+"F0.wireOp",EDGE,"E32"),sQuery(id+"F0.wireOp",EDGE,"E33"),sQuery(id+"F0.wireOp",EDGE,"E34"),sQuery(id+"F0.wireOp",EDGE,"E35"),sQuery(id+"F0.wireOp",EDGE,"E36"),sQuery(id+"F0.wireOp",EDGE,"E37"),sQuery(id+"F0.wireOp",EDGE,"E38"),sQuery(id+"F0.wireOp",EDGE,"E39"),sQuery(id+"F0.wireOp",EDGE,"E40"),sQuery(id+"F0.wireOp",EDGE,"E41"),sQuery(id+"F0.wireOp",EDGE,"E42"),sQuery(id+"F0.wireOp",EDGE,"E43"),sQuery(id+"F0.wireOp",EDGE,"E44"),sQuery(id+"F0.wireOp",EDGE,"E45"),sQuery(id+"F0.wireOp",EDGE,"E46"),sQuery(id+"F0.wireOp",EDGE,"E47"),sQuery(id+"F0.wireOp",EDGE,"E48"),sQuery(id+"F0.wireOp",EDGE,"E49"),sQuery(id+"F0.wireOp",EDGE,"E50"),sQuery(id+"F0.wireOp",EDGE,"E51"),sQuery(id+"F0.wireOp",EDGE,"E52"),sQuery(id+"F0.wireOp",EDGE,"E53"),sQuery(id+"F0.wireOp",EDGE,"E54"),sQuery(id+"F0.wireOp",EDGE,"E55"),sQuery(id+"F0.wireOp",EDGE,"E56"),sQuery(id+"F0.wireOp",EDGE,"E57"),sQuery(id+"F0.wireOp",EDGE,"E58"),sQuery(id+"F0.wireOp",EDGE,"E59"),sQuery(id+"F0.wireOp",EDGE,"E60"),sQuery(id+"F0.wireOp",EDGE,"E61"),sQuery(id+"F0.wireOp",EDGE,"E62"),sQuery(id+"F0.wireOp",EDGE,"E63"),sQuery(id+"F0.wireOp",EDGE,"E64"),sQuery(id+"F0.wireOp",EDGE,"E65"),sQuery(id+"F0.wireOp",EDGE,"E66"),sQuery(id+"F0.wireOp",EDGE,"E67"),sQuery(id+"F0.wireOp",EDGE,"E68"),sQuery(id+"F0.wireOp",EDGE,"E69"),sQuery(id+"F0.wireOp",EDGE,"E70"),sQuery(id+"F0.wireOp",EDGE,"E71"),sQuery(id+"F0.wireOp",EDGE,"E72"),sQuery(id+"F0.wireOp",EDGE,"E73"),sQuery(id+"F0.wireOp",EDGE,"E74"),sQuery(id+"F0.wireOp",EDGE,"E75"),sQuery(id+"F0.wireOp",EDGE,"E76"),sQuery(id+"F0.wireOp",EDGE,"E77"),sQuery(id+"F0.wireOp",EDGE,"E78"),sQuery(id+"F0.wireOp",EDGE,"E79"),sQuery(id+"F0.wireOp",EDGE,"E80"),sQuery(id+"F0.wireOp",EDGE,"E81"),sQuery(id+"F0.wireOp",EDGE,"E82"),sQuery(id+"F0.wireOp",EDGE,"E83"),sQuery(id+"F0.wireOp",EDGE,"E84"),sQuery(id+"F0.wireOp",EDGE,"E85"),sQuery(id+"F0.wireOp",EDGE,"E86"),sQuery(id+"F0.wireOp",EDGE,"E87"),sQuery(id+"F0.wireOp",EDGE,"E88"),sQuery(id+"F0.wireOp",EDGE,"E89"),sQuery(id+"F0.wireOp",EDGE,"E90"),sQuery(id+"F0.wireOp",EDGE,"E91"),sQuery(id+"F0.wireOp",EDGE,"E92"),sQuery(id+"F0.wireOp",EDGE,"E93"),sQuery(id+"F0.wireOp",EDGE,"E94"),sQuery(id+"F0.wireOp",EDGE,"E95"),sQuery(id+"F0.wireOp",EDGE,"E96"),sQuery(id+"F0.wireOp",EDGE,"E97"),sQuery(id+"F0.wireOp",EDGE,"E98"),sQuery(id+"F0.wireOp",EDGE,"E99"),sQuery(id+"F0.wireOp",EDGE,"E100"),sQuery(id+"F0.wireOp",EDGE,"E101"),sQuery(id+"F0.wireOp",EDGE,"E102"),sQuery(id+"F0.wireOp",EDGE,"E103"),sQuery(id+"F0.wireOp",EDGE,"E104")])]});
            var Q1;
            Q1=sQuery(id+"F0.wireOp",VERTEX,"E103.start");
            transform(context, id + "F16", {"entities" : qUnion([Q0]), "transformType" : TransformType.SCALE_UNIFORMLY, "scale" : .6, "makeCopy" : false, "scalePoint" : qUnion([Q1])});
        }
    });
